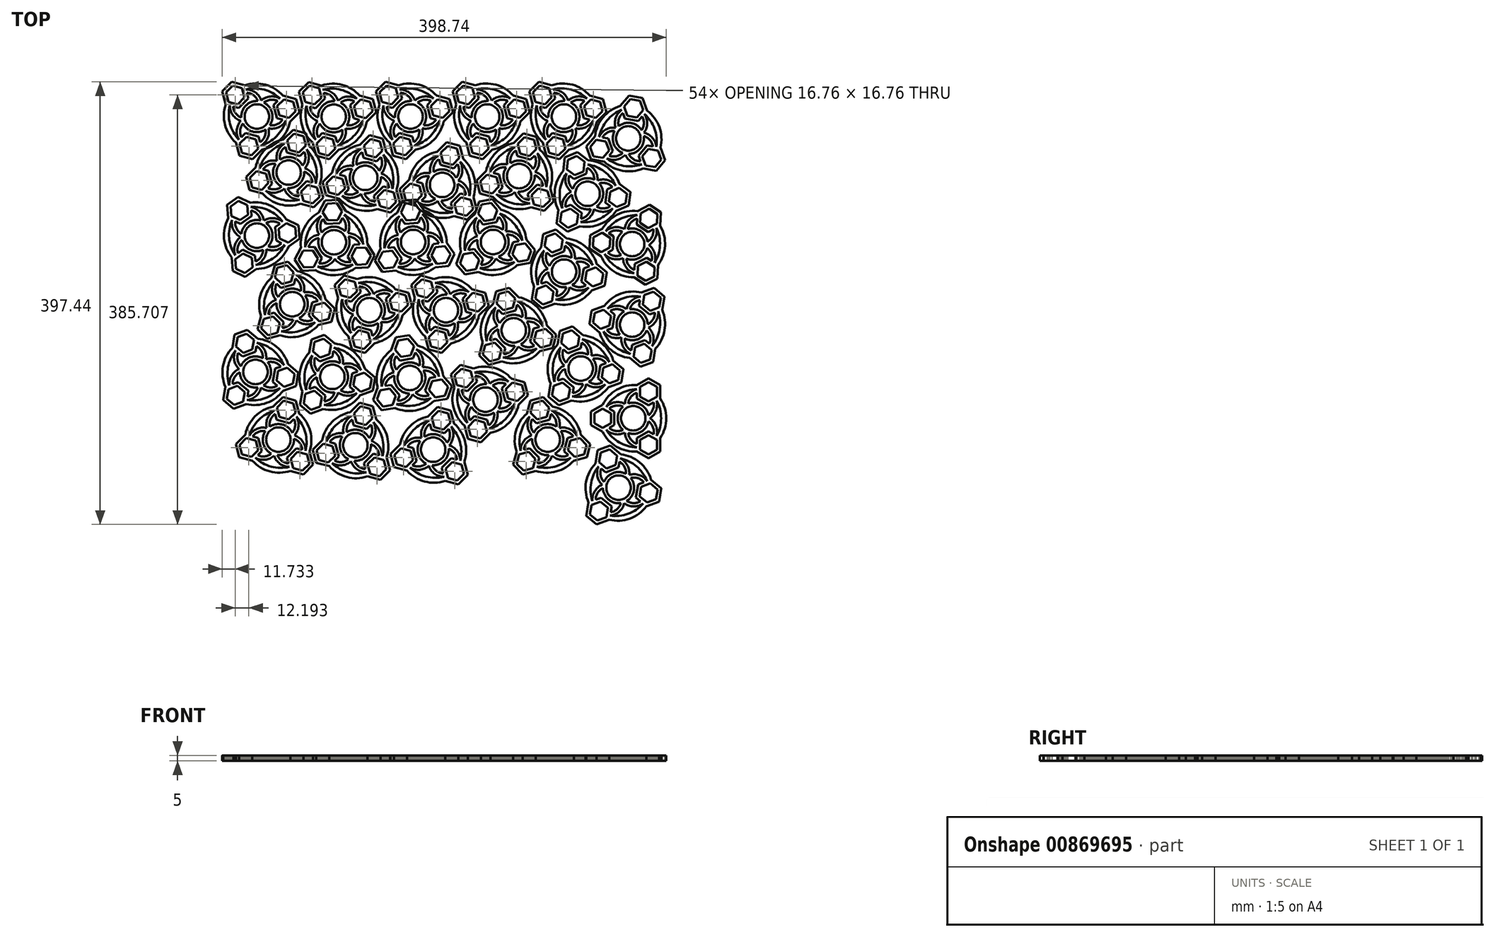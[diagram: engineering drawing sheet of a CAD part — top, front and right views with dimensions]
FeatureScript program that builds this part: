
annotation { "Feature Type Name" : "Feature", "Feature Type Description" : "" }
export const myFeature = defineFeature(function(context is Context, id is Id, definition is map)
    precondition{}
    {
        {
            var Q0;
            Q0=qCreatedBy(makeId("Top.planeOp"),FACE);
            var sketch = newSketch(context, id + "F0", { "sketchPlane" : qUnion([Q0])});
            skArc(sketch, "E0", {"start": v(-13.28, 4.44) * mm, "mid": v(-12.12, -7) * mm, "end": v(-2.8, -13.72) * mm});
            skCircle(sketch, "E1", {"center": v(0, 0) * mm, "radius": 11 * mm});
            skLineSegment(sketch, "E2.0", {"start": v(-4.34, 34.98) * mm, "end": v(4.34, 34.98) * mm});
            skLineSegment(sketch, "E2.1", {"start": v(4.34, 34.98) * mm, "end": v(8.68, 27.46) * mm});
            skLineSegment(sketch, "E2.2", {"start": v(8.68, 27.46) * mm, "end": v(4.34, 19.95) * mm});
            skLineSegment(sketch, "E2.3", {"start": v(4.34, 19.95) * mm, "end": v(-4.34, 19.95) * mm});
            skLineSegment(sketch, "E2.4", {"start": v(-4.34, 19.95) * mm, "end": v(-8.68, 27.46) * mm});
            skLineSegment(sketch, "E2.5", {"start": v(-8.68, 27.46) * mm, "end": v(-4.34, 34.98) * mm});
            skPoint(sketch, "E2.0.midPoint", {"position": v(0, 34.98) * mm});
            skArc(sketch, "E3", {"start": v(-10.28, 24.23) * mm, "mid": v(-14.32, 16.28) * mm, "end": v(-12.95, 7.48) * mm});
            skArc(sketch, "E4", {"start": v(-8.7, 21.51) * mm, "mid": v(-11.38, 15.65) * mm, "end": v(-10.49, 9.28) * mm});
            skLineSegment(sketch, "E5.0", {"start": v(-6.07, 37.98) * mm, "end": v(6.07, 37.98) * mm});
            skLineSegment(sketch, "E5.1", {"start": v(6.07, 37.98) * mm, "end": v(12.14, 27.46) * mm});
            skLineSegment(sketch, "E5.3", {"start": v(6.07, 16.95) * mm, "end": v(-6.07, 16.95) * mm});
            skLineSegment(sketch, "E5.4", {"start": v(-6.07, 16.95) * mm, "end": v(-8.7, 21.51) * mm});
            skLineSegment(sketch, "E5.5", {"start": v(-12.14, 27.46) * mm, "end": v(-6.07, 37.98) * mm});
            skPoint(sketch, "E5.0.midPoint", {"position": v(0, 37.98) * mm});
            skLineSegment(sketch, "E6.trimOffspring", {"start": v(8.7, 21.51) * mm, "end": v(6.07, 16.95) * mm});
            skArc(sketch, "E7.trimOffspring", {"start": v(10.49, 9.28) * mm, "mid": v(11.38, 15.65) * mm, "end": v(8.7, 21.51) * mm});
            skArc(sketch, "E8.trimOffspring", {"start": v(10.49, 9.28) * mm, "mid": v(0, 14) * mm, "end": v(-10.49, 9.28) * mm});
            skArc(sketch, "E9.trimOffspring", {"start": v(12.95, 7.48) * mm, "mid": v(14.32, 16.28) * mm, "end": v(10.28, 24.23) * mm});
            skLineSegment(sketch, "E10.1.0", {"start": v(-32.46, -13.73) * mm, "end": v(-28.12, -6.22) * mm});
            skLineSegment(sketch, "E10.1.1", {"start": v(-17.71, -3.22) * mm, "end": v(-11.64, -13.73) * mm});
            skLineSegment(sketch, "E10.1.2", {"start": v(-22.98, -3.22) * mm, "end": v(-17.71, -3.22) * mm});
            skArc(sketch, "E10.1.3", {"start": v(-12.95, 7.48) * mm, "mid": v(-21.26, 4.26) * mm, "end": v(-26.12, -3.22) * mm});
            skLineSegment(sketch, "E10.1.5", {"start": v(-29.85, -24.25) * mm, "end": v(-35.92, -13.73) * mm});
            skArc(sketch, "E10.1.6", {"start": v(2.8, -13.72) * mm, "mid": v(12.12, -7) * mm, "end": v(13.28, 4.44) * mm});
            skArc(sketch, "E10.1.7", {"start": v(-13.28, 4.44) * mm, "mid": v(-19.25, 2.03) * mm, "end": v(-22.98, -3.22) * mm});
            skLineSegment(sketch, "E10.1.8", {"start": v(-15.1, -13.73) * mm, "end": v(-19.44, -21.25) * mm});
            skLineSegment(sketch, "E10.1.9", {"start": v(-28.12, -6.22) * mm, "end": v(-19.44, -6.22) * mm});
            skLineSegment(sketch, "E10.1.10", {"start": v(-19.44, -6.22) * mm, "end": v(-15.1, -13.73) * mm});
            skLineSegment(sketch, "E10.1.11", {"start": v(-11.64, -13.73) * mm, "end": v(-14.28, -18.3) * mm});
            skArc(sketch, "E10.1.12", {"start": v(-14.28, -18.3) * mm, "mid": v(-7.87, -17.68) * mm, "end": v(-2.8, -13.72) * mm});
            skArc(sketch, "E10.1.14", {"start": v(-15.85, -21.01) * mm, "mid": v(-6.94, -20.54) * mm, "end": v(0, -14.95) * mm});
            skLineSegment(sketch, "E10.1.15", {"start": v(-17.71, -24.25) * mm, "end": v(-29.85, -24.25) * mm});
            skLineSegment(sketch, "E10.1.16", {"start": v(-19.44, -21.25) * mm, "end": v(-28.12, -21.25) * mm});
            skPoint(sketch, "E10.1.17", {"position": v(-30.29, -17.49) * mm});
            skLineSegment(sketch, "E10.1.18", {"start": v(-35.92, -13.73) * mm, "end": v(-29.85, -3.22) * mm});
            skPoint(sketch, "E10.1.19", {"position": v(-32.89, -18.99) * mm});
            skLineSegment(sketch, "E10.1.20", {"start": v(-28.12, -21.25) * mm, "end": v(-32.46, -13.73) * mm});
            skLineSegment(sketch, "E10.2.0", {"start": v(28.12, -21.25) * mm, "end": v(19.44, -21.25) * mm});
            skLineSegment(sketch, "E10.2.1", {"start": v(11.64, -13.73) * mm, "end": v(17.71, -3.22) * mm});
            skLineSegment(sketch, "E10.2.2", {"start": v(14.28, -18.3) * mm, "end": v(11.64, -13.73) * mm});
            skArc(sketch, "E10.2.3", {"start": v(0, -14.95) * mm, "mid": v(6.94, -20.54) * mm, "end": v(15.85, -21.01) * mm});
            skArc(sketch, "E10.2.4", {"start": v(2.8, -13.72) * mm, "mid": v(12.12, -7) * mm, "end": v(13.28, 4.44) * mm});
            skLineSegment(sketch, "E10.2.5", {"start": v(35.92, -13.73) * mm, "end": v(29.85, -24.25) * mm});
            skArc(sketch, "E10.2.7", {"start": v(2.8, -13.72) * mm, "mid": v(7.87, -17.68) * mm, "end": v(14.28, -18.3) * mm});
            skLineSegment(sketch, "E10.2.8", {"start": v(19.44, -6.22) * mm, "end": v(28.12, -6.22) * mm});
            skLineSegment(sketch, "E10.2.9", {"start": v(19.44, -21.25) * mm, "end": v(15.1, -13.73) * mm});
            skLineSegment(sketch, "E10.2.10", {"start": v(15.1, -13.73) * mm, "end": v(19.44, -6.22) * mm});
            skLineSegment(sketch, "E10.2.11", {"start": v(17.71, -3.22) * mm, "end": v(22.98, -3.22) * mm});
            skArc(sketch, "E10.2.12", {"start": v(22.98, -3.22) * mm, "mid": v(19.25, 2.03) * mm, "end": v(13.28, 4.44) * mm});
            skArc(sketch, "E10.2.14", {"start": v(26.12, -3.22) * mm, "mid": v(21.26, 4.26) * mm, "end": v(12.95, 7.48) * mm});
            skLineSegment(sketch, "E10.2.15", {"start": v(29.85, -3.22) * mm, "end": v(35.92, -13.73) * mm});
            skLineSegment(sketch, "E10.2.16", {"start": v(28.12, -6.22) * mm, "end": v(32.46, -13.73) * mm});
            skPoint(sketch, "E10.2.17", {"position": v(30.29, -17.49) * mm});
            skLineSegment(sketch, "E10.2.18", {"start": v(29.85, -24.25) * mm, "end": v(17.71, -24.25) * mm});
            skPoint(sketch, "E10.2.19", {"position": v(32.89, -18.99) * mm});
            skLineSegment(sketch, "E10.2.20", {"start": v(32.46, -13.73) * mm, "end": v(28.12, -21.25) * mm});
            skArc(sketch, "E11", {"start": v(-10.28, 24.23) * mm, "mid": v(-21.68, 12.52) * mm, "end": v(-26.12, -3.22) * mm});
            skArc(sketch, "E12", {"start": v(-12.14, 27.46) * mm, "mid": v(-25.63, 14.8) * mm, "end": v(-29.85, -3.22) * mm});
            skArc(sketch, "E13.1.0", {"start": v(-15.85, -21.01) * mm, "mid": v(0, -25.04) * mm, "end": v(15.85, -21.01) * mm});
            skArc(sketch, "E13.1.1", {"start": v(-17.71, -24.25) * mm, "mid": v(0, -29.6) * mm, "end": v(17.71, -24.25) * mm});
            skArc(sketch, "E13.2.0", {"start": v(26.12, -3.22) * mm, "mid": v(21.68, 12.52) * mm, "end": v(10.28, 24.23) * mm});
            skArc(sketch, "E13.2.1", {"start": v(29.85, -3.22) * mm, "mid": v(25.63, 14.8) * mm, "end": v(12.14, 27.46) * mm});
            skSolve(sketch);
        }
        {
            var Q0;
            Q0=makeQuery(id+"F0.imprint","IMPRINT",FACE,{"disambiguationData":[TD([[makeQuery(id+"F0.imprint","IMPRINT",EDGE,{"derivedFrom":sQuery(id+"F0.wireOp",EDGE,"E2.0")}),1.0]])]});
            extrude(context, id + "F1", {"entities" : qUnion([Q0]), "depth" : 5 * mm, "offsetDistance" : 25 * mm});
        }
        {
            var Q0;
            Q0=makeQuery(id+"F1.opExtrude","SWEPT_BODY",BODY,{"disambiguationData":[OSD([sQuery(id+"F0.wireOp",EDGE,"E2.0"),sQuery(id+"F0.wireOp",EDGE,"E2.1"),sQuery(id+"F0.wireOp",EDGE,"E2.2"),sQuery(id+"F0.wireOp",EDGE,"E2.3"),sQuery(id+"F0.wireOp",EDGE,"E2.4"),sQuery(id+"F0.wireOp",EDGE,"E2.5"),sQuery(id+"F0.wireOp",EDGE,"E3"),sQuery(id+"F0.wireOp",EDGE,"E4"),sQuery(id+"F0.wireOp",EDGE,"E5.0"),sQuery(id+"F0.wireOp",EDGE,"E5.1"),sQuery(id+"F0.wireOp",EDGE,"E5.3"),sQuery(id+"F0.wireOp",EDGE,"E5.4"),sQuery(id+"F0.wireOp",EDGE,"E5.5"),sQuery(id+"F0.wireOp",EDGE,"E6.trimOffspring"),sQuery(id+"F0.wireOp",EDGE,"E7.trimOffspring"),sQuery(id+"F0.wireOp",EDGE,"E9.trimOffspring"),sQuery(id+"F0.wireOp",EDGE,"E10.1.0"),sQuery(id+"F0.wireOp",EDGE,"E10.1.1"),sQuery(id+"F0.wireOp",EDGE,"E10.1.2"),sQuery(id+"F0.wireOp",EDGE,"E10.1.3"),sQuery(id+"F0.wireOp",EDGE,"E10.1.5"),sQuery(id+"F0.wireOp",EDGE,"E10.1.7"),sQuery(id+"F0.wireOp",EDGE,"E10.1.8"),sQuery(id+"F0.wireOp",EDGE,"E10.1.9"),sQuery(id+"F0.wireOp",EDGE,"E10.1.10"),sQuery(id+"F0.wireOp",EDGE,"E10.1.11"),sQuery(id+"F0.wireOp",EDGE,"E10.1.12"),sQuery(id+"F0.wireOp",EDGE,"E10.1.14"),sQuery(id+"F0.wireOp",EDGE,"E10.1.15"),sQuery(id+"F0.wireOp",EDGE,"E10.1.16"),sQuery(id+"F0.wireOp",EDGE,"E10.1.18"),sQuery(id+"F0.wireOp",EDGE,"E10.1.20"),sQuery(id+"F0.wireOp",EDGE,"E10.2.0"),sQuery(id+"F0.wireOp",EDGE,"E10.2.1"),sQuery(id+"F0.wireOp",EDGE,"E10.2.2"),sQuery(id+"F0.wireOp",EDGE,"E10.2.3"),sQuery(id+"F0.wireOp",EDGE,"E10.2.5"),sQuery(id+"F0.wireOp",EDGE,"E10.2.7"),sQuery(id+"F0.wireOp",EDGE,"E10.2.8"),sQuery(id+"F0.wireOp",EDGE,"E10.2.9"),sQuery(id+"F0.wireOp",EDGE,"E10.2.10"),sQuery(id+"F0.wireOp",EDGE,"E10.2.11"),sQuery(id+"F0.wireOp",EDGE,"E10.2.12"),sQuery(id+"F0.wireOp",EDGE,"E1"),sQuery(id+"F0.wireOp",EDGE,"E10.2.14"),sQuery(id+"F0.wireOp",EDGE,"E10.2.15"),sQuery(id+"F0.wireOp",EDGE,"E10.2.16"),sQuery(id+"F0.wireOp",EDGE,"E10.2.18"),sQuery(id+"F0.wireOp",EDGE,"E10.2.20"),sQuery(id+"F0.wireOp",EDGE,"E8.trimOffspring"),sQuery(id+"F0.wireOp",EDGE,"E0"),sQuery(id+"F0.wireOp",EDGE,"E10.1.6"),sQuery(id+"F0.wireOp",EDGE,"E11"),sQuery(id+"F0.wireOp",EDGE,"E12"),sQuery(id+"F0.wireOp",EDGE,"E13.1.0"),sQuery(id+"F0.wireOp",EDGE,"E13.1.1"),sQuery(id+"F0.wireOp",EDGE,"E13.2.0"),sQuery(id+"F0.wireOp",EDGE,"E13.2.1")])]});
            transform(context, id + "F2", {"entities" : qUnion([Q0]), "transformType" : TransformType.TRANSLATION_3D, "dx" : -159 * mm, "dy" : 162 * mm, "dz" : 0 * mm, "makeCopy" : false});
        }
        {
            var Q0;
            Q0=makeQuery(id+"F1.opExtrude","SWEPT_BODY",BODY,{"disambiguationData":[OSD([sQuery(id+"F0.wireOp",EDGE,"E2.0"),sQuery(id+"F0.wireOp",EDGE,"E2.1"),sQuery(id+"F0.wireOp",EDGE,"E2.2"),sQuery(id+"F0.wireOp",EDGE,"E2.3"),sQuery(id+"F0.wireOp",EDGE,"E2.4"),sQuery(id+"F0.wireOp",EDGE,"E2.5"),sQuery(id+"F0.wireOp",EDGE,"E3"),sQuery(id+"F0.wireOp",EDGE,"E4"),sQuery(id+"F0.wireOp",EDGE,"E5.0"),sQuery(id+"F0.wireOp",EDGE,"E5.1"),sQuery(id+"F0.wireOp",EDGE,"E5.3"),sQuery(id+"F0.wireOp",EDGE,"E5.4"),sQuery(id+"F0.wireOp",EDGE,"E5.5"),sQuery(id+"F0.wireOp",EDGE,"E6.trimOffspring"),sQuery(id+"F0.wireOp",EDGE,"E7.trimOffspring"),sQuery(id+"F0.wireOp",EDGE,"E9.trimOffspring"),sQuery(id+"F0.wireOp",EDGE,"E10.1.0"),sQuery(id+"F0.wireOp",EDGE,"E10.1.1"),sQuery(id+"F0.wireOp",EDGE,"E10.1.2"),sQuery(id+"F0.wireOp",EDGE,"E10.1.3"),sQuery(id+"F0.wireOp",EDGE,"E10.1.5"),sQuery(id+"F0.wireOp",EDGE,"E10.1.7"),sQuery(id+"F0.wireOp",EDGE,"E10.1.8"),sQuery(id+"F0.wireOp",EDGE,"E10.1.9"),sQuery(id+"F0.wireOp",EDGE,"E10.1.10"),sQuery(id+"F0.wireOp",EDGE,"E10.1.11"),sQuery(id+"F0.wireOp",EDGE,"E10.1.12"),sQuery(id+"F0.wireOp",EDGE,"E10.1.14"),sQuery(id+"F0.wireOp",EDGE,"E10.1.15"),sQuery(id+"F0.wireOp",EDGE,"E10.1.16"),sQuery(id+"F0.wireOp",EDGE,"E10.1.18"),sQuery(id+"F0.wireOp",EDGE,"E10.1.20"),sQuery(id+"F0.wireOp",EDGE,"E10.2.0"),sQuery(id+"F0.wireOp",EDGE,"E10.2.1"),sQuery(id+"F0.wireOp",EDGE,"E10.2.2"),sQuery(id+"F0.wireOp",EDGE,"E10.2.3"),sQuery(id+"F0.wireOp",EDGE,"E10.2.5"),sQuery(id+"F0.wireOp",EDGE,"E10.2.7"),sQuery(id+"F0.wireOp",EDGE,"E10.2.8"),sQuery(id+"F0.wireOp",EDGE,"E10.2.9"),sQuery(id+"F0.wireOp",EDGE,"E10.2.10"),sQuery(id+"F0.wireOp",EDGE,"E10.2.11"),sQuery(id+"F0.wireOp",EDGE,"E10.2.12"),sQuery(id+"F0.wireOp",EDGE,"E1"),sQuery(id+"F0.wireOp",EDGE,"E10.2.14"),sQuery(id+"F0.wireOp",EDGE,"E10.2.15"),sQuery(id+"F0.wireOp",EDGE,"E10.2.16"),sQuery(id+"F0.wireOp",EDGE,"E10.2.18"),sQuery(id+"F0.wireOp",EDGE,"E10.2.20"),sQuery(id+"F0.wireOp",EDGE,"E8.trimOffspring"),sQuery(id+"F0.wireOp",EDGE,"E0"),sQuery(id+"F0.wireOp",EDGE,"E10.1.6"),sQuery(id+"F0.wireOp",EDGE,"E11"),sQuery(id+"F0.wireOp",EDGE,"E12"),sQuery(id+"F0.wireOp",EDGE,"E13.1.0"),sQuery(id+"F0.wireOp",EDGE,"E13.1.1"),sQuery(id+"F0.wireOp",EDGE,"E13.2.0"),sQuery(id+"F0.wireOp",EDGE,"E13.2.1")])]});
            var Q1;
            Q1=makeQuery(id+"F1.opExtrude","CAP_EDGE",EDGE,{"disambiguationData":[OSD([sQuery(id+"F0.wireOp",EDGE,"E1")])],"isStart":false});
            transform(context, id + "F3", {"entities" : qUnion([Q0]), "transformType" : TransformType.ROTATION, "transformAxis" : qUnion([Q1]), "angle" : 45 * degree, "makeCopy" : false});
        }
        {
            var Q0;
            Q0=makeQuery(id+"F1.opExtrude","SWEPT_BODY",BODY,{"disambiguationData":[OSD([sQuery(id+"F0.wireOp",EDGE,"E2.0"),sQuery(id+"F0.wireOp",EDGE,"E2.1"),sQuery(id+"F0.wireOp",EDGE,"E2.2"),sQuery(id+"F0.wireOp",EDGE,"E2.3"),sQuery(id+"F0.wireOp",EDGE,"E2.4"),sQuery(id+"F0.wireOp",EDGE,"E2.5"),sQuery(id+"F0.wireOp",EDGE,"E3"),sQuery(id+"F0.wireOp",EDGE,"E4"),sQuery(id+"F0.wireOp",EDGE,"E5.0"),sQuery(id+"F0.wireOp",EDGE,"E5.1"),sQuery(id+"F0.wireOp",EDGE,"E5.3"),sQuery(id+"F0.wireOp",EDGE,"E5.4"),sQuery(id+"F0.wireOp",EDGE,"E5.5"),sQuery(id+"F0.wireOp",EDGE,"E6.trimOffspring"),sQuery(id+"F0.wireOp",EDGE,"E7.trimOffspring"),sQuery(id+"F0.wireOp",EDGE,"E9.trimOffspring"),sQuery(id+"F0.wireOp",EDGE,"E10.1.0"),sQuery(id+"F0.wireOp",EDGE,"E10.1.1"),sQuery(id+"F0.wireOp",EDGE,"E10.1.2"),sQuery(id+"F0.wireOp",EDGE,"E10.1.3"),sQuery(id+"F0.wireOp",EDGE,"E10.1.5"),sQuery(id+"F0.wireOp",EDGE,"E10.1.7"),sQuery(id+"F0.wireOp",EDGE,"E10.1.8"),sQuery(id+"F0.wireOp",EDGE,"E10.1.9"),sQuery(id+"F0.wireOp",EDGE,"E10.1.10"),sQuery(id+"F0.wireOp",EDGE,"E10.1.11"),sQuery(id+"F0.wireOp",EDGE,"E10.1.12"),sQuery(id+"F0.wireOp",EDGE,"E10.1.14"),sQuery(id+"F0.wireOp",EDGE,"E10.1.15"),sQuery(id+"F0.wireOp",EDGE,"E10.1.16"),sQuery(id+"F0.wireOp",EDGE,"E10.1.18"),sQuery(id+"F0.wireOp",EDGE,"E10.1.20"),sQuery(id+"F0.wireOp",EDGE,"E10.2.0"),sQuery(id+"F0.wireOp",EDGE,"E10.2.1"),sQuery(id+"F0.wireOp",EDGE,"E10.2.2"),sQuery(id+"F0.wireOp",EDGE,"E10.2.3"),sQuery(id+"F0.wireOp",EDGE,"E10.2.5"),sQuery(id+"F0.wireOp",EDGE,"E10.2.7"),sQuery(id+"F0.wireOp",EDGE,"E10.2.8"),sQuery(id+"F0.wireOp",EDGE,"E10.2.9"),sQuery(id+"F0.wireOp",EDGE,"E10.2.10"),sQuery(id+"F0.wireOp",EDGE,"E10.2.11"),sQuery(id+"F0.wireOp",EDGE,"E10.2.12"),sQuery(id+"F0.wireOp",EDGE,"E1"),sQuery(id+"F0.wireOp",EDGE,"E10.2.14"),sQuery(id+"F0.wireOp",EDGE,"E10.2.15"),sQuery(id+"F0.wireOp",EDGE,"E10.2.16"),sQuery(id+"F0.wireOp",EDGE,"E10.2.18"),sQuery(id+"F0.wireOp",EDGE,"E10.2.20"),sQuery(id+"F0.wireOp",EDGE,"E8.trimOffspring"),sQuery(id+"F0.wireOp",EDGE,"E0"),sQuery(id+"F0.wireOp",EDGE,"E10.1.6"),sQuery(id+"F0.wireOp",EDGE,"E11"),sQuery(id+"F0.wireOp",EDGE,"E12"),sQuery(id+"F0.wireOp",EDGE,"E13.1.0"),sQuery(id+"F0.wireOp",EDGE,"E13.1.1"),sQuery(id+"F0.wireOp",EDGE,"E13.2.0"),sQuery(id+"F0.wireOp",EDGE,"E13.2.1")])]});
            transform(context, id + "F4", {"entities" : qUnion([Q0]), "transformType" : TransformType.TRANSLATION_3D, "dx" : -4.9 * mm, "dy" : 7.3 * mm, "dz" : 0 * mm, "makeCopy" : false});
        }
        {
            var Q0;
            Q0=makeQuery(id+"F1.opExtrude","SWEPT_BODY",BODY,{"disambiguationData":[OSD([sQuery(id+"F0.wireOp",EDGE,"E2.0"),sQuery(id+"F0.wireOp",EDGE,"E2.1"),sQuery(id+"F0.wireOp",EDGE,"E2.2"),sQuery(id+"F0.wireOp",EDGE,"E2.3"),sQuery(id+"F0.wireOp",EDGE,"E2.4"),sQuery(id+"F0.wireOp",EDGE,"E2.5"),sQuery(id+"F0.wireOp",EDGE,"E3"),sQuery(id+"F0.wireOp",EDGE,"E4"),sQuery(id+"F0.wireOp",EDGE,"E5.0"),sQuery(id+"F0.wireOp",EDGE,"E5.1"),sQuery(id+"F0.wireOp",EDGE,"E5.3"),sQuery(id+"F0.wireOp",EDGE,"E5.4"),sQuery(id+"F0.wireOp",EDGE,"E5.5"),sQuery(id+"F0.wireOp",EDGE,"E6.trimOffspring"),sQuery(id+"F0.wireOp",EDGE,"E7.trimOffspring"),sQuery(id+"F0.wireOp",EDGE,"E9.trimOffspring"),sQuery(id+"F0.wireOp",EDGE,"E10.1.0"),sQuery(id+"F0.wireOp",EDGE,"E10.1.1"),sQuery(id+"F0.wireOp",EDGE,"E10.1.2"),sQuery(id+"F0.wireOp",EDGE,"E10.1.3"),sQuery(id+"F0.wireOp",EDGE,"E10.1.5"),sQuery(id+"F0.wireOp",EDGE,"E10.1.7"),sQuery(id+"F0.wireOp",EDGE,"E10.1.8"),sQuery(id+"F0.wireOp",EDGE,"E10.1.9"),sQuery(id+"F0.wireOp",EDGE,"E10.1.10"),sQuery(id+"F0.wireOp",EDGE,"E10.1.11"),sQuery(id+"F0.wireOp",EDGE,"E10.1.12"),sQuery(id+"F0.wireOp",EDGE,"E10.1.14"),sQuery(id+"F0.wireOp",EDGE,"E10.1.15"),sQuery(id+"F0.wireOp",EDGE,"E10.1.16"),sQuery(id+"F0.wireOp",EDGE,"E10.1.18"),sQuery(id+"F0.wireOp",EDGE,"E10.1.20"),sQuery(id+"F0.wireOp",EDGE,"E10.2.0"),sQuery(id+"F0.wireOp",EDGE,"E10.2.1"),sQuery(id+"F0.wireOp",EDGE,"E10.2.2"),sQuery(id+"F0.wireOp",EDGE,"E10.2.3"),sQuery(id+"F0.wireOp",EDGE,"E10.2.5"),sQuery(id+"F0.wireOp",EDGE,"E10.2.7"),sQuery(id+"F0.wireOp",EDGE,"E10.2.8"),sQuery(id+"F0.wireOp",EDGE,"E10.2.9"),sQuery(id+"F0.wireOp",EDGE,"E10.2.10"),sQuery(id+"F0.wireOp",EDGE,"E10.2.11"),sQuery(id+"F0.wireOp",EDGE,"E10.2.12"),sQuery(id+"F0.wireOp",EDGE,"E1"),sQuery(id+"F0.wireOp",EDGE,"E10.2.14"),sQuery(id+"F0.wireOp",EDGE,"E10.2.15"),sQuery(id+"F0.wireOp",EDGE,"E10.2.16"),sQuery(id+"F0.wireOp",EDGE,"E10.2.18"),sQuery(id+"F0.wireOp",EDGE,"E10.2.20"),sQuery(id+"F0.wireOp",EDGE,"E8.trimOffspring"),sQuery(id+"F0.wireOp",EDGE,"E0"),sQuery(id+"F0.wireOp",EDGE,"E10.1.6"),sQuery(id+"F0.wireOp",EDGE,"E11"),sQuery(id+"F0.wireOp",EDGE,"E12"),sQuery(id+"F0.wireOp",EDGE,"E13.1.0"),sQuery(id+"F0.wireOp",EDGE,"E13.1.1"),sQuery(id+"F0.wireOp",EDGE,"E13.2.0"),sQuery(id+"F0.wireOp",EDGE,"E13.2.1")])]});
            transform(context, id + "F5", {"entities" : qUnion([Q0]), "transformType" : TransformType.TRANSLATION_3D, "dx" : 69 * mm, "dy" : -0.1 * mm, "dz" : 0 * mm, "makeCopy" : true});
        }
        {
            var Q0;
            Q0=makeQuery(id+"F5.opPattern","COPY",BODY,{"derivedFrom":makeQuery(id+"F1.opExtrude","SWEPT_BODY",BODY,{"disambiguationData":[OSD([sQuery(id+"F0.wireOp",EDGE,"E2.0"),sQuery(id+"F0.wireOp",EDGE,"E2.1"),sQuery(id+"F0.wireOp",EDGE,"E2.2"),sQuery(id+"F0.wireOp",EDGE,"E2.3"),sQuery(id+"F0.wireOp",EDGE,"E2.4"),sQuery(id+"F0.wireOp",EDGE,"E2.5"),sQuery(id+"F0.wireOp",EDGE,"E3"),sQuery(id+"F0.wireOp",EDGE,"E4"),sQuery(id+"F0.wireOp",EDGE,"E5.0"),sQuery(id+"F0.wireOp",EDGE,"E5.1"),sQuery(id+"F0.wireOp",EDGE,"E5.3"),sQuery(id+"F0.wireOp",EDGE,"E5.4"),sQuery(id+"F0.wireOp",EDGE,"E5.5"),sQuery(id+"F0.wireOp",EDGE,"E6.trimOffspring"),sQuery(id+"F0.wireOp",EDGE,"E7.trimOffspring"),sQuery(id+"F0.wireOp",EDGE,"E9.trimOffspring"),sQuery(id+"F0.wireOp",EDGE,"E10.1.0"),sQuery(id+"F0.wireOp",EDGE,"E10.1.1"),sQuery(id+"F0.wireOp",EDGE,"E10.1.2"),sQuery(id+"F0.wireOp",EDGE,"E10.1.3"),sQuery(id+"F0.wireOp",EDGE,"E10.1.5"),sQuery(id+"F0.wireOp",EDGE,"E10.1.7"),sQuery(id+"F0.wireOp",EDGE,"E10.1.8"),sQuery(id+"F0.wireOp",EDGE,"E10.1.9"),sQuery(id+"F0.wireOp",EDGE,"E10.1.10"),sQuery(id+"F0.wireOp",EDGE,"E10.1.11"),sQuery(id+"F0.wireOp",EDGE,"E10.1.12"),sQuery(id+"F0.wireOp",EDGE,"E10.1.14"),sQuery(id+"F0.wireOp",EDGE,"E10.1.15"),sQuery(id+"F0.wireOp",EDGE,"E10.1.16"),sQuery(id+"F0.wireOp",EDGE,"E10.1.18"),sQuery(id+"F0.wireOp",EDGE,"E10.1.20"),sQuery(id+"F0.wireOp",EDGE,"E10.2.0"),sQuery(id+"F0.wireOp",EDGE,"E10.2.1"),sQuery(id+"F0.wireOp",EDGE,"E10.2.2"),sQuery(id+"F0.wireOp",EDGE,"E10.2.3"),sQuery(id+"F0.wireOp",EDGE,"E10.2.5"),sQuery(id+"F0.wireOp",EDGE,"E10.2.7"),sQuery(id+"F0.wireOp",EDGE,"E10.2.8"),sQuery(id+"F0.wireOp",EDGE,"E10.2.9"),sQuery(id+"F0.wireOp",EDGE,"E10.2.10"),sQuery(id+"F0.wireOp",EDGE,"E10.2.11"),sQuery(id+"F0.wireOp",EDGE,"E10.2.12"),sQuery(id+"F0.wireOp",EDGE,"E1"),sQuery(id+"F0.wireOp",EDGE,"E10.2.14"),sQuery(id+"F0.wireOp",EDGE,"E10.2.15"),sQuery(id+"F0.wireOp",EDGE,"E10.2.16"),sQuery(id+"F0.wireOp",EDGE,"E10.2.18"),sQuery(id+"F0.wireOp",EDGE,"E10.2.20"),sQuery(id+"F0.wireOp",EDGE,"E8.trimOffspring"),sQuery(id+"F0.wireOp",EDGE,"E0"),sQuery(id+"F0.wireOp",EDGE,"E10.1.6"),sQuery(id+"F0.wireOp",EDGE,"E11"),sQuery(id+"F0.wireOp",EDGE,"E12"),sQuery(id+"F0.wireOp",EDGE,"E13.1.0"),sQuery(id+"F0.wireOp",EDGE,"E13.1.1"),sQuery(id+"F0.wireOp",EDGE,"E13.2.0"),sQuery(id+"F0.wireOp",EDGE,"E13.2.1")])]}),"instanceName":"1"});
            var Q1;
            Q1=makeQuery(id+"F5.opPattern","COPY",EDGE,{"derivedFrom":makeQuery(id+"F1.opExtrude","CAP_EDGE",EDGE,{"disambiguationData":[OSD([sQuery(id+"F0.wireOp",EDGE,"E1")])],"isStart":false}),"instanceName":"1"});
            transform(context, id + "F6", {"entities" : qUnion([Q0]), "transformType" : TransformType.ROTATION, "transformAxis" : qUnion([Q1]), "angle" : 120 * degree, "makeCopy" : false});
        }
        {
            var Q0;
            Q0=makeQuery(id+"F1.opExtrude","SWEPT_BODY",BODY,{"disambiguationData":[OSD([sQuery(id+"F0.wireOp",EDGE,"E2.0"),sQuery(id+"F0.wireOp",EDGE,"E2.1"),sQuery(id+"F0.wireOp",EDGE,"E2.2"),sQuery(id+"F0.wireOp",EDGE,"E2.3"),sQuery(id+"F0.wireOp",EDGE,"E2.4"),sQuery(id+"F0.wireOp",EDGE,"E2.5"),sQuery(id+"F0.wireOp",EDGE,"E3"),sQuery(id+"F0.wireOp",EDGE,"E4"),sQuery(id+"F0.wireOp",EDGE,"E5.0"),sQuery(id+"F0.wireOp",EDGE,"E5.1"),sQuery(id+"F0.wireOp",EDGE,"E5.3"),sQuery(id+"F0.wireOp",EDGE,"E5.4"),sQuery(id+"F0.wireOp",EDGE,"E5.5"),sQuery(id+"F0.wireOp",EDGE,"E6.trimOffspring"),sQuery(id+"F0.wireOp",EDGE,"E7.trimOffspring"),sQuery(id+"F0.wireOp",EDGE,"E9.trimOffspring"),sQuery(id+"F0.wireOp",EDGE,"E10.1.0"),sQuery(id+"F0.wireOp",EDGE,"E10.1.1"),sQuery(id+"F0.wireOp",EDGE,"E10.1.2"),sQuery(id+"F0.wireOp",EDGE,"E10.1.3"),sQuery(id+"F0.wireOp",EDGE,"E10.1.5"),sQuery(id+"F0.wireOp",EDGE,"E10.1.7"),sQuery(id+"F0.wireOp",EDGE,"E10.1.8"),sQuery(id+"F0.wireOp",EDGE,"E10.1.9"),sQuery(id+"F0.wireOp",EDGE,"E10.1.10"),sQuery(id+"F0.wireOp",EDGE,"E10.1.11"),sQuery(id+"F0.wireOp",EDGE,"E10.1.12"),sQuery(id+"F0.wireOp",EDGE,"E10.1.14"),sQuery(id+"F0.wireOp",EDGE,"E10.1.15"),sQuery(id+"F0.wireOp",EDGE,"E10.1.16"),sQuery(id+"F0.wireOp",EDGE,"E10.1.18"),sQuery(id+"F0.wireOp",EDGE,"E10.1.20"),sQuery(id+"F0.wireOp",EDGE,"E10.2.0"),sQuery(id+"F0.wireOp",EDGE,"E10.2.1"),sQuery(id+"F0.wireOp",EDGE,"E10.2.2"),sQuery(id+"F0.wireOp",EDGE,"E10.2.3"),sQuery(id+"F0.wireOp",EDGE,"E10.2.5"),sQuery(id+"F0.wireOp",EDGE,"E10.2.7"),sQuery(id+"F0.wireOp",EDGE,"E10.2.8"),sQuery(id+"F0.wireOp",EDGE,"E10.2.9"),sQuery(id+"F0.wireOp",EDGE,"E10.2.10"),sQuery(id+"F0.wireOp",EDGE,"E10.2.11"),sQuery(id+"F0.wireOp",EDGE,"E10.2.12"),sQuery(id+"F0.wireOp",EDGE,"E1"),sQuery(id+"F0.wireOp",EDGE,"E10.2.14"),sQuery(id+"F0.wireOp",EDGE,"E10.2.15"),sQuery(id+"F0.wireOp",EDGE,"E10.2.16"),sQuery(id+"F0.wireOp",EDGE,"E10.2.18"),sQuery(id+"F0.wireOp",EDGE,"E10.2.20"),sQuery(id+"F0.wireOp",EDGE,"E8.trimOffspring"),sQuery(id+"F0.wireOp",EDGE,"E0"),sQuery(id+"F0.wireOp",EDGE,"E10.1.6"),sQuery(id+"F0.wireOp",EDGE,"E11"),sQuery(id+"F0.wireOp",EDGE,"E12"),sQuery(id+"F0.wireOp",EDGE,"E13.1.0"),sQuery(id+"F0.wireOp",EDGE,"E13.1.1"),sQuery(id+"F0.wireOp",EDGE,"E13.2.0"),sQuery(id+"F0.wireOp",EDGE,"E13.2.1")])]});
            transform(context, id + "F7", {"entities" : qUnion([Q0]), "transformType" : TransformType.TRANSLATION_3D, "dx" : 138 * mm, "dy" : 0 * mm, "dz" : 0 * mm, "makeCopy" : true});
        }
        {
            var Q0;
            Q0=makeQuery(id+"F7.opPattern","COPY",BODY,{"derivedFrom":makeQuery(id+"F1.opExtrude","SWEPT_BODY",BODY,{"disambiguationData":[OSD([sQuery(id+"F0.wireOp",EDGE,"E2.0"),sQuery(id+"F0.wireOp",EDGE,"E2.1"),sQuery(id+"F0.wireOp",EDGE,"E2.2"),sQuery(id+"F0.wireOp",EDGE,"E2.3"),sQuery(id+"F0.wireOp",EDGE,"E2.4"),sQuery(id+"F0.wireOp",EDGE,"E2.5"),sQuery(id+"F0.wireOp",EDGE,"E3"),sQuery(id+"F0.wireOp",EDGE,"E4"),sQuery(id+"F0.wireOp",EDGE,"E5.0"),sQuery(id+"F0.wireOp",EDGE,"E5.1"),sQuery(id+"F0.wireOp",EDGE,"E5.3"),sQuery(id+"F0.wireOp",EDGE,"E5.4"),sQuery(id+"F0.wireOp",EDGE,"E5.5"),sQuery(id+"F0.wireOp",EDGE,"E6.trimOffspring"),sQuery(id+"F0.wireOp",EDGE,"E7.trimOffspring"),sQuery(id+"F0.wireOp",EDGE,"E9.trimOffspring"),sQuery(id+"F0.wireOp",EDGE,"E10.1.0"),sQuery(id+"F0.wireOp",EDGE,"E10.1.1"),sQuery(id+"F0.wireOp",EDGE,"E10.1.2"),sQuery(id+"F0.wireOp",EDGE,"E10.1.3"),sQuery(id+"F0.wireOp",EDGE,"E10.1.5"),sQuery(id+"F0.wireOp",EDGE,"E10.1.7"),sQuery(id+"F0.wireOp",EDGE,"E10.1.8"),sQuery(id+"F0.wireOp",EDGE,"E10.1.9"),sQuery(id+"F0.wireOp",EDGE,"E10.1.10"),sQuery(id+"F0.wireOp",EDGE,"E10.1.11"),sQuery(id+"F0.wireOp",EDGE,"E10.1.12"),sQuery(id+"F0.wireOp",EDGE,"E10.1.14"),sQuery(id+"F0.wireOp",EDGE,"E10.1.15"),sQuery(id+"F0.wireOp",EDGE,"E10.1.16"),sQuery(id+"F0.wireOp",EDGE,"E10.1.18"),sQuery(id+"F0.wireOp",EDGE,"E10.1.20"),sQuery(id+"F0.wireOp",EDGE,"E10.2.0"),sQuery(id+"F0.wireOp",EDGE,"E10.2.1"),sQuery(id+"F0.wireOp",EDGE,"E10.2.2"),sQuery(id+"F0.wireOp",EDGE,"E10.2.3"),sQuery(id+"F0.wireOp",EDGE,"E10.2.5"),sQuery(id+"F0.wireOp",EDGE,"E10.2.7"),sQuery(id+"F0.wireOp",EDGE,"E10.2.8"),sQuery(id+"F0.wireOp",EDGE,"E10.2.9"),sQuery(id+"F0.wireOp",EDGE,"E10.2.10"),sQuery(id+"F0.wireOp",EDGE,"E10.2.11"),sQuery(id+"F0.wireOp",EDGE,"E10.2.12"),sQuery(id+"F0.wireOp",EDGE,"E1"),sQuery(id+"F0.wireOp",EDGE,"E10.2.14"),sQuery(id+"F0.wireOp",EDGE,"E10.2.15"),sQuery(id+"F0.wireOp",EDGE,"E10.2.16"),sQuery(id+"F0.wireOp",EDGE,"E10.2.18"),sQuery(id+"F0.wireOp",EDGE,"E10.2.20"),sQuery(id+"F0.wireOp",EDGE,"E8.trimOffspring"),sQuery(id+"F0.wireOp",EDGE,"E0"),sQuery(id+"F0.wireOp",EDGE,"E10.1.6"),sQuery(id+"F0.wireOp",EDGE,"E11"),sQuery(id+"F0.wireOp",EDGE,"E12"),sQuery(id+"F0.wireOp",EDGE,"E13.1.0"),sQuery(id+"F0.wireOp",EDGE,"E13.1.1"),sQuery(id+"F0.wireOp",EDGE,"E13.2.0"),sQuery(id+"F0.wireOp",EDGE,"E13.2.1")])]}),"instanceName":"1"});
            transform(context, id + "F8", {"entities" : qUnion([Q0]), "transformType" : TransformType.TRANSLATION_3D, "dx" : 68.9 * mm, "dy" : 0 * mm, "dz" : 0 * mm, "makeCopy" : true});
        }
        {
            var Q0;
            Q0=makeQuery(id+"F8.opPattern","COPY",BODY,{"derivedFrom":makeQuery(id+"F7.opPattern","COPY",BODY,{"derivedFrom":makeQuery(id+"F1.opExtrude","SWEPT_BODY",BODY,{"disambiguationData":[OSD([sQuery(id+"F0.wireOp",EDGE,"E2.0"),sQuery(id+"F0.wireOp",EDGE,"E2.1"),sQuery(id+"F0.wireOp",EDGE,"E2.2"),sQuery(id+"F0.wireOp",EDGE,"E2.3"),sQuery(id+"F0.wireOp",EDGE,"E2.4"),sQuery(id+"F0.wireOp",EDGE,"E2.5"),sQuery(id+"F0.wireOp",EDGE,"E3"),sQuery(id+"F0.wireOp",EDGE,"E4"),sQuery(id+"F0.wireOp",EDGE,"E5.0"),sQuery(id+"F0.wireOp",EDGE,"E5.1"),sQuery(id+"F0.wireOp",EDGE,"E5.3"),sQuery(id+"F0.wireOp",EDGE,"E5.4"),sQuery(id+"F0.wireOp",EDGE,"E5.5"),sQuery(id+"F0.wireOp",EDGE,"E6.trimOffspring"),sQuery(id+"F0.wireOp",EDGE,"E7.trimOffspring"),sQuery(id+"F0.wireOp",EDGE,"E9.trimOffspring"),sQuery(id+"F0.wireOp",EDGE,"E10.1.0"),sQuery(id+"F0.wireOp",EDGE,"E10.1.1"),sQuery(id+"F0.wireOp",EDGE,"E10.1.2"),sQuery(id+"F0.wireOp",EDGE,"E10.1.3"),sQuery(id+"F0.wireOp",EDGE,"E10.1.5"),sQuery(id+"F0.wireOp",EDGE,"E10.1.7"),sQuery(id+"F0.wireOp",EDGE,"E10.1.8"),sQuery(id+"F0.wireOp",EDGE,"E10.1.9"),sQuery(id+"F0.wireOp",EDGE,"E10.1.10"),sQuery(id+"F0.wireOp",EDGE,"E10.1.11"),sQuery(id+"F0.wireOp",EDGE,"E10.1.12"),sQuery(id+"F0.wireOp",EDGE,"E10.1.14"),sQuery(id+"F0.wireOp",EDGE,"E10.1.15"),sQuery(id+"F0.wireOp",EDGE,"E10.1.16"),sQuery(id+"F0.wireOp",EDGE,"E10.1.18"),sQuery(id+"F0.wireOp",EDGE,"E10.1.20"),sQuery(id+"F0.wireOp",EDGE,"E10.2.0"),sQuery(id+"F0.wireOp",EDGE,"E10.2.1"),sQuery(id+"F0.wireOp",EDGE,"E10.2.2"),sQuery(id+"F0.wireOp",EDGE,"E10.2.3"),sQuery(id+"F0.wireOp",EDGE,"E10.2.5"),sQuery(id+"F0.wireOp",EDGE,"E10.2.7"),sQuery(id+"F0.wireOp",EDGE,"E10.2.8"),sQuery(id+"F0.wireOp",EDGE,"E10.2.9"),sQuery(id+"F0.wireOp",EDGE,"E10.2.10"),sQuery(id+"F0.wireOp",EDGE,"E10.2.11"),sQuery(id+"F0.wireOp",EDGE,"E10.2.12"),sQuery(id+"F0.wireOp",EDGE,"E1"),sQuery(id+"F0.wireOp",EDGE,"E10.2.14"),sQuery(id+"F0.wireOp",EDGE,"E10.2.15"),sQuery(id+"F0.wireOp",EDGE,"E10.2.16"),sQuery(id+"F0.wireOp",EDGE,"E10.2.18"),sQuery(id+"F0.wireOp",EDGE,"E10.2.20"),sQuery(id+"F0.wireOp",EDGE,"E8.trimOffspring"),sQuery(id+"F0.wireOp",EDGE,"E0"),sQuery(id+"F0.wireOp",EDGE,"E10.1.6"),sQuery(id+"F0.wireOp",EDGE,"E11"),sQuery(id+"F0.wireOp",EDGE,"E12"),sQuery(id+"F0.wireOp",EDGE,"E13.1.0"),sQuery(id+"F0.wireOp",EDGE,"E13.1.1"),sQuery(id+"F0.wireOp",EDGE,"E13.2.0"),sQuery(id+"F0.wireOp",EDGE,"E13.2.1")])]}),"instanceName":"1"}),"instanceName":"1"});
            transform(context, id + "F9", {"entities" : qUnion([Q0]), "transformType" : TransformType.TRANSLATION_3D, "dx" : 68.8 * mm, "dy" : 0 * mm, "dz" : 0 * mm, "makeCopy" : true});
        }
        {
            var Q0;
            Q0=makeQuery(id+"F9.opPattern","COPY",BODY,{"derivedFrom":makeQuery(id+"F8.opPattern","COPY",BODY,{"derivedFrom":makeQuery(id+"F7.opPattern","COPY",BODY,{"derivedFrom":makeQuery(id+"F1.opExtrude","SWEPT_BODY",BODY,{"disambiguationData":[OSD([sQuery(id+"F0.wireOp",EDGE,"E2.0"),sQuery(id+"F0.wireOp",EDGE,"E2.1"),sQuery(id+"F0.wireOp",EDGE,"E2.2"),sQuery(id+"F0.wireOp",EDGE,"E2.3"),sQuery(id+"F0.wireOp",EDGE,"E2.4"),sQuery(id+"F0.wireOp",EDGE,"E2.5"),sQuery(id+"F0.wireOp",EDGE,"E3"),sQuery(id+"F0.wireOp",EDGE,"E4"),sQuery(id+"F0.wireOp",EDGE,"E5.0"),sQuery(id+"F0.wireOp",EDGE,"E5.1"),sQuery(id+"F0.wireOp",EDGE,"E5.3"),sQuery(id+"F0.wireOp",EDGE,"E5.4"),sQuery(id+"F0.wireOp",EDGE,"E5.5"),sQuery(id+"F0.wireOp",EDGE,"E6.trimOffspring"),sQuery(id+"F0.wireOp",EDGE,"E7.trimOffspring"),sQuery(id+"F0.wireOp",EDGE,"E9.trimOffspring"),sQuery(id+"F0.wireOp",EDGE,"E10.1.0"),sQuery(id+"F0.wireOp",EDGE,"E10.1.1"),sQuery(id+"F0.wireOp",EDGE,"E10.1.2"),sQuery(id+"F0.wireOp",EDGE,"E10.1.3"),sQuery(id+"F0.wireOp",EDGE,"E10.1.5"),sQuery(id+"F0.wireOp",EDGE,"E10.1.7"),sQuery(id+"F0.wireOp",EDGE,"E10.1.8"),sQuery(id+"F0.wireOp",EDGE,"E10.1.9"),sQuery(id+"F0.wireOp",EDGE,"E10.1.10"),sQuery(id+"F0.wireOp",EDGE,"E10.1.11"),sQuery(id+"F0.wireOp",EDGE,"E10.1.12"),sQuery(id+"F0.wireOp",EDGE,"E10.1.14"),sQuery(id+"F0.wireOp",EDGE,"E10.1.15"),sQuery(id+"F0.wireOp",EDGE,"E10.1.16"),sQuery(id+"F0.wireOp",EDGE,"E10.1.18"),sQuery(id+"F0.wireOp",EDGE,"E10.1.20"),sQuery(id+"F0.wireOp",EDGE,"E10.2.0"),sQuery(id+"F0.wireOp",EDGE,"E10.2.1"),sQuery(id+"F0.wireOp",EDGE,"E10.2.2"),sQuery(id+"F0.wireOp",EDGE,"E10.2.3"),sQuery(id+"F0.wireOp",EDGE,"E10.2.5"),sQuery(id+"F0.wireOp",EDGE,"E10.2.7"),sQuery(id+"F0.wireOp",EDGE,"E10.2.8"),sQuery(id+"F0.wireOp",EDGE,"E10.2.9"),sQuery(id+"F0.wireOp",EDGE,"E10.2.10"),sQuery(id+"F0.wireOp",EDGE,"E10.2.11"),sQuery(id+"F0.wireOp",EDGE,"E10.2.12"),sQuery(id+"F0.wireOp",EDGE,"E1"),sQuery(id+"F0.wireOp",EDGE,"E10.2.14"),sQuery(id+"F0.wireOp",EDGE,"E10.2.15"),sQuery(id+"F0.wireOp",EDGE,"E10.2.16"),sQuery(id+"F0.wireOp",EDGE,"E10.2.18"),sQuery(id+"F0.wireOp",EDGE,"E10.2.20"),sQuery(id+"F0.wireOp",EDGE,"E8.trimOffspring"),sQuery(id+"F0.wireOp",EDGE,"E0"),sQuery(id+"F0.wireOp",EDGE,"E10.1.6"),sQuery(id+"F0.wireOp",EDGE,"E11"),sQuery(id+"F0.wireOp",EDGE,"E12"),sQuery(id+"F0.wireOp",EDGE,"E13.1.0"),sQuery(id+"F0.wireOp",EDGE,"E13.1.1"),sQuery(id+"F0.wireOp",EDGE,"E13.2.0"),sQuery(id+"F0.wireOp",EDGE,"E13.2.1")])]}),"instanceName":"1"}),"instanceName":"1"}),"instanceName":"1"});
            transform(context, id + "F10", {"entities" : qUnion([Q0]), "transformType" : TransformType.TRANSLATION_3D, "dx" : 53.1 * mm, "dy" : -25.6 * mm, "dz" : 0 * mm, "makeCopy" : true});
        }
        {
            var Q0;
            Q0=makeQuery(id+"F10.opPattern","COPY",BODY,{"derivedFrom":makeQuery(id+"F9.opPattern","COPY",BODY,{"derivedFrom":makeQuery(id+"F8.opPattern","COPY",BODY,{"derivedFrom":makeQuery(id+"F7.opPattern","COPY",BODY,{"derivedFrom":makeQuery(id+"F1.opExtrude","SWEPT_BODY",BODY,{"disambiguationData":[OSD([sQuery(id+"F0.wireOp",EDGE,"E2.0"),sQuery(id+"F0.wireOp",EDGE,"E2.1"),sQuery(id+"F0.wireOp",EDGE,"E2.2"),sQuery(id+"F0.wireOp",EDGE,"E2.3"),sQuery(id+"F0.wireOp",EDGE,"E2.4"),sQuery(id+"F0.wireOp",EDGE,"E2.5"),sQuery(id+"F0.wireOp",EDGE,"E3"),sQuery(id+"F0.wireOp",EDGE,"E4"),sQuery(id+"F0.wireOp",EDGE,"E5.0"),sQuery(id+"F0.wireOp",EDGE,"E5.1"),sQuery(id+"F0.wireOp",EDGE,"E5.3"),sQuery(id+"F0.wireOp",EDGE,"E5.4"),sQuery(id+"F0.wireOp",EDGE,"E5.5"),sQuery(id+"F0.wireOp",EDGE,"E6.trimOffspring"),sQuery(id+"F0.wireOp",EDGE,"E7.trimOffspring"),sQuery(id+"F0.wireOp",EDGE,"E9.trimOffspring"),sQuery(id+"F0.wireOp",EDGE,"E10.1.0"),sQuery(id+"F0.wireOp",EDGE,"E10.1.1"),sQuery(id+"F0.wireOp",EDGE,"E10.1.2"),sQuery(id+"F0.wireOp",EDGE,"E10.1.3"),sQuery(id+"F0.wireOp",EDGE,"E10.1.5"),sQuery(id+"F0.wireOp",EDGE,"E10.1.7"),sQuery(id+"F0.wireOp",EDGE,"E10.1.8"),sQuery(id+"F0.wireOp",EDGE,"E10.1.9"),sQuery(id+"F0.wireOp",EDGE,"E10.1.10"),sQuery(id+"F0.wireOp",EDGE,"E10.1.11"),sQuery(id+"F0.wireOp",EDGE,"E10.1.12"),sQuery(id+"F0.wireOp",EDGE,"E10.1.14"),sQuery(id+"F0.wireOp",EDGE,"E10.1.15"),sQuery(id+"F0.wireOp",EDGE,"E10.1.16"),sQuery(id+"F0.wireOp",EDGE,"E10.1.18"),sQuery(id+"F0.wireOp",EDGE,"E10.1.20"),sQuery(id+"F0.wireOp",EDGE,"E10.2.0"),sQuery(id+"F0.wireOp",EDGE,"E10.2.1"),sQuery(id+"F0.wireOp",EDGE,"E10.2.2"),sQuery(id+"F0.wireOp",EDGE,"E10.2.3"),sQuery(id+"F0.wireOp",EDGE,"E10.2.5"),sQuery(id+"F0.wireOp",EDGE,"E10.2.7"),sQuery(id+"F0.wireOp",EDGE,"E10.2.8"),sQuery(id+"F0.wireOp",EDGE,"E10.2.9"),sQuery(id+"F0.wireOp",EDGE,"E10.2.10"),sQuery(id+"F0.wireOp",EDGE,"E10.2.11"),sQuery(id+"F0.wireOp",EDGE,"E10.2.12"),sQuery(id+"F0.wireOp",EDGE,"E1"),sQuery(id+"F0.wireOp",EDGE,"E10.2.14"),sQuery(id+"F0.wireOp",EDGE,"E10.2.15"),sQuery(id+"F0.wireOp",EDGE,"E10.2.16"),sQuery(id+"F0.wireOp",EDGE,"E10.2.18"),sQuery(id+"F0.wireOp",EDGE,"E10.2.20"),sQuery(id+"F0.wireOp",EDGE,"E8.trimOffspring"),sQuery(id+"F0.wireOp",EDGE,"E0"),sQuery(id+"F0.wireOp",EDGE,"E10.1.6"),sQuery(id+"F0.wireOp",EDGE,"E11"),sQuery(id+"F0.wireOp",EDGE,"E12"),sQuery(id+"F0.wireOp",EDGE,"E13.1.0"),sQuery(id+"F0.wireOp",EDGE,"E13.1.1"),sQuery(id+"F0.wireOp",EDGE,"E13.2.0"),sQuery(id+"F0.wireOp",EDGE,"E13.2.1")])]}),"instanceName":"1"}),"instanceName":"1"}),"instanceName":"1"}),"instanceName":"1"});
            var Q1;
            Q1=makeQuery(id+"F10.opPattern","COPY",EDGE,{"derivedFrom":makeQuery(id+"F9.opPattern","COPY",EDGE,{"derivedFrom":makeQuery(id+"F8.opPattern","COPY",EDGE,{"derivedFrom":makeQuery(id+"F7.opPattern","COPY",EDGE,{"derivedFrom":makeQuery(id+"F1.opExtrude","CAP_EDGE",EDGE,{"disambiguationData":[OSD([sQuery(id+"F0.wireOp",EDGE,"E1")])],"isStart":false}),"instanceName":"1"}),"instanceName":"1"}),"instanceName":"1"}),"instanceName":"1"});
            transform(context, id + "F11", {"entities" : qUnion([Q0]), "transformType" : TransformType.ROTATION, "transformAxis" : qUnion([Q1]), "angle" : 55 * degree, "oppositeDirection" : true, "makeCopy" : false});
        }
        {
            var Q0;
            Q0=makeQuery(id+"F10.opPattern","COPY",BODY,{"derivedFrom":makeQuery(id+"F9.opPattern","COPY",BODY,{"derivedFrom":makeQuery(id+"F8.opPattern","COPY",BODY,{"derivedFrom":makeQuery(id+"F7.opPattern","COPY",BODY,{"derivedFrom":makeQuery(id+"F1.opExtrude","SWEPT_BODY",BODY,{"disambiguationData":[OSD([sQuery(id+"F0.wireOp",EDGE,"E2.0"),sQuery(id+"F0.wireOp",EDGE,"E2.1"),sQuery(id+"F0.wireOp",EDGE,"E2.2"),sQuery(id+"F0.wireOp",EDGE,"E2.3"),sQuery(id+"F0.wireOp",EDGE,"E2.4"),sQuery(id+"F0.wireOp",EDGE,"E2.5"),sQuery(id+"F0.wireOp",EDGE,"E3"),sQuery(id+"F0.wireOp",EDGE,"E4"),sQuery(id+"F0.wireOp",EDGE,"E5.0"),sQuery(id+"F0.wireOp",EDGE,"E5.1"),sQuery(id+"F0.wireOp",EDGE,"E5.3"),sQuery(id+"F0.wireOp",EDGE,"E5.4"),sQuery(id+"F0.wireOp",EDGE,"E5.5"),sQuery(id+"F0.wireOp",EDGE,"E6.trimOffspring"),sQuery(id+"F0.wireOp",EDGE,"E7.trimOffspring"),sQuery(id+"F0.wireOp",EDGE,"E9.trimOffspring"),sQuery(id+"F0.wireOp",EDGE,"E10.1.0"),sQuery(id+"F0.wireOp",EDGE,"E10.1.1"),sQuery(id+"F0.wireOp",EDGE,"E10.1.2"),sQuery(id+"F0.wireOp",EDGE,"E10.1.3"),sQuery(id+"F0.wireOp",EDGE,"E10.1.5"),sQuery(id+"F0.wireOp",EDGE,"E10.1.7"),sQuery(id+"F0.wireOp",EDGE,"E10.1.8"),sQuery(id+"F0.wireOp",EDGE,"E10.1.9"),sQuery(id+"F0.wireOp",EDGE,"E10.1.10"),sQuery(id+"F0.wireOp",EDGE,"E10.1.11"),sQuery(id+"F0.wireOp",EDGE,"E10.1.12"),sQuery(id+"F0.wireOp",EDGE,"E10.1.14"),sQuery(id+"F0.wireOp",EDGE,"E10.1.15"),sQuery(id+"F0.wireOp",EDGE,"E10.1.16"),sQuery(id+"F0.wireOp",EDGE,"E10.1.18"),sQuery(id+"F0.wireOp",EDGE,"E10.1.20"),sQuery(id+"F0.wireOp",EDGE,"E10.2.0"),sQuery(id+"F0.wireOp",EDGE,"E10.2.1"),sQuery(id+"F0.wireOp",EDGE,"E10.2.2"),sQuery(id+"F0.wireOp",EDGE,"E10.2.3"),sQuery(id+"F0.wireOp",EDGE,"E10.2.5"),sQuery(id+"F0.wireOp",EDGE,"E10.2.7"),sQuery(id+"F0.wireOp",EDGE,"E10.2.8"),sQuery(id+"F0.wireOp",EDGE,"E10.2.9"),sQuery(id+"F0.wireOp",EDGE,"E10.2.10"),sQuery(id+"F0.wireOp",EDGE,"E10.2.11"),sQuery(id+"F0.wireOp",EDGE,"E10.2.12"),sQuery(id+"F0.wireOp",EDGE,"E1"),sQuery(id+"F0.wireOp",EDGE,"E10.2.14"),sQuery(id+"F0.wireOp",EDGE,"E10.2.15"),sQuery(id+"F0.wireOp",EDGE,"E10.2.16"),sQuery(id+"F0.wireOp",EDGE,"E10.2.18"),sQuery(id+"F0.wireOp",EDGE,"E10.2.20"),sQuery(id+"F0.wireOp",EDGE,"E8.trimOffspring"),sQuery(id+"F0.wireOp",EDGE,"E0"),sQuery(id+"F0.wireOp",EDGE,"E10.1.6"),sQuery(id+"F0.wireOp",EDGE,"E11"),sQuery(id+"F0.wireOp",EDGE,"E12"),sQuery(id+"F0.wireOp",EDGE,"E13.1.0"),sQuery(id+"F0.wireOp",EDGE,"E13.1.1"),sQuery(id+"F0.wireOp",EDGE,"E13.2.0"),sQuery(id+"F0.wireOp",EDGE,"E13.2.1")])]}),"instanceName":"1"}),"instanceName":"1"}),"instanceName":"1"}),"instanceName":"1"});
            transform(context, id + "F12", {"entities" : qUnion([Q0]), "transformType" : TransformType.TRANSLATION_3D, "dx" : 4.8 * mm, "dy" : 6 * mm, "dz" : 0 * mm, "makeCopy" : false});
        }
        {
            var Q0;
            Q0=makeQuery(id+"F1.opExtrude","SWEPT_BODY",BODY,{"disambiguationData":[OSD([sQuery(id+"F0.wireOp",EDGE,"E2.0"),sQuery(id+"F0.wireOp",EDGE,"E2.1"),sQuery(id+"F0.wireOp",EDGE,"E2.2"),sQuery(id+"F0.wireOp",EDGE,"E2.3"),sQuery(id+"F0.wireOp",EDGE,"E2.4"),sQuery(id+"F0.wireOp",EDGE,"E2.5"),sQuery(id+"F0.wireOp",EDGE,"E3"),sQuery(id+"F0.wireOp",EDGE,"E4"),sQuery(id+"F0.wireOp",EDGE,"E5.0"),sQuery(id+"F0.wireOp",EDGE,"E5.1"),sQuery(id+"F0.wireOp",EDGE,"E5.3"),sQuery(id+"F0.wireOp",EDGE,"E5.4"),sQuery(id+"F0.wireOp",EDGE,"E5.5"),sQuery(id+"F0.wireOp",EDGE,"E6.trimOffspring"),sQuery(id+"F0.wireOp",EDGE,"E7.trimOffspring"),sQuery(id+"F0.wireOp",EDGE,"E9.trimOffspring"),sQuery(id+"F0.wireOp",EDGE,"E10.1.0"),sQuery(id+"F0.wireOp",EDGE,"E10.1.1"),sQuery(id+"F0.wireOp",EDGE,"E10.1.2"),sQuery(id+"F0.wireOp",EDGE,"E10.1.3"),sQuery(id+"F0.wireOp",EDGE,"E10.1.5"),sQuery(id+"F0.wireOp",EDGE,"E10.1.7"),sQuery(id+"F0.wireOp",EDGE,"E10.1.8"),sQuery(id+"F0.wireOp",EDGE,"E10.1.9"),sQuery(id+"F0.wireOp",EDGE,"E10.1.10"),sQuery(id+"F0.wireOp",EDGE,"E10.1.11"),sQuery(id+"F0.wireOp",EDGE,"E10.1.12"),sQuery(id+"F0.wireOp",EDGE,"E10.1.14"),sQuery(id+"F0.wireOp",EDGE,"E10.1.15"),sQuery(id+"F0.wireOp",EDGE,"E10.1.16"),sQuery(id+"F0.wireOp",EDGE,"E10.1.18"),sQuery(id+"F0.wireOp",EDGE,"E10.1.20"),sQuery(id+"F0.wireOp",EDGE,"E10.2.0"),sQuery(id+"F0.wireOp",EDGE,"E10.2.1"),sQuery(id+"F0.wireOp",EDGE,"E10.2.2"),sQuery(id+"F0.wireOp",EDGE,"E10.2.3"),sQuery(id+"F0.wireOp",EDGE,"E10.2.5"),sQuery(id+"F0.wireOp",EDGE,"E10.2.7"),sQuery(id+"F0.wireOp",EDGE,"E10.2.8"),sQuery(id+"F0.wireOp",EDGE,"E10.2.9"),sQuery(id+"F0.wireOp",EDGE,"E10.2.10"),sQuery(id+"F0.wireOp",EDGE,"E10.2.11"),sQuery(id+"F0.wireOp",EDGE,"E10.2.12"),sQuery(id+"F0.wireOp",EDGE,"E1"),sQuery(id+"F0.wireOp",EDGE,"E10.2.14"),sQuery(id+"F0.wireOp",EDGE,"E10.2.15"),sQuery(id+"F0.wireOp",EDGE,"E10.2.16"),sQuery(id+"F0.wireOp",EDGE,"E10.2.18"),sQuery(id+"F0.wireOp",EDGE,"E10.2.20"),sQuery(id+"F0.wireOp",EDGE,"E8.trimOffspring"),sQuery(id+"F0.wireOp",EDGE,"E0"),sQuery(id+"F0.wireOp",EDGE,"E10.1.6"),sQuery(id+"F0.wireOp",EDGE,"E11"),sQuery(id+"F0.wireOp",EDGE,"E12"),sQuery(id+"F0.wireOp",EDGE,"E13.1.0"),sQuery(id+"F0.wireOp",EDGE,"E13.1.1"),sQuery(id+"F0.wireOp",EDGE,"E13.2.0"),sQuery(id+"F0.wireOp",EDGE,"E13.2.1")])]});
            transform(context, id + "F13", {"entities" : qUnion([Q0]), "transformType" : TransformType.TRANSLATION_3D, "dx" : 36.7 * mm, "dy" : -60.6 * mm, "dz" : 0 * mm, "makeCopy" : true});
        }
        {
            var Q0;
            Q0=makeQuery(id+"F13.opPattern","COPY",BODY,{"derivedFrom":makeQuery(id+"F1.opExtrude","SWEPT_BODY",BODY,{"disambiguationData":[OSD([sQuery(id+"F0.wireOp",EDGE,"E2.0"),sQuery(id+"F0.wireOp",EDGE,"E2.1"),sQuery(id+"F0.wireOp",EDGE,"E2.2"),sQuery(id+"F0.wireOp",EDGE,"E2.3"),sQuery(id+"F0.wireOp",EDGE,"E2.4"),sQuery(id+"F0.wireOp",EDGE,"E2.5"),sQuery(id+"F0.wireOp",EDGE,"E3"),sQuery(id+"F0.wireOp",EDGE,"E4"),sQuery(id+"F0.wireOp",EDGE,"E5.0"),sQuery(id+"F0.wireOp",EDGE,"E5.1"),sQuery(id+"F0.wireOp",EDGE,"E5.3"),sQuery(id+"F0.wireOp",EDGE,"E5.4"),sQuery(id+"F0.wireOp",EDGE,"E5.5"),sQuery(id+"F0.wireOp",EDGE,"E6.trimOffspring"),sQuery(id+"F0.wireOp",EDGE,"E7.trimOffspring"),sQuery(id+"F0.wireOp",EDGE,"E9.trimOffspring"),sQuery(id+"F0.wireOp",EDGE,"E10.1.0"),sQuery(id+"F0.wireOp",EDGE,"E10.1.1"),sQuery(id+"F0.wireOp",EDGE,"E10.1.2"),sQuery(id+"F0.wireOp",EDGE,"E10.1.3"),sQuery(id+"F0.wireOp",EDGE,"E10.1.5"),sQuery(id+"F0.wireOp",EDGE,"E10.1.7"),sQuery(id+"F0.wireOp",EDGE,"E10.1.8"),sQuery(id+"F0.wireOp",EDGE,"E10.1.9"),sQuery(id+"F0.wireOp",EDGE,"E10.1.10"),sQuery(id+"F0.wireOp",EDGE,"E10.1.11"),sQuery(id+"F0.wireOp",EDGE,"E10.1.12"),sQuery(id+"F0.wireOp",EDGE,"E10.1.14"),sQuery(id+"F0.wireOp",EDGE,"E10.1.15"),sQuery(id+"F0.wireOp",EDGE,"E10.1.16"),sQuery(id+"F0.wireOp",EDGE,"E10.1.18"),sQuery(id+"F0.wireOp",EDGE,"E10.1.20"),sQuery(id+"F0.wireOp",EDGE,"E10.2.0"),sQuery(id+"F0.wireOp",EDGE,"E10.2.1"),sQuery(id+"F0.wireOp",EDGE,"E10.2.2"),sQuery(id+"F0.wireOp",EDGE,"E10.2.3"),sQuery(id+"F0.wireOp",EDGE,"E10.2.5"),sQuery(id+"F0.wireOp",EDGE,"E10.2.7"),sQuery(id+"F0.wireOp",EDGE,"E10.2.8"),sQuery(id+"F0.wireOp",EDGE,"E10.2.9"),sQuery(id+"F0.wireOp",EDGE,"E10.2.10"),sQuery(id+"F0.wireOp",EDGE,"E10.2.11"),sQuery(id+"F0.wireOp",EDGE,"E10.2.12"),sQuery(id+"F0.wireOp",EDGE,"E1"),sQuery(id+"F0.wireOp",EDGE,"E10.2.14"),sQuery(id+"F0.wireOp",EDGE,"E10.2.15"),sQuery(id+"F0.wireOp",EDGE,"E10.2.16"),sQuery(id+"F0.wireOp",EDGE,"E10.2.18"),sQuery(id+"F0.wireOp",EDGE,"E10.2.20"),sQuery(id+"F0.wireOp",EDGE,"E8.trimOffspring"),sQuery(id+"F0.wireOp",EDGE,"E0"),sQuery(id+"F0.wireOp",EDGE,"E10.1.6"),sQuery(id+"F0.wireOp",EDGE,"E11"),sQuery(id+"F0.wireOp",EDGE,"E12"),sQuery(id+"F0.wireOp",EDGE,"E13.1.0"),sQuery(id+"F0.wireOp",EDGE,"E13.1.1"),sQuery(id+"F0.wireOp",EDGE,"E13.2.0"),sQuery(id+"F0.wireOp",EDGE,"E13.2.1")])]}),"instanceName":"1"});
            var Q1;
            Q1=makeQuery(id+"F13.opPattern","COPY",EDGE,{"derivedFrom":makeQuery(id+"F1.opExtrude","CAP_EDGE",EDGE,{"disambiguationData":[OSD([sQuery(id+"F0.wireOp",EDGE,"E1")])],"isStart":false}),"instanceName":"1"});
            transform(context, id + "F14", {"entities" : qUnion([Q0]), "transformType" : TransformType.ROTATION, "transformAxis" : qUnion([Q1]), "angle" : 45 * degree, "oppositeDirection" : true, "makeCopy" : false});
        }
        {
            var Q0;
            Q0=makeQuery(id+"F13.opPattern","COPY",BODY,{"derivedFrom":makeQuery(id+"F1.opExtrude","SWEPT_BODY",BODY,{"disambiguationData":[OSD([sQuery(id+"F0.wireOp",EDGE,"E2.0"),sQuery(id+"F0.wireOp",EDGE,"E2.1"),sQuery(id+"F0.wireOp",EDGE,"E2.2"),sQuery(id+"F0.wireOp",EDGE,"E2.3"),sQuery(id+"F0.wireOp",EDGE,"E2.4"),sQuery(id+"F0.wireOp",EDGE,"E2.5"),sQuery(id+"F0.wireOp",EDGE,"E3"),sQuery(id+"F0.wireOp",EDGE,"E4"),sQuery(id+"F0.wireOp",EDGE,"E5.0"),sQuery(id+"F0.wireOp",EDGE,"E5.1"),sQuery(id+"F0.wireOp",EDGE,"E5.3"),sQuery(id+"F0.wireOp",EDGE,"E5.4"),sQuery(id+"F0.wireOp",EDGE,"E5.5"),sQuery(id+"F0.wireOp",EDGE,"E6.trimOffspring"),sQuery(id+"F0.wireOp",EDGE,"E7.trimOffspring"),sQuery(id+"F0.wireOp",EDGE,"E9.trimOffspring"),sQuery(id+"F0.wireOp",EDGE,"E10.1.0"),sQuery(id+"F0.wireOp",EDGE,"E10.1.1"),sQuery(id+"F0.wireOp",EDGE,"E10.1.2"),sQuery(id+"F0.wireOp",EDGE,"E10.1.3"),sQuery(id+"F0.wireOp",EDGE,"E10.1.5"),sQuery(id+"F0.wireOp",EDGE,"E10.1.7"),sQuery(id+"F0.wireOp",EDGE,"E10.1.8"),sQuery(id+"F0.wireOp",EDGE,"E10.1.9"),sQuery(id+"F0.wireOp",EDGE,"E10.1.10"),sQuery(id+"F0.wireOp",EDGE,"E10.1.11"),sQuery(id+"F0.wireOp",EDGE,"E10.1.12"),sQuery(id+"F0.wireOp",EDGE,"E10.1.14"),sQuery(id+"F0.wireOp",EDGE,"E10.1.15"),sQuery(id+"F0.wireOp",EDGE,"E10.1.16"),sQuery(id+"F0.wireOp",EDGE,"E10.1.18"),sQuery(id+"F0.wireOp",EDGE,"E10.1.20"),sQuery(id+"F0.wireOp",EDGE,"E10.2.0"),sQuery(id+"F0.wireOp",EDGE,"E10.2.1"),sQuery(id+"F0.wireOp",EDGE,"E10.2.2"),sQuery(id+"F0.wireOp",EDGE,"E10.2.3"),sQuery(id+"F0.wireOp",EDGE,"E10.2.5"),sQuery(id+"F0.wireOp",EDGE,"E10.2.7"),sQuery(id+"F0.wireOp",EDGE,"E10.2.8"),sQuery(id+"F0.wireOp",EDGE,"E10.2.9"),sQuery(id+"F0.wireOp",EDGE,"E10.2.10"),sQuery(id+"F0.wireOp",EDGE,"E10.2.11"),sQuery(id+"F0.wireOp",EDGE,"E10.2.12"),sQuery(id+"F0.wireOp",EDGE,"E1"),sQuery(id+"F0.wireOp",EDGE,"E10.2.14"),sQuery(id+"F0.wireOp",EDGE,"E10.2.15"),sQuery(id+"F0.wireOp",EDGE,"E10.2.16"),sQuery(id+"F0.wireOp",EDGE,"E10.2.18"),sQuery(id+"F0.wireOp",EDGE,"E10.2.20"),sQuery(id+"F0.wireOp",EDGE,"E8.trimOffspring"),sQuery(id+"F0.wireOp",EDGE,"E0"),sQuery(id+"F0.wireOp",EDGE,"E10.1.6"),sQuery(id+"F0.wireOp",EDGE,"E11"),sQuery(id+"F0.wireOp",EDGE,"E12"),sQuery(id+"F0.wireOp",EDGE,"E13.1.0"),sQuery(id+"F0.wireOp",EDGE,"E13.1.1"),sQuery(id+"F0.wireOp",EDGE,"E13.2.0"),sQuery(id+"F0.wireOp",EDGE,"E13.2.1")])]}),"instanceName":"1"});
            transform(context, id + "F15", {"entities" : qUnion([Q0]), "transformType" : TransformType.TRANSLATION_3D, "dx" : -10.1 * mm, "dy" : 10.3 * mm, "dz" : 0 * mm, "makeCopy" : false});
        }
        {
            var Q0;
            Q0=makeQuery(id+"F13.opPattern","COPY",BODY,{"derivedFrom":makeQuery(id+"F1.opExtrude","SWEPT_BODY",BODY,{"disambiguationData":[OSD([sQuery(id+"F0.wireOp",EDGE,"E2.0"),sQuery(id+"F0.wireOp",EDGE,"E2.1"),sQuery(id+"F0.wireOp",EDGE,"E2.2"),sQuery(id+"F0.wireOp",EDGE,"E2.3"),sQuery(id+"F0.wireOp",EDGE,"E2.4"),sQuery(id+"F0.wireOp",EDGE,"E2.5"),sQuery(id+"F0.wireOp",EDGE,"E3"),sQuery(id+"F0.wireOp",EDGE,"E4"),sQuery(id+"F0.wireOp",EDGE,"E5.0"),sQuery(id+"F0.wireOp",EDGE,"E5.1"),sQuery(id+"F0.wireOp",EDGE,"E5.3"),sQuery(id+"F0.wireOp",EDGE,"E5.4"),sQuery(id+"F0.wireOp",EDGE,"E5.5"),sQuery(id+"F0.wireOp",EDGE,"E6.trimOffspring"),sQuery(id+"F0.wireOp",EDGE,"E7.trimOffspring"),sQuery(id+"F0.wireOp",EDGE,"E9.trimOffspring"),sQuery(id+"F0.wireOp",EDGE,"E10.1.0"),sQuery(id+"F0.wireOp",EDGE,"E10.1.1"),sQuery(id+"F0.wireOp",EDGE,"E10.1.2"),sQuery(id+"F0.wireOp",EDGE,"E10.1.3"),sQuery(id+"F0.wireOp",EDGE,"E10.1.5"),sQuery(id+"F0.wireOp",EDGE,"E10.1.7"),sQuery(id+"F0.wireOp",EDGE,"E10.1.8"),sQuery(id+"F0.wireOp",EDGE,"E10.1.9"),sQuery(id+"F0.wireOp",EDGE,"E10.1.10"),sQuery(id+"F0.wireOp",EDGE,"E10.1.11"),sQuery(id+"F0.wireOp",EDGE,"E10.1.12"),sQuery(id+"F0.wireOp",EDGE,"E10.1.14"),sQuery(id+"F0.wireOp",EDGE,"E10.1.15"),sQuery(id+"F0.wireOp",EDGE,"E10.1.16"),sQuery(id+"F0.wireOp",EDGE,"E10.1.18"),sQuery(id+"F0.wireOp",EDGE,"E10.1.20"),sQuery(id+"F0.wireOp",EDGE,"E10.2.0"),sQuery(id+"F0.wireOp",EDGE,"E10.2.1"),sQuery(id+"F0.wireOp",EDGE,"E10.2.2"),sQuery(id+"F0.wireOp",EDGE,"E10.2.3"),sQuery(id+"F0.wireOp",EDGE,"E10.2.5"),sQuery(id+"F0.wireOp",EDGE,"E10.2.7"),sQuery(id+"F0.wireOp",EDGE,"E10.2.8"),sQuery(id+"F0.wireOp",EDGE,"E10.2.9"),sQuery(id+"F0.wireOp",EDGE,"E10.2.10"),sQuery(id+"F0.wireOp",EDGE,"E10.2.11"),sQuery(id+"F0.wireOp",EDGE,"E10.2.12"),sQuery(id+"F0.wireOp",EDGE,"E1"),sQuery(id+"F0.wireOp",EDGE,"E10.2.14"),sQuery(id+"F0.wireOp",EDGE,"E10.2.15"),sQuery(id+"F0.wireOp",EDGE,"E10.2.16"),sQuery(id+"F0.wireOp",EDGE,"E10.2.18"),sQuery(id+"F0.wireOp",EDGE,"E10.2.20"),sQuery(id+"F0.wireOp",EDGE,"E8.trimOffspring"),sQuery(id+"F0.wireOp",EDGE,"E0"),sQuery(id+"F0.wireOp",EDGE,"E10.1.6"),sQuery(id+"F0.wireOp",EDGE,"E11"),sQuery(id+"F0.wireOp",EDGE,"E12"),sQuery(id+"F0.wireOp",EDGE,"E13.1.0"),sQuery(id+"F0.wireOp",EDGE,"E13.1.1"),sQuery(id+"F0.wireOp",EDGE,"E13.2.0"),sQuery(id+"F0.wireOp",EDGE,"E13.2.1")])]}),"instanceName":"1"});
            var Q1;
            Q1=makeQuery(id+"F13.opPattern","COPY",EDGE,{"derivedFrom":makeQuery(id+"F1.opExtrude","CAP_EDGE",EDGE,{"disambiguationData":[OSD([sQuery(id+"F0.wireOp",EDGE,"E1")])],"isStart":false}),"instanceName":"1"});
            transform(context, id + "F16", {"entities" : qUnion([Q0]), "transformType" : TransformType.ROTATION, "transformAxis" : qUnion([Q1]), "angle" : 15 * degree, "oppositeDirection" : true, "makeCopy" : false});
        }
        {
            var Q0;
            Q0=makeQuery(id+"F13.opPattern","COPY",BODY,{"derivedFrom":makeQuery(id+"F1.opExtrude","SWEPT_BODY",BODY,{"disambiguationData":[OSD([sQuery(id+"F0.wireOp",EDGE,"E2.0"),sQuery(id+"F0.wireOp",EDGE,"E2.1"),sQuery(id+"F0.wireOp",EDGE,"E2.2"),sQuery(id+"F0.wireOp",EDGE,"E2.3"),sQuery(id+"F0.wireOp",EDGE,"E2.4"),sQuery(id+"F0.wireOp",EDGE,"E2.5"),sQuery(id+"F0.wireOp",EDGE,"E3"),sQuery(id+"F0.wireOp",EDGE,"E4"),sQuery(id+"F0.wireOp",EDGE,"E5.0"),sQuery(id+"F0.wireOp",EDGE,"E5.1"),sQuery(id+"F0.wireOp",EDGE,"E5.3"),sQuery(id+"F0.wireOp",EDGE,"E5.4"),sQuery(id+"F0.wireOp",EDGE,"E5.5"),sQuery(id+"F0.wireOp",EDGE,"E6.trimOffspring"),sQuery(id+"F0.wireOp",EDGE,"E7.trimOffspring"),sQuery(id+"F0.wireOp",EDGE,"E9.trimOffspring"),sQuery(id+"F0.wireOp",EDGE,"E10.1.0"),sQuery(id+"F0.wireOp",EDGE,"E10.1.1"),sQuery(id+"F0.wireOp",EDGE,"E10.1.2"),sQuery(id+"F0.wireOp",EDGE,"E10.1.3"),sQuery(id+"F0.wireOp",EDGE,"E10.1.5"),sQuery(id+"F0.wireOp",EDGE,"E10.1.7"),sQuery(id+"F0.wireOp",EDGE,"E10.1.8"),sQuery(id+"F0.wireOp",EDGE,"E10.1.9"),sQuery(id+"F0.wireOp",EDGE,"E10.1.10"),sQuery(id+"F0.wireOp",EDGE,"E10.1.11"),sQuery(id+"F0.wireOp",EDGE,"E10.1.12"),sQuery(id+"F0.wireOp",EDGE,"E10.1.14"),sQuery(id+"F0.wireOp",EDGE,"E10.1.15"),sQuery(id+"F0.wireOp",EDGE,"E10.1.16"),sQuery(id+"F0.wireOp",EDGE,"E10.1.18"),sQuery(id+"F0.wireOp",EDGE,"E10.1.20"),sQuery(id+"F0.wireOp",EDGE,"E10.2.0"),sQuery(id+"F0.wireOp",EDGE,"E10.2.1"),sQuery(id+"F0.wireOp",EDGE,"E10.2.2"),sQuery(id+"F0.wireOp",EDGE,"E10.2.3"),sQuery(id+"F0.wireOp",EDGE,"E10.2.5"),sQuery(id+"F0.wireOp",EDGE,"E10.2.7"),sQuery(id+"F0.wireOp",EDGE,"E10.2.8"),sQuery(id+"F0.wireOp",EDGE,"E10.2.9"),sQuery(id+"F0.wireOp",EDGE,"E10.2.10"),sQuery(id+"F0.wireOp",EDGE,"E10.2.11"),sQuery(id+"F0.wireOp",EDGE,"E10.2.12"),sQuery(id+"F0.wireOp",EDGE,"E1"),sQuery(id+"F0.wireOp",EDGE,"E10.2.14"),sQuery(id+"F0.wireOp",EDGE,"E10.2.15"),sQuery(id+"F0.wireOp",EDGE,"E10.2.16"),sQuery(id+"F0.wireOp",EDGE,"E10.2.18"),sQuery(id+"F0.wireOp",EDGE,"E10.2.20"),sQuery(id+"F0.wireOp",EDGE,"E8.trimOffspring"),sQuery(id+"F0.wireOp",EDGE,"E0"),sQuery(id+"F0.wireOp",EDGE,"E10.1.6"),sQuery(id+"F0.wireOp",EDGE,"E11"),sQuery(id+"F0.wireOp",EDGE,"E12"),sQuery(id+"F0.wireOp",EDGE,"E13.1.0"),sQuery(id+"F0.wireOp",EDGE,"E13.1.1"),sQuery(id+"F0.wireOp",EDGE,"E13.2.0"),sQuery(id+"F0.wireOp",EDGE,"E13.2.1")])]}),"instanceName":"1"});
            transform(context, id + "F17", {"entities" : qUnion([Q0]), "transformType" : TransformType.TRANSLATION_3D, "dx" : 1.6 * mm, "dy" : -3.2 * mm, "dz" : 0 * mm, "makeCopy" : false});
        }
        {
            var Q0;
            Q0=makeQuery(id+"F13.opPattern","COPY",BODY,{"derivedFrom":makeQuery(id+"F1.opExtrude","SWEPT_BODY",BODY,{"disambiguationData":[OSD([sQuery(id+"F0.wireOp",EDGE,"E2.0"),sQuery(id+"F0.wireOp",EDGE,"E2.1"),sQuery(id+"F0.wireOp",EDGE,"E2.2"),sQuery(id+"F0.wireOp",EDGE,"E2.3"),sQuery(id+"F0.wireOp",EDGE,"E2.4"),sQuery(id+"F0.wireOp",EDGE,"E2.5"),sQuery(id+"F0.wireOp",EDGE,"E3"),sQuery(id+"F0.wireOp",EDGE,"E4"),sQuery(id+"F0.wireOp",EDGE,"E5.0"),sQuery(id+"F0.wireOp",EDGE,"E5.1"),sQuery(id+"F0.wireOp",EDGE,"E5.3"),sQuery(id+"F0.wireOp",EDGE,"E5.4"),sQuery(id+"F0.wireOp",EDGE,"E5.5"),sQuery(id+"F0.wireOp",EDGE,"E6.trimOffspring"),sQuery(id+"F0.wireOp",EDGE,"E7.trimOffspring"),sQuery(id+"F0.wireOp",EDGE,"E9.trimOffspring"),sQuery(id+"F0.wireOp",EDGE,"E10.1.0"),sQuery(id+"F0.wireOp",EDGE,"E10.1.1"),sQuery(id+"F0.wireOp",EDGE,"E10.1.2"),sQuery(id+"F0.wireOp",EDGE,"E10.1.3"),sQuery(id+"F0.wireOp",EDGE,"E10.1.5"),sQuery(id+"F0.wireOp",EDGE,"E10.1.7"),sQuery(id+"F0.wireOp",EDGE,"E10.1.8"),sQuery(id+"F0.wireOp",EDGE,"E10.1.9"),sQuery(id+"F0.wireOp",EDGE,"E10.1.10"),sQuery(id+"F0.wireOp",EDGE,"E10.1.11"),sQuery(id+"F0.wireOp",EDGE,"E10.1.12"),sQuery(id+"F0.wireOp",EDGE,"E10.1.14"),sQuery(id+"F0.wireOp",EDGE,"E10.1.15"),sQuery(id+"F0.wireOp",EDGE,"E10.1.16"),sQuery(id+"F0.wireOp",EDGE,"E10.1.18"),sQuery(id+"F0.wireOp",EDGE,"E10.1.20"),sQuery(id+"F0.wireOp",EDGE,"E10.2.0"),sQuery(id+"F0.wireOp",EDGE,"E10.2.1"),sQuery(id+"F0.wireOp",EDGE,"E10.2.2"),sQuery(id+"F0.wireOp",EDGE,"E10.2.3"),sQuery(id+"F0.wireOp",EDGE,"E10.2.5"),sQuery(id+"F0.wireOp",EDGE,"E10.2.7"),sQuery(id+"F0.wireOp",EDGE,"E10.2.8"),sQuery(id+"F0.wireOp",EDGE,"E10.2.9"),sQuery(id+"F0.wireOp",EDGE,"E10.2.10"),sQuery(id+"F0.wireOp",EDGE,"E10.2.11"),sQuery(id+"F0.wireOp",EDGE,"E10.2.12"),sQuery(id+"F0.wireOp",EDGE,"E1"),sQuery(id+"F0.wireOp",EDGE,"E10.2.14"),sQuery(id+"F0.wireOp",EDGE,"E10.2.15"),sQuery(id+"F0.wireOp",EDGE,"E10.2.16"),sQuery(id+"F0.wireOp",EDGE,"E10.2.18"),sQuery(id+"F0.wireOp",EDGE,"E10.2.20"),sQuery(id+"F0.wireOp",EDGE,"E8.trimOffspring"),sQuery(id+"F0.wireOp",EDGE,"E0"),sQuery(id+"F0.wireOp",EDGE,"E10.1.6"),sQuery(id+"F0.wireOp",EDGE,"E11"),sQuery(id+"F0.wireOp",EDGE,"E12"),sQuery(id+"F0.wireOp",EDGE,"E13.1.0"),sQuery(id+"F0.wireOp",EDGE,"E13.1.1"),sQuery(id+"F0.wireOp",EDGE,"E13.2.0"),sQuery(id+"F0.wireOp",EDGE,"E13.2.1")])]}),"instanceName":"1"});
            transform(context, id + "F18", {"entities" : qUnion([Q0]), "transformType" : TransformType.TRANSLATION_3D, "dx" : 69.1 * mm, "dy" : 0 * mm, "dz" : 0 * mm, "makeCopy" : true});
        }
        {
            var Q0;
            Q0=makeQuery(id+"F18.opPattern","COPY",BODY,{"derivedFrom":makeQuery(id+"F13.opPattern","COPY",BODY,{"derivedFrom":makeQuery(id+"F1.opExtrude","SWEPT_BODY",BODY,{"disambiguationData":[OSD([sQuery(id+"F0.wireOp",EDGE,"E2.0"),sQuery(id+"F0.wireOp",EDGE,"E2.1"),sQuery(id+"F0.wireOp",EDGE,"E2.2"),sQuery(id+"F0.wireOp",EDGE,"E2.3"),sQuery(id+"F0.wireOp",EDGE,"E2.4"),sQuery(id+"F0.wireOp",EDGE,"E2.5"),sQuery(id+"F0.wireOp",EDGE,"E3"),sQuery(id+"F0.wireOp",EDGE,"E4"),sQuery(id+"F0.wireOp",EDGE,"E5.0"),sQuery(id+"F0.wireOp",EDGE,"E5.1"),sQuery(id+"F0.wireOp",EDGE,"E5.3"),sQuery(id+"F0.wireOp",EDGE,"E5.4"),sQuery(id+"F0.wireOp",EDGE,"E5.5"),sQuery(id+"F0.wireOp",EDGE,"E6.trimOffspring"),sQuery(id+"F0.wireOp",EDGE,"E7.trimOffspring"),sQuery(id+"F0.wireOp",EDGE,"E9.trimOffspring"),sQuery(id+"F0.wireOp",EDGE,"E10.1.0"),sQuery(id+"F0.wireOp",EDGE,"E10.1.1"),sQuery(id+"F0.wireOp",EDGE,"E10.1.2"),sQuery(id+"F0.wireOp",EDGE,"E10.1.3"),sQuery(id+"F0.wireOp",EDGE,"E10.1.5"),sQuery(id+"F0.wireOp",EDGE,"E10.1.7"),sQuery(id+"F0.wireOp",EDGE,"E10.1.8"),sQuery(id+"F0.wireOp",EDGE,"E10.1.9"),sQuery(id+"F0.wireOp",EDGE,"E10.1.10"),sQuery(id+"F0.wireOp",EDGE,"E10.1.11"),sQuery(id+"F0.wireOp",EDGE,"E10.1.12"),sQuery(id+"F0.wireOp",EDGE,"E10.1.14"),sQuery(id+"F0.wireOp",EDGE,"E10.1.15"),sQuery(id+"F0.wireOp",EDGE,"E10.1.16"),sQuery(id+"F0.wireOp",EDGE,"E10.1.18"),sQuery(id+"F0.wireOp",EDGE,"E10.1.20"),sQuery(id+"F0.wireOp",EDGE,"E10.2.0"),sQuery(id+"F0.wireOp",EDGE,"E10.2.1"),sQuery(id+"F0.wireOp",EDGE,"E10.2.2"),sQuery(id+"F0.wireOp",EDGE,"E10.2.3"),sQuery(id+"F0.wireOp",EDGE,"E10.2.5"),sQuery(id+"F0.wireOp",EDGE,"E10.2.7"),sQuery(id+"F0.wireOp",EDGE,"E10.2.8"),sQuery(id+"F0.wireOp",EDGE,"E10.2.9"),sQuery(id+"F0.wireOp",EDGE,"E10.2.10"),sQuery(id+"F0.wireOp",EDGE,"E10.2.11"),sQuery(id+"F0.wireOp",EDGE,"E10.2.12"),sQuery(id+"F0.wireOp",EDGE,"E1"),sQuery(id+"F0.wireOp",EDGE,"E10.2.14"),sQuery(id+"F0.wireOp",EDGE,"E10.2.15"),sQuery(id+"F0.wireOp",EDGE,"E10.2.16"),sQuery(id+"F0.wireOp",EDGE,"E10.2.18"),sQuery(id+"F0.wireOp",EDGE,"E10.2.20"),sQuery(id+"F0.wireOp",EDGE,"E8.trimOffspring"),sQuery(id+"F0.wireOp",EDGE,"E0"),sQuery(id+"F0.wireOp",EDGE,"E10.1.6"),sQuery(id+"F0.wireOp",EDGE,"E11"),sQuery(id+"F0.wireOp",EDGE,"E12"),sQuery(id+"F0.wireOp",EDGE,"E13.1.0"),sQuery(id+"F0.wireOp",EDGE,"E13.1.1"),sQuery(id+"F0.wireOp",EDGE,"E13.2.0"),sQuery(id+"F0.wireOp",EDGE,"E13.2.1")])]}),"instanceName":"1"}),"instanceName":"1"});
            transform(context, id + "F19", {"entities" : qUnion([Q0]), "transformType" : TransformType.TRANSLATION_3D, "dx" : 69.1 * mm, "dy" : 0 * mm, "dz" : 0 * mm, "makeCopy" : true});
        }
        {
            var Q0;
            Q0=makeQuery(id+"F19.opPattern","COPY",BODY,{"derivedFrom":makeQuery(id+"F18.opPattern","COPY",BODY,{"derivedFrom":makeQuery(id+"F13.opPattern","COPY",BODY,{"derivedFrom":makeQuery(id+"F1.opExtrude","SWEPT_BODY",BODY,{"disambiguationData":[OSD([sQuery(id+"F0.wireOp",EDGE,"E2.0"),sQuery(id+"F0.wireOp",EDGE,"E2.1"),sQuery(id+"F0.wireOp",EDGE,"E2.2"),sQuery(id+"F0.wireOp",EDGE,"E2.3"),sQuery(id+"F0.wireOp",EDGE,"E2.4"),sQuery(id+"F0.wireOp",EDGE,"E2.5"),sQuery(id+"F0.wireOp",EDGE,"E3"),sQuery(id+"F0.wireOp",EDGE,"E4"),sQuery(id+"F0.wireOp",EDGE,"E5.0"),sQuery(id+"F0.wireOp",EDGE,"E5.1"),sQuery(id+"F0.wireOp",EDGE,"E5.3"),sQuery(id+"F0.wireOp",EDGE,"E5.4"),sQuery(id+"F0.wireOp",EDGE,"E5.5"),sQuery(id+"F0.wireOp",EDGE,"E6.trimOffspring"),sQuery(id+"F0.wireOp",EDGE,"E7.trimOffspring"),sQuery(id+"F0.wireOp",EDGE,"E9.trimOffspring"),sQuery(id+"F0.wireOp",EDGE,"E10.1.0"),sQuery(id+"F0.wireOp",EDGE,"E10.1.1"),sQuery(id+"F0.wireOp",EDGE,"E10.1.2"),sQuery(id+"F0.wireOp",EDGE,"E10.1.3"),sQuery(id+"F0.wireOp",EDGE,"E10.1.5"),sQuery(id+"F0.wireOp",EDGE,"E10.1.7"),sQuery(id+"F0.wireOp",EDGE,"E10.1.8"),sQuery(id+"F0.wireOp",EDGE,"E10.1.9"),sQuery(id+"F0.wireOp",EDGE,"E10.1.10"),sQuery(id+"F0.wireOp",EDGE,"E10.1.11"),sQuery(id+"F0.wireOp",EDGE,"E10.1.12"),sQuery(id+"F0.wireOp",EDGE,"E10.1.14"),sQuery(id+"F0.wireOp",EDGE,"E10.1.15"),sQuery(id+"F0.wireOp",EDGE,"E10.1.16"),sQuery(id+"F0.wireOp",EDGE,"E10.1.18"),sQuery(id+"F0.wireOp",EDGE,"E10.1.20"),sQuery(id+"F0.wireOp",EDGE,"E10.2.0"),sQuery(id+"F0.wireOp",EDGE,"E10.2.1"),sQuery(id+"F0.wireOp",EDGE,"E10.2.2"),sQuery(id+"F0.wireOp",EDGE,"E10.2.3"),sQuery(id+"F0.wireOp",EDGE,"E10.2.5"),sQuery(id+"F0.wireOp",EDGE,"E10.2.7"),sQuery(id+"F0.wireOp",EDGE,"E10.2.8"),sQuery(id+"F0.wireOp",EDGE,"E10.2.9"),sQuery(id+"F0.wireOp",EDGE,"E10.2.10"),sQuery(id+"F0.wireOp",EDGE,"E10.2.11"),sQuery(id+"F0.wireOp",EDGE,"E10.2.12"),sQuery(id+"F0.wireOp",EDGE,"E1"),sQuery(id+"F0.wireOp",EDGE,"E10.2.14"),sQuery(id+"F0.wireOp",EDGE,"E10.2.15"),sQuery(id+"F0.wireOp",EDGE,"E10.2.16"),sQuery(id+"F0.wireOp",EDGE,"E10.2.18"),sQuery(id+"F0.wireOp",EDGE,"E10.2.20"),sQuery(id+"F0.wireOp",EDGE,"E8.trimOffspring"),sQuery(id+"F0.wireOp",EDGE,"E0"),sQuery(id+"F0.wireOp",EDGE,"E10.1.6"),sQuery(id+"F0.wireOp",EDGE,"E11"),sQuery(id+"F0.wireOp",EDGE,"E12"),sQuery(id+"F0.wireOp",EDGE,"E13.1.0"),sQuery(id+"F0.wireOp",EDGE,"E13.1.1"),sQuery(id+"F0.wireOp",EDGE,"E13.2.0"),sQuery(id+"F0.wireOp",EDGE,"E13.2.1")])]}),"instanceName":"1"}),"instanceName":"1"}),"instanceName":"1"});
            transform(context, id + "F20", {"entities" : qUnion([Q0]), "transformType" : TransformType.TRANSLATION_3D, "dx" : 69.1 * mm, "dy" : 0 * mm, "dz" : 0 * mm, "makeCopy" : true});
        }
        {
            var Q0;
            Q0=makeQuery(id+"F20.opPattern","COPY",BODY,{"derivedFrom":makeQuery(id+"F19.opPattern","COPY",BODY,{"derivedFrom":makeQuery(id+"F18.opPattern","COPY",BODY,{"derivedFrom":makeQuery(id+"F13.opPattern","COPY",BODY,{"derivedFrom":makeQuery(id+"F1.opExtrude","SWEPT_BODY",BODY,{"disambiguationData":[OSD([sQuery(id+"F0.wireOp",EDGE,"E2.0"),sQuery(id+"F0.wireOp",EDGE,"E2.1"),sQuery(id+"F0.wireOp",EDGE,"E2.2"),sQuery(id+"F0.wireOp",EDGE,"E2.3"),sQuery(id+"F0.wireOp",EDGE,"E2.4"),sQuery(id+"F0.wireOp",EDGE,"E2.5"),sQuery(id+"F0.wireOp",EDGE,"E3"),sQuery(id+"F0.wireOp",EDGE,"E4"),sQuery(id+"F0.wireOp",EDGE,"E5.0"),sQuery(id+"F0.wireOp",EDGE,"E5.1"),sQuery(id+"F0.wireOp",EDGE,"E5.3"),sQuery(id+"F0.wireOp",EDGE,"E5.4"),sQuery(id+"F0.wireOp",EDGE,"E5.5"),sQuery(id+"F0.wireOp",EDGE,"E6.trimOffspring"),sQuery(id+"F0.wireOp",EDGE,"E7.trimOffspring"),sQuery(id+"F0.wireOp",EDGE,"E9.trimOffspring"),sQuery(id+"F0.wireOp",EDGE,"E10.1.0"),sQuery(id+"F0.wireOp",EDGE,"E10.1.1"),sQuery(id+"F0.wireOp",EDGE,"E10.1.2"),sQuery(id+"F0.wireOp",EDGE,"E10.1.3"),sQuery(id+"F0.wireOp",EDGE,"E10.1.5"),sQuery(id+"F0.wireOp",EDGE,"E10.1.7"),sQuery(id+"F0.wireOp",EDGE,"E10.1.8"),sQuery(id+"F0.wireOp",EDGE,"E10.1.9"),sQuery(id+"F0.wireOp",EDGE,"E10.1.10"),sQuery(id+"F0.wireOp",EDGE,"E10.1.11"),sQuery(id+"F0.wireOp",EDGE,"E10.1.12"),sQuery(id+"F0.wireOp",EDGE,"E10.1.14"),sQuery(id+"F0.wireOp",EDGE,"E10.1.15"),sQuery(id+"F0.wireOp",EDGE,"E10.1.16"),sQuery(id+"F0.wireOp",EDGE,"E10.1.18"),sQuery(id+"F0.wireOp",EDGE,"E10.1.20"),sQuery(id+"F0.wireOp",EDGE,"E10.2.0"),sQuery(id+"F0.wireOp",EDGE,"E10.2.1"),sQuery(id+"F0.wireOp",EDGE,"E10.2.2"),sQuery(id+"F0.wireOp",EDGE,"E10.2.3"),sQuery(id+"F0.wireOp",EDGE,"E10.2.5"),sQuery(id+"F0.wireOp",EDGE,"E10.2.7"),sQuery(id+"F0.wireOp",EDGE,"E10.2.8"),sQuery(id+"F0.wireOp",EDGE,"E10.2.9"),sQuery(id+"F0.wireOp",EDGE,"E10.2.10"),sQuery(id+"F0.wireOp",EDGE,"E10.2.11"),sQuery(id+"F0.wireOp",EDGE,"E10.2.12"),sQuery(id+"F0.wireOp",EDGE,"E1"),sQuery(id+"F0.wireOp",EDGE,"E10.2.14"),sQuery(id+"F0.wireOp",EDGE,"E10.2.15"),sQuery(id+"F0.wireOp",EDGE,"E10.2.16"),sQuery(id+"F0.wireOp",EDGE,"E10.2.18"),sQuery(id+"F0.wireOp",EDGE,"E10.2.20"),sQuery(id+"F0.wireOp",EDGE,"E8.trimOffspring"),sQuery(id+"F0.wireOp",EDGE,"E0"),sQuery(id+"F0.wireOp",EDGE,"E10.1.6"),sQuery(id+"F0.wireOp",EDGE,"E11"),sQuery(id+"F0.wireOp",EDGE,"E12"),sQuery(id+"F0.wireOp",EDGE,"E13.1.0"),sQuery(id+"F0.wireOp",EDGE,"E13.1.1"),sQuery(id+"F0.wireOp",EDGE,"E13.2.0"),sQuery(id+"F0.wireOp",EDGE,"E13.2.1")])]}),"instanceName":"1"}),"instanceName":"1"}),"instanceName":"1"}),"instanceName":"1"});
            var Q1;
            Q1=makeQuery(id+"F20.opPattern","COPY",EDGE,{"derivedFrom":makeQuery(id+"F19.opPattern","COPY",EDGE,{"derivedFrom":makeQuery(id+"F18.opPattern","COPY",EDGE,{"derivedFrom":makeQuery(id+"F13.opPattern","COPY",EDGE,{"derivedFrom":makeQuery(id+"F1.opExtrude","CAP_EDGE",EDGE,{"disambiguationData":[OSD([sQuery(id+"F0.wireOp",EDGE,"E1")])],"isStart":false}),"instanceName":"1"}),"instanceName":"1"}),"instanceName":"1"}),"instanceName":"1"});
            transform(context, id + "F21", {"entities" : qUnion([Q0]), "transformType" : TransformType.ROTATION, "transformAxis" : qUnion([Q1]), "angle" : 38 * degree, "makeCopy" : true});
        }
        {
            var Q0;
            Q0=makeQuery(id+"F21.opPattern","COPY",BODY,{"derivedFrom":makeQuery(id+"F20.opPattern","COPY",BODY,{"derivedFrom":makeQuery(id+"F19.opPattern","COPY",BODY,{"derivedFrom":makeQuery(id+"F18.opPattern","COPY",BODY,{"derivedFrom":makeQuery(id+"F13.opPattern","COPY",BODY,{"derivedFrom":makeQuery(id+"F1.opExtrude","SWEPT_BODY",BODY,{"disambiguationData":[OSD([sQuery(id+"F0.wireOp",EDGE,"E2.0"),sQuery(id+"F0.wireOp",EDGE,"E2.1"),sQuery(id+"F0.wireOp",EDGE,"E2.2"),sQuery(id+"F0.wireOp",EDGE,"E2.3"),sQuery(id+"F0.wireOp",EDGE,"E2.4"),sQuery(id+"F0.wireOp",EDGE,"E2.5"),sQuery(id+"F0.wireOp",EDGE,"E3"),sQuery(id+"F0.wireOp",EDGE,"E4"),sQuery(id+"F0.wireOp",EDGE,"E5.0"),sQuery(id+"F0.wireOp",EDGE,"E5.1"),sQuery(id+"F0.wireOp",EDGE,"E5.3"),sQuery(id+"F0.wireOp",EDGE,"E5.4"),sQuery(id+"F0.wireOp",EDGE,"E5.5"),sQuery(id+"F0.wireOp",EDGE,"E6.trimOffspring"),sQuery(id+"F0.wireOp",EDGE,"E7.trimOffspring"),sQuery(id+"F0.wireOp",EDGE,"E9.trimOffspring"),sQuery(id+"F0.wireOp",EDGE,"E10.1.0"),sQuery(id+"F0.wireOp",EDGE,"E10.1.1"),sQuery(id+"F0.wireOp",EDGE,"E10.1.2"),sQuery(id+"F0.wireOp",EDGE,"E10.1.3"),sQuery(id+"F0.wireOp",EDGE,"E10.1.5"),sQuery(id+"F0.wireOp",EDGE,"E10.1.7"),sQuery(id+"F0.wireOp",EDGE,"E10.1.8"),sQuery(id+"F0.wireOp",EDGE,"E10.1.9"),sQuery(id+"F0.wireOp",EDGE,"E10.1.10"),sQuery(id+"F0.wireOp",EDGE,"E10.1.11"),sQuery(id+"F0.wireOp",EDGE,"E10.1.12"),sQuery(id+"F0.wireOp",EDGE,"E10.1.14"),sQuery(id+"F0.wireOp",EDGE,"E10.1.15"),sQuery(id+"F0.wireOp",EDGE,"E10.1.16"),sQuery(id+"F0.wireOp",EDGE,"E10.1.18"),sQuery(id+"F0.wireOp",EDGE,"E10.1.20"),sQuery(id+"F0.wireOp",EDGE,"E10.2.0"),sQuery(id+"F0.wireOp",EDGE,"E10.2.1"),sQuery(id+"F0.wireOp",EDGE,"E10.2.2"),sQuery(id+"F0.wireOp",EDGE,"E10.2.3"),sQuery(id+"F0.wireOp",EDGE,"E10.2.5"),sQuery(id+"F0.wireOp",EDGE,"E10.2.7"),sQuery(id+"F0.wireOp",EDGE,"E10.2.8"),sQuery(id+"F0.wireOp",EDGE,"E10.2.9"),sQuery(id+"F0.wireOp",EDGE,"E10.2.10"),sQuery(id+"F0.wireOp",EDGE,"E10.2.11"),sQuery(id+"F0.wireOp",EDGE,"E10.2.12"),sQuery(id+"F0.wireOp",EDGE,"E1"),sQuery(id+"F0.wireOp",EDGE,"E10.2.14"),sQuery(id+"F0.wireOp",EDGE,"E10.2.15"),sQuery(id+"F0.wireOp",EDGE,"E10.2.16"),sQuery(id+"F0.wireOp",EDGE,"E10.2.18"),sQuery(id+"F0.wireOp",EDGE,"E10.2.20"),sQuery(id+"F0.wireOp",EDGE,"E8.trimOffspring"),sQuery(id+"F0.wireOp",EDGE,"E0"),sQuery(id+"F0.wireOp",EDGE,"E10.1.6"),sQuery(id+"F0.wireOp",EDGE,"E11"),sQuery(id+"F0.wireOp",EDGE,"E12"),sQuery(id+"F0.wireOp",EDGE,"E13.1.0"),sQuery(id+"F0.wireOp",EDGE,"E13.1.1"),sQuery(id+"F0.wireOp",EDGE,"E13.2.0"),sQuery(id+"F0.wireOp",EDGE,"E13.2.1")])]}),"instanceName":"1"}),"instanceName":"1"}),"instanceName":"1"}),"instanceName":"1"}),"instanceName":"1"});
            transform(context, id + "F22", {"entities" : qUnion([Q0]), "transformType" : TransformType.TRANSLATION_3D, "dx" : 61.5 * mm, "dy" : -15.8 * mm, "dz" : 0 * mm, "makeCopy" : false});
        }
        {
            var Q0;
            Q0=makeQuery(id+"F5.opPattern","COPY",BODY,{"derivedFrom":makeQuery(id+"F1.opExtrude","SWEPT_BODY",BODY,{"disambiguationData":[OSD([sQuery(id+"F0.wireOp",EDGE,"E2.0"),sQuery(id+"F0.wireOp",EDGE,"E2.1"),sQuery(id+"F0.wireOp",EDGE,"E2.2"),sQuery(id+"F0.wireOp",EDGE,"E2.3"),sQuery(id+"F0.wireOp",EDGE,"E2.4"),sQuery(id+"F0.wireOp",EDGE,"E2.5"),sQuery(id+"F0.wireOp",EDGE,"E3"),sQuery(id+"F0.wireOp",EDGE,"E4"),sQuery(id+"F0.wireOp",EDGE,"E5.0"),sQuery(id+"F0.wireOp",EDGE,"E5.1"),sQuery(id+"F0.wireOp",EDGE,"E5.3"),sQuery(id+"F0.wireOp",EDGE,"E5.4"),sQuery(id+"F0.wireOp",EDGE,"E5.5"),sQuery(id+"F0.wireOp",EDGE,"E6.trimOffspring"),sQuery(id+"F0.wireOp",EDGE,"E7.trimOffspring"),sQuery(id+"F0.wireOp",EDGE,"E9.trimOffspring"),sQuery(id+"F0.wireOp",EDGE,"E10.1.0"),sQuery(id+"F0.wireOp",EDGE,"E10.1.1"),sQuery(id+"F0.wireOp",EDGE,"E10.1.2"),sQuery(id+"F0.wireOp",EDGE,"E10.1.3"),sQuery(id+"F0.wireOp",EDGE,"E10.1.5"),sQuery(id+"F0.wireOp",EDGE,"E10.1.7"),sQuery(id+"F0.wireOp",EDGE,"E10.1.8"),sQuery(id+"F0.wireOp",EDGE,"E10.1.9"),sQuery(id+"F0.wireOp",EDGE,"E10.1.10"),sQuery(id+"F0.wireOp",EDGE,"E10.1.11"),sQuery(id+"F0.wireOp",EDGE,"E10.1.12"),sQuery(id+"F0.wireOp",EDGE,"E10.1.14"),sQuery(id+"F0.wireOp",EDGE,"E10.1.15"),sQuery(id+"F0.wireOp",EDGE,"E10.1.16"),sQuery(id+"F0.wireOp",EDGE,"E10.1.18"),sQuery(id+"F0.wireOp",EDGE,"E10.1.20"),sQuery(id+"F0.wireOp",EDGE,"E10.2.0"),sQuery(id+"F0.wireOp",EDGE,"E10.2.1"),sQuery(id+"F0.wireOp",EDGE,"E10.2.2"),sQuery(id+"F0.wireOp",EDGE,"E10.2.3"),sQuery(id+"F0.wireOp",EDGE,"E10.2.5"),sQuery(id+"F0.wireOp",EDGE,"E10.2.7"),sQuery(id+"F0.wireOp",EDGE,"E10.2.8"),sQuery(id+"F0.wireOp",EDGE,"E10.2.9"),sQuery(id+"F0.wireOp",EDGE,"E10.2.10"),sQuery(id+"F0.wireOp",EDGE,"E10.2.11"),sQuery(id+"F0.wireOp",EDGE,"E10.2.12"),sQuery(id+"F0.wireOp",EDGE,"E1"),sQuery(id+"F0.wireOp",EDGE,"E10.2.14"),sQuery(id+"F0.wireOp",EDGE,"E10.2.15"),sQuery(id+"F0.wireOp",EDGE,"E10.2.16"),sQuery(id+"F0.wireOp",EDGE,"E10.2.18"),sQuery(id+"F0.wireOp",EDGE,"E10.2.20"),sQuery(id+"F0.wireOp",EDGE,"E8.trimOffspring"),sQuery(id+"F0.wireOp",EDGE,"E0"),sQuery(id+"F0.wireOp",EDGE,"E10.1.6"),sQuery(id+"F0.wireOp",EDGE,"E11"),sQuery(id+"F0.wireOp",EDGE,"E12"),sQuery(id+"F0.wireOp",EDGE,"E13.1.0"),sQuery(id+"F0.wireOp",EDGE,"E13.1.1"),sQuery(id+"F0.wireOp",EDGE,"E13.2.0"),sQuery(id+"F0.wireOp",EDGE,"E13.2.1")])]}),"instanceName":"1"});
            var Q1;
            Q1=makeQuery(id+"F1.opExtrude","SWEPT_BODY",BODY,{"disambiguationData":[OSD([sQuery(id+"F0.wireOp",EDGE,"E2.0"),sQuery(id+"F0.wireOp",EDGE,"E2.1"),sQuery(id+"F0.wireOp",EDGE,"E2.2"),sQuery(id+"F0.wireOp",EDGE,"E2.3"),sQuery(id+"F0.wireOp",EDGE,"E2.4"),sQuery(id+"F0.wireOp",EDGE,"E2.5"),sQuery(id+"F0.wireOp",EDGE,"E3"),sQuery(id+"F0.wireOp",EDGE,"E4"),sQuery(id+"F0.wireOp",EDGE,"E5.0"),sQuery(id+"F0.wireOp",EDGE,"E5.1"),sQuery(id+"F0.wireOp",EDGE,"E5.3"),sQuery(id+"F0.wireOp",EDGE,"E5.4"),sQuery(id+"F0.wireOp",EDGE,"E5.5"),sQuery(id+"F0.wireOp",EDGE,"E6.trimOffspring"),sQuery(id+"F0.wireOp",EDGE,"E7.trimOffspring"),sQuery(id+"F0.wireOp",EDGE,"E9.trimOffspring"),sQuery(id+"F0.wireOp",EDGE,"E10.1.0"),sQuery(id+"F0.wireOp",EDGE,"E10.1.1"),sQuery(id+"F0.wireOp",EDGE,"E10.1.2"),sQuery(id+"F0.wireOp",EDGE,"E10.1.3"),sQuery(id+"F0.wireOp",EDGE,"E10.1.5"),sQuery(id+"F0.wireOp",EDGE,"E10.1.7"),sQuery(id+"F0.wireOp",EDGE,"E10.1.8"),sQuery(id+"F0.wireOp",EDGE,"E10.1.9"),sQuery(id+"F0.wireOp",EDGE,"E10.1.10"),sQuery(id+"F0.wireOp",EDGE,"E10.1.11"),sQuery(id+"F0.wireOp",EDGE,"E10.1.12"),sQuery(id+"F0.wireOp",EDGE,"E10.1.14"),sQuery(id+"F0.wireOp",EDGE,"E10.1.15"),sQuery(id+"F0.wireOp",EDGE,"E10.1.16"),sQuery(id+"F0.wireOp",EDGE,"E10.1.18"),sQuery(id+"F0.wireOp",EDGE,"E10.1.20"),sQuery(id+"F0.wireOp",EDGE,"E10.2.0"),sQuery(id+"F0.wireOp",EDGE,"E10.2.1"),sQuery(id+"F0.wireOp",EDGE,"E10.2.2"),sQuery(id+"F0.wireOp",EDGE,"E10.2.3"),sQuery(id+"F0.wireOp",EDGE,"E10.2.5"),sQuery(id+"F0.wireOp",EDGE,"E10.2.7"),sQuery(id+"F0.wireOp",EDGE,"E10.2.8"),sQuery(id+"F0.wireOp",EDGE,"E10.2.9"),sQuery(id+"F0.wireOp",EDGE,"E10.2.10"),sQuery(id+"F0.wireOp",EDGE,"E10.2.11"),sQuery(id+"F0.wireOp",EDGE,"E10.2.12"),sQuery(id+"F0.wireOp",EDGE,"E1"),sQuery(id+"F0.wireOp",EDGE,"E10.2.14"),sQuery(id+"F0.wireOp",EDGE,"E10.2.15"),sQuery(id+"F0.wireOp",EDGE,"E10.2.16"),sQuery(id+"F0.wireOp",EDGE,"E10.2.18"),sQuery(id+"F0.wireOp",EDGE,"E10.2.20"),sQuery(id+"F0.wireOp",EDGE,"E8.trimOffspring"),sQuery(id+"F0.wireOp",EDGE,"E0"),sQuery(id+"F0.wireOp",EDGE,"E10.1.6"),sQuery(id+"F0.wireOp",EDGE,"E11"),sQuery(id+"F0.wireOp",EDGE,"E12"),sQuery(id+"F0.wireOp",EDGE,"E13.1.0"),sQuery(id+"F0.wireOp",EDGE,"E13.1.1"),sQuery(id+"F0.wireOp",EDGE,"E13.2.0"),sQuery(id+"F0.wireOp",EDGE,"E13.2.1")])]});
            var Q2;
            Q2=makeQuery(id+"F7.opPattern","COPY",BODY,{"derivedFrom":makeQuery(id+"F1.opExtrude","SWEPT_BODY",BODY,{"disambiguationData":[OSD([sQuery(id+"F0.wireOp",EDGE,"E2.0"),sQuery(id+"F0.wireOp",EDGE,"E2.1"),sQuery(id+"F0.wireOp",EDGE,"E2.2"),sQuery(id+"F0.wireOp",EDGE,"E2.3"),sQuery(id+"F0.wireOp",EDGE,"E2.4"),sQuery(id+"F0.wireOp",EDGE,"E2.5"),sQuery(id+"F0.wireOp",EDGE,"E3"),sQuery(id+"F0.wireOp",EDGE,"E4"),sQuery(id+"F0.wireOp",EDGE,"E5.0"),sQuery(id+"F0.wireOp",EDGE,"E5.1"),sQuery(id+"F0.wireOp",EDGE,"E5.3"),sQuery(id+"F0.wireOp",EDGE,"E5.4"),sQuery(id+"F0.wireOp",EDGE,"E5.5"),sQuery(id+"F0.wireOp",EDGE,"E6.trimOffspring"),sQuery(id+"F0.wireOp",EDGE,"E7.trimOffspring"),sQuery(id+"F0.wireOp",EDGE,"E9.trimOffspring"),sQuery(id+"F0.wireOp",EDGE,"E10.1.0"),sQuery(id+"F0.wireOp",EDGE,"E10.1.1"),sQuery(id+"F0.wireOp",EDGE,"E10.1.2"),sQuery(id+"F0.wireOp",EDGE,"E10.1.3"),sQuery(id+"F0.wireOp",EDGE,"E10.1.5"),sQuery(id+"F0.wireOp",EDGE,"E10.1.7"),sQuery(id+"F0.wireOp",EDGE,"E10.1.8"),sQuery(id+"F0.wireOp",EDGE,"E10.1.9"),sQuery(id+"F0.wireOp",EDGE,"E10.1.10"),sQuery(id+"F0.wireOp",EDGE,"E10.1.11"),sQuery(id+"F0.wireOp",EDGE,"E10.1.12"),sQuery(id+"F0.wireOp",EDGE,"E10.1.14"),sQuery(id+"F0.wireOp",EDGE,"E10.1.15"),sQuery(id+"F0.wireOp",EDGE,"E10.1.16"),sQuery(id+"F0.wireOp",EDGE,"E10.1.18"),sQuery(id+"F0.wireOp",EDGE,"E10.1.20"),sQuery(id+"F0.wireOp",EDGE,"E10.2.0"),sQuery(id+"F0.wireOp",EDGE,"E10.2.1"),sQuery(id+"F0.wireOp",EDGE,"E10.2.2"),sQuery(id+"F0.wireOp",EDGE,"E10.2.3"),sQuery(id+"F0.wireOp",EDGE,"E10.2.5"),sQuery(id+"F0.wireOp",EDGE,"E10.2.7"),sQuery(id+"F0.wireOp",EDGE,"E10.2.8"),sQuery(id+"F0.wireOp",EDGE,"E10.2.9"),sQuery(id+"F0.wireOp",EDGE,"E10.2.10"),sQuery(id+"F0.wireOp",EDGE,"E10.2.11"),sQuery(id+"F0.wireOp",EDGE,"E10.2.12"),sQuery(id+"F0.wireOp",EDGE,"E1"),sQuery(id+"F0.wireOp",EDGE,"E10.2.14"),sQuery(id+"F0.wireOp",EDGE,"E10.2.15"),sQuery(id+"F0.wireOp",EDGE,"E10.2.16"),sQuery(id+"F0.wireOp",EDGE,"E10.2.18"),sQuery(id+"F0.wireOp",EDGE,"E10.2.20"),sQuery(id+"F0.wireOp",EDGE,"E8.trimOffspring"),sQuery(id+"F0.wireOp",EDGE,"E0"),sQuery(id+"F0.wireOp",EDGE,"E10.1.6"),sQuery(id+"F0.wireOp",EDGE,"E11"),sQuery(id+"F0.wireOp",EDGE,"E12"),sQuery(id+"F0.wireOp",EDGE,"E13.1.0"),sQuery(id+"F0.wireOp",EDGE,"E13.1.1"),sQuery(id+"F0.wireOp",EDGE,"E13.2.0"),sQuery(id+"F0.wireOp",EDGE,"E13.2.1")])]}),"instanceName":"1"});
            var Q3;
            Q3=makeQuery(id+"F8.opPattern","COPY",BODY,{"derivedFrom":makeQuery(id+"F7.opPattern","COPY",BODY,{"derivedFrom":makeQuery(id+"F1.opExtrude","SWEPT_BODY",BODY,{"disambiguationData":[OSD([sQuery(id+"F0.wireOp",EDGE,"E2.0"),sQuery(id+"F0.wireOp",EDGE,"E2.1"),sQuery(id+"F0.wireOp",EDGE,"E2.2"),sQuery(id+"F0.wireOp",EDGE,"E2.3"),sQuery(id+"F0.wireOp",EDGE,"E2.4"),sQuery(id+"F0.wireOp",EDGE,"E2.5"),sQuery(id+"F0.wireOp",EDGE,"E3"),sQuery(id+"F0.wireOp",EDGE,"E4"),sQuery(id+"F0.wireOp",EDGE,"E5.0"),sQuery(id+"F0.wireOp",EDGE,"E5.1"),sQuery(id+"F0.wireOp",EDGE,"E5.3"),sQuery(id+"F0.wireOp",EDGE,"E5.4"),sQuery(id+"F0.wireOp",EDGE,"E5.5"),sQuery(id+"F0.wireOp",EDGE,"E6.trimOffspring"),sQuery(id+"F0.wireOp",EDGE,"E7.trimOffspring"),sQuery(id+"F0.wireOp",EDGE,"E9.trimOffspring"),sQuery(id+"F0.wireOp",EDGE,"E10.1.0"),sQuery(id+"F0.wireOp",EDGE,"E10.1.1"),sQuery(id+"F0.wireOp",EDGE,"E10.1.2"),sQuery(id+"F0.wireOp",EDGE,"E10.1.3"),sQuery(id+"F0.wireOp",EDGE,"E10.1.5"),sQuery(id+"F0.wireOp",EDGE,"E10.1.7"),sQuery(id+"F0.wireOp",EDGE,"E10.1.8"),sQuery(id+"F0.wireOp",EDGE,"E10.1.9"),sQuery(id+"F0.wireOp",EDGE,"E10.1.10"),sQuery(id+"F0.wireOp",EDGE,"E10.1.11"),sQuery(id+"F0.wireOp",EDGE,"E10.1.12"),sQuery(id+"F0.wireOp",EDGE,"E10.1.14"),sQuery(id+"F0.wireOp",EDGE,"E10.1.15"),sQuery(id+"F0.wireOp",EDGE,"E10.1.16"),sQuery(id+"F0.wireOp",EDGE,"E10.1.18"),sQuery(id+"F0.wireOp",EDGE,"E10.1.20"),sQuery(id+"F0.wireOp",EDGE,"E10.2.0"),sQuery(id+"F0.wireOp",EDGE,"E10.2.1"),sQuery(id+"F0.wireOp",EDGE,"E10.2.2"),sQuery(id+"F0.wireOp",EDGE,"E10.2.3"),sQuery(id+"F0.wireOp",EDGE,"E10.2.5"),sQuery(id+"F0.wireOp",EDGE,"E10.2.7"),sQuery(id+"F0.wireOp",EDGE,"E10.2.8"),sQuery(id+"F0.wireOp",EDGE,"E10.2.9"),sQuery(id+"F0.wireOp",EDGE,"E10.2.10"),sQuery(id+"F0.wireOp",EDGE,"E10.2.11"),sQuery(id+"F0.wireOp",EDGE,"E10.2.12"),sQuery(id+"F0.wireOp",EDGE,"E1"),sQuery(id+"F0.wireOp",EDGE,"E10.2.14"),sQuery(id+"F0.wireOp",EDGE,"E10.2.15"),sQuery(id+"F0.wireOp",EDGE,"E10.2.16"),sQuery(id+"F0.wireOp",EDGE,"E10.2.18"),sQuery(id+"F0.wireOp",EDGE,"E10.2.20"),sQuery(id+"F0.wireOp",EDGE,"E8.trimOffspring"),sQuery(id+"F0.wireOp",EDGE,"E0"),sQuery(id+"F0.wireOp",EDGE,"E10.1.6"),sQuery(id+"F0.wireOp",EDGE,"E11"),sQuery(id+"F0.wireOp",EDGE,"E12"),sQuery(id+"F0.wireOp",EDGE,"E13.1.0"),sQuery(id+"F0.wireOp",EDGE,"E13.1.1"),sQuery(id+"F0.wireOp",EDGE,"E13.2.0"),sQuery(id+"F0.wireOp",EDGE,"E13.2.1")])]}),"instanceName":"1"}),"instanceName":"1"});
            transform(context, id + "F23", {"entities" : qUnion([Q0, Q1, Q2, Q3]), "transformType" : TransformType.TRANSLATION_3D, "dx" : 0 * mm, "dy" : -108 * mm, "dz" : 0 * mm, "makeCopy" : true});
        }
        {
            var Q0;
            Q0=makeQuery(id+"F23.opPattern","COPY",BODY,{"derivedFrom":makeQuery(id+"F5.opPattern","COPY",BODY,{"derivedFrom":makeQuery(id+"F1.opExtrude","SWEPT_BODY",BODY,{"disambiguationData":[OSD([sQuery(id+"F0.wireOp",EDGE,"E2.0"),sQuery(id+"F0.wireOp",EDGE,"E2.1"),sQuery(id+"F0.wireOp",EDGE,"E2.2"),sQuery(id+"F0.wireOp",EDGE,"E2.3"),sQuery(id+"F0.wireOp",EDGE,"E2.4"),sQuery(id+"F0.wireOp",EDGE,"E2.5"),sQuery(id+"F0.wireOp",EDGE,"E3"),sQuery(id+"F0.wireOp",EDGE,"E4"),sQuery(id+"F0.wireOp",EDGE,"E5.0"),sQuery(id+"F0.wireOp",EDGE,"E5.1"),sQuery(id+"F0.wireOp",EDGE,"E5.3"),sQuery(id+"F0.wireOp",EDGE,"E5.4"),sQuery(id+"F0.wireOp",EDGE,"E5.5"),sQuery(id+"F0.wireOp",EDGE,"E6.trimOffspring"),sQuery(id+"F0.wireOp",EDGE,"E7.trimOffspring"),sQuery(id+"F0.wireOp",EDGE,"E9.trimOffspring"),sQuery(id+"F0.wireOp",EDGE,"E10.1.0"),sQuery(id+"F0.wireOp",EDGE,"E10.1.1"),sQuery(id+"F0.wireOp",EDGE,"E10.1.2"),sQuery(id+"F0.wireOp",EDGE,"E10.1.3"),sQuery(id+"F0.wireOp",EDGE,"E10.1.5"),sQuery(id+"F0.wireOp",EDGE,"E10.1.7"),sQuery(id+"F0.wireOp",EDGE,"E10.1.8"),sQuery(id+"F0.wireOp",EDGE,"E10.1.9"),sQuery(id+"F0.wireOp",EDGE,"E10.1.10"),sQuery(id+"F0.wireOp",EDGE,"E10.1.11"),sQuery(id+"F0.wireOp",EDGE,"E10.1.12"),sQuery(id+"F0.wireOp",EDGE,"E10.1.14"),sQuery(id+"F0.wireOp",EDGE,"E10.1.15"),sQuery(id+"F0.wireOp",EDGE,"E10.1.16"),sQuery(id+"F0.wireOp",EDGE,"E10.1.18"),sQuery(id+"F0.wireOp",EDGE,"E10.1.20"),sQuery(id+"F0.wireOp",EDGE,"E10.2.0"),sQuery(id+"F0.wireOp",EDGE,"E10.2.1"),sQuery(id+"F0.wireOp",EDGE,"E10.2.2"),sQuery(id+"F0.wireOp",EDGE,"E10.2.3"),sQuery(id+"F0.wireOp",EDGE,"E10.2.5"),sQuery(id+"F0.wireOp",EDGE,"E10.2.7"),sQuery(id+"F0.wireOp",EDGE,"E10.2.8"),sQuery(id+"F0.wireOp",EDGE,"E10.2.9"),sQuery(id+"F0.wireOp",EDGE,"E10.2.10"),sQuery(id+"F0.wireOp",EDGE,"E10.2.11"),sQuery(id+"F0.wireOp",EDGE,"E10.2.12"),sQuery(id+"F0.wireOp",EDGE,"E1"),sQuery(id+"F0.wireOp",EDGE,"E10.2.14"),sQuery(id+"F0.wireOp",EDGE,"E10.2.15"),sQuery(id+"F0.wireOp",EDGE,"E10.2.16"),sQuery(id+"F0.wireOp",EDGE,"E10.2.18"),sQuery(id+"F0.wireOp",EDGE,"E10.2.20"),sQuery(id+"F0.wireOp",EDGE,"E8.trimOffspring"),sQuery(id+"F0.wireOp",EDGE,"E0"),sQuery(id+"F0.wireOp",EDGE,"E10.1.6"),sQuery(id+"F0.wireOp",EDGE,"E11"),sQuery(id+"F0.wireOp",EDGE,"E12"),sQuery(id+"F0.wireOp",EDGE,"E13.1.0"),sQuery(id+"F0.wireOp",EDGE,"E13.1.1"),sQuery(id+"F0.wireOp",EDGE,"E13.2.0"),sQuery(id+"F0.wireOp",EDGE,"E13.2.1")])]}),"instanceName":"1"}),"instanceName":"1"});
            var Q1;
            Q1=makeQuery(id+"F23.opPattern","COPY",EDGE,{"derivedFrom":makeQuery(id+"F5.opPattern","COPY",EDGE,{"derivedFrom":makeQuery(id+"F1.opExtrude","CAP_EDGE",EDGE,{"disambiguationData":[OSD([sQuery(id+"F0.wireOp",EDGE,"E1")])],"isStart":false}),"instanceName":"1"}),"instanceName":"1"});
            transform(context, id + "F24", {"entities" : qUnion([Q0]), "transformType" : TransformType.ROTATION, "transformAxis" : qUnion([Q1]), "angle" : 42 * degree, "oppositeDirection" : true, "makeCopy" : false});
        }
        {
            var Q0;
            Q0=makeQuery(id+"F23.opPattern","COPY",BODY,{"derivedFrom":makeQuery(id+"F1.opExtrude","SWEPT_BODY",BODY,{"disambiguationData":[OSD([sQuery(id+"F0.wireOp",EDGE,"E2.0"),sQuery(id+"F0.wireOp",EDGE,"E2.1"),sQuery(id+"F0.wireOp",EDGE,"E2.2"),sQuery(id+"F0.wireOp",EDGE,"E2.3"),sQuery(id+"F0.wireOp",EDGE,"E2.4"),sQuery(id+"F0.wireOp",EDGE,"E2.5"),sQuery(id+"F0.wireOp",EDGE,"E3"),sQuery(id+"F0.wireOp",EDGE,"E4"),sQuery(id+"F0.wireOp",EDGE,"E5.0"),sQuery(id+"F0.wireOp",EDGE,"E5.1"),sQuery(id+"F0.wireOp",EDGE,"E5.3"),sQuery(id+"F0.wireOp",EDGE,"E5.4"),sQuery(id+"F0.wireOp",EDGE,"E5.5"),sQuery(id+"F0.wireOp",EDGE,"E6.trimOffspring"),sQuery(id+"F0.wireOp",EDGE,"E7.trimOffspring"),sQuery(id+"F0.wireOp",EDGE,"E9.trimOffspring"),sQuery(id+"F0.wireOp",EDGE,"E10.1.0"),sQuery(id+"F0.wireOp",EDGE,"E10.1.1"),sQuery(id+"F0.wireOp",EDGE,"E10.1.2"),sQuery(id+"F0.wireOp",EDGE,"E10.1.3"),sQuery(id+"F0.wireOp",EDGE,"E10.1.5"),sQuery(id+"F0.wireOp",EDGE,"E10.1.7"),sQuery(id+"F0.wireOp",EDGE,"E10.1.8"),sQuery(id+"F0.wireOp",EDGE,"E10.1.9"),sQuery(id+"F0.wireOp",EDGE,"E10.1.10"),sQuery(id+"F0.wireOp",EDGE,"E10.1.11"),sQuery(id+"F0.wireOp",EDGE,"E10.1.12"),sQuery(id+"F0.wireOp",EDGE,"E10.1.14"),sQuery(id+"F0.wireOp",EDGE,"E10.1.15"),sQuery(id+"F0.wireOp",EDGE,"E10.1.16"),sQuery(id+"F0.wireOp",EDGE,"E10.1.18"),sQuery(id+"F0.wireOp",EDGE,"E10.1.20"),sQuery(id+"F0.wireOp",EDGE,"E10.2.0"),sQuery(id+"F0.wireOp",EDGE,"E10.2.1"),sQuery(id+"F0.wireOp",EDGE,"E10.2.2"),sQuery(id+"F0.wireOp",EDGE,"E10.2.3"),sQuery(id+"F0.wireOp",EDGE,"E10.2.5"),sQuery(id+"F0.wireOp",EDGE,"E10.2.7"),sQuery(id+"F0.wireOp",EDGE,"E10.2.8"),sQuery(id+"F0.wireOp",EDGE,"E10.2.9"),sQuery(id+"F0.wireOp",EDGE,"E10.2.10"),sQuery(id+"F0.wireOp",EDGE,"E10.2.11"),sQuery(id+"F0.wireOp",EDGE,"E10.2.12"),sQuery(id+"F0.wireOp",EDGE,"E1"),sQuery(id+"F0.wireOp",EDGE,"E10.2.14"),sQuery(id+"F0.wireOp",EDGE,"E10.2.15"),sQuery(id+"F0.wireOp",EDGE,"E10.2.16"),sQuery(id+"F0.wireOp",EDGE,"E10.2.18"),sQuery(id+"F0.wireOp",EDGE,"E10.2.20"),sQuery(id+"F0.wireOp",EDGE,"E8.trimOffspring"),sQuery(id+"F0.wireOp",EDGE,"E0"),sQuery(id+"F0.wireOp",EDGE,"E10.1.6"),sQuery(id+"F0.wireOp",EDGE,"E11"),sQuery(id+"F0.wireOp",EDGE,"E12"),sQuery(id+"F0.wireOp",EDGE,"E13.1.0"),sQuery(id+"F0.wireOp",EDGE,"E13.1.1"),sQuery(id+"F0.wireOp",EDGE,"E13.2.0"),sQuery(id+"F0.wireOp",EDGE,"E13.2.1")])]}),"instanceName":"1"});
            var Q1;
            Q1=makeQuery(id+"F23.opPattern","COPY",EDGE,{"derivedFrom":makeQuery(id+"F1.opExtrude","CAP_EDGE",EDGE,{"disambiguationData":[OSD([sQuery(id+"F0.wireOp",EDGE,"E1")])],"isStart":false}),"instanceName":"1"});
            transform(context, id + "F25", {"entities" : qUnion([Q0]), "transformType" : TransformType.ROTATION, "transformAxis" : qUnion([Q1]), "angle" : 10 * degree, "oppositeDirection" : true, "makeCopy" : false});
        }
        {
            var Q0;
            Q0=makeQuery(id+"F23.opPattern","COPY",BODY,{"derivedFrom":makeQuery(id+"F1.opExtrude","SWEPT_BODY",BODY,{"disambiguationData":[OSD([sQuery(id+"F0.wireOp",EDGE,"E2.0"),sQuery(id+"F0.wireOp",EDGE,"E2.1"),sQuery(id+"F0.wireOp",EDGE,"E2.2"),sQuery(id+"F0.wireOp",EDGE,"E2.3"),sQuery(id+"F0.wireOp",EDGE,"E2.4"),sQuery(id+"F0.wireOp",EDGE,"E2.5"),sQuery(id+"F0.wireOp",EDGE,"E3"),sQuery(id+"F0.wireOp",EDGE,"E4"),sQuery(id+"F0.wireOp",EDGE,"E5.0"),sQuery(id+"F0.wireOp",EDGE,"E5.1"),sQuery(id+"F0.wireOp",EDGE,"E5.3"),sQuery(id+"F0.wireOp",EDGE,"E5.4"),sQuery(id+"F0.wireOp",EDGE,"E5.5"),sQuery(id+"F0.wireOp",EDGE,"E6.trimOffspring"),sQuery(id+"F0.wireOp",EDGE,"E7.trimOffspring"),sQuery(id+"F0.wireOp",EDGE,"E9.trimOffspring"),sQuery(id+"F0.wireOp",EDGE,"E10.1.0"),sQuery(id+"F0.wireOp",EDGE,"E10.1.1"),sQuery(id+"F0.wireOp",EDGE,"E10.1.2"),sQuery(id+"F0.wireOp",EDGE,"E10.1.3"),sQuery(id+"F0.wireOp",EDGE,"E10.1.5"),sQuery(id+"F0.wireOp",EDGE,"E10.1.7"),sQuery(id+"F0.wireOp",EDGE,"E10.1.8"),sQuery(id+"F0.wireOp",EDGE,"E10.1.9"),sQuery(id+"F0.wireOp",EDGE,"E10.1.10"),sQuery(id+"F0.wireOp",EDGE,"E10.1.11"),sQuery(id+"F0.wireOp",EDGE,"E10.1.12"),sQuery(id+"F0.wireOp",EDGE,"E10.1.14"),sQuery(id+"F0.wireOp",EDGE,"E10.1.15"),sQuery(id+"F0.wireOp",EDGE,"E10.1.16"),sQuery(id+"F0.wireOp",EDGE,"E10.1.18"),sQuery(id+"F0.wireOp",EDGE,"E10.1.20"),sQuery(id+"F0.wireOp",EDGE,"E10.2.0"),sQuery(id+"F0.wireOp",EDGE,"E10.2.1"),sQuery(id+"F0.wireOp",EDGE,"E10.2.2"),sQuery(id+"F0.wireOp",EDGE,"E10.2.3"),sQuery(id+"F0.wireOp",EDGE,"E10.2.5"),sQuery(id+"F0.wireOp",EDGE,"E10.2.7"),sQuery(id+"F0.wireOp",EDGE,"E10.2.8"),sQuery(id+"F0.wireOp",EDGE,"E10.2.9"),sQuery(id+"F0.wireOp",EDGE,"E10.2.10"),sQuery(id+"F0.wireOp",EDGE,"E10.2.11"),sQuery(id+"F0.wireOp",EDGE,"E10.2.12"),sQuery(id+"F0.wireOp",EDGE,"E1"),sQuery(id+"F0.wireOp",EDGE,"E10.2.14"),sQuery(id+"F0.wireOp",EDGE,"E10.2.15"),sQuery(id+"F0.wireOp",EDGE,"E10.2.16"),sQuery(id+"F0.wireOp",EDGE,"E10.2.18"),sQuery(id+"F0.wireOp",EDGE,"E10.2.20"),sQuery(id+"F0.wireOp",EDGE,"E8.trimOffspring"),sQuery(id+"F0.wireOp",EDGE,"E0"),sQuery(id+"F0.wireOp",EDGE,"E10.1.6"),sQuery(id+"F0.wireOp",EDGE,"E11"),sQuery(id+"F0.wireOp",EDGE,"E12"),sQuery(id+"F0.wireOp",EDGE,"E13.1.0"),sQuery(id+"F0.wireOp",EDGE,"E13.1.1"),sQuery(id+"F0.wireOp",EDGE,"E13.2.0"),sQuery(id+"F0.wireOp",EDGE,"E13.2.1")])]}),"instanceName":"1"});
            transform(context, id + "F26", {"entities" : qUnion([Q0]), "transformType" : TransformType.TRANSLATION_3D, "dx" : 0 * mm, "dy" : 1.1 * mm, "dz" : 0 * mm, "makeCopy" : false});
        }
        {
            var Q0;
            Q0=makeQuery(id+"F23.opPattern","COPY",BODY,{"derivedFrom":makeQuery(id+"F5.opPattern","COPY",BODY,{"derivedFrom":makeQuery(id+"F1.opExtrude","SWEPT_BODY",BODY,{"disambiguationData":[OSD([sQuery(id+"F0.wireOp",EDGE,"E2.0"),sQuery(id+"F0.wireOp",EDGE,"E2.1"),sQuery(id+"F0.wireOp",EDGE,"E2.2"),sQuery(id+"F0.wireOp",EDGE,"E2.3"),sQuery(id+"F0.wireOp",EDGE,"E2.4"),sQuery(id+"F0.wireOp",EDGE,"E2.5"),sQuery(id+"F0.wireOp",EDGE,"E3"),sQuery(id+"F0.wireOp",EDGE,"E4"),sQuery(id+"F0.wireOp",EDGE,"E5.0"),sQuery(id+"F0.wireOp",EDGE,"E5.1"),sQuery(id+"F0.wireOp",EDGE,"E5.3"),sQuery(id+"F0.wireOp",EDGE,"E5.4"),sQuery(id+"F0.wireOp",EDGE,"E5.5"),sQuery(id+"F0.wireOp",EDGE,"E6.trimOffspring"),sQuery(id+"F0.wireOp",EDGE,"E7.trimOffspring"),sQuery(id+"F0.wireOp",EDGE,"E9.trimOffspring"),sQuery(id+"F0.wireOp",EDGE,"E10.1.0"),sQuery(id+"F0.wireOp",EDGE,"E10.1.1"),sQuery(id+"F0.wireOp",EDGE,"E10.1.2"),sQuery(id+"F0.wireOp",EDGE,"E10.1.3"),sQuery(id+"F0.wireOp",EDGE,"E10.1.5"),sQuery(id+"F0.wireOp",EDGE,"E10.1.7"),sQuery(id+"F0.wireOp",EDGE,"E10.1.8"),sQuery(id+"F0.wireOp",EDGE,"E10.1.9"),sQuery(id+"F0.wireOp",EDGE,"E10.1.10"),sQuery(id+"F0.wireOp",EDGE,"E10.1.11"),sQuery(id+"F0.wireOp",EDGE,"E10.1.12"),sQuery(id+"F0.wireOp",EDGE,"E10.1.14"),sQuery(id+"F0.wireOp",EDGE,"E10.1.15"),sQuery(id+"F0.wireOp",EDGE,"E10.1.16"),sQuery(id+"F0.wireOp",EDGE,"E10.1.18"),sQuery(id+"F0.wireOp",EDGE,"E10.1.20"),sQuery(id+"F0.wireOp",EDGE,"E10.2.0"),sQuery(id+"F0.wireOp",EDGE,"E10.2.1"),sQuery(id+"F0.wireOp",EDGE,"E10.2.2"),sQuery(id+"F0.wireOp",EDGE,"E10.2.3"),sQuery(id+"F0.wireOp",EDGE,"E10.2.5"),sQuery(id+"F0.wireOp",EDGE,"E10.2.7"),sQuery(id+"F0.wireOp",EDGE,"E10.2.8"),sQuery(id+"F0.wireOp",EDGE,"E10.2.9"),sQuery(id+"F0.wireOp",EDGE,"E10.2.10"),sQuery(id+"F0.wireOp",EDGE,"E10.2.11"),sQuery(id+"F0.wireOp",EDGE,"E10.2.12"),sQuery(id+"F0.wireOp",EDGE,"E1"),sQuery(id+"F0.wireOp",EDGE,"E10.2.14"),sQuery(id+"F0.wireOp",EDGE,"E10.2.15"),sQuery(id+"F0.wireOp",EDGE,"E10.2.16"),sQuery(id+"F0.wireOp",EDGE,"E10.2.18"),sQuery(id+"F0.wireOp",EDGE,"E10.2.20"),sQuery(id+"F0.wireOp",EDGE,"E8.trimOffspring"),sQuery(id+"F0.wireOp",EDGE,"E0"),sQuery(id+"F0.wireOp",EDGE,"E10.1.6"),sQuery(id+"F0.wireOp",EDGE,"E11"),sQuery(id+"F0.wireOp",EDGE,"E12"),sQuery(id+"F0.wireOp",EDGE,"E13.1.0"),sQuery(id+"F0.wireOp",EDGE,"E13.1.1"),sQuery(id+"F0.wireOp",EDGE,"E13.2.0"),sQuery(id+"F0.wireOp",EDGE,"E13.2.1")])]}),"instanceName":"1"}),"instanceName":"1"});
            transform(context, id + "F27", {"entities" : qUnion([Q0]), "transformType" : TransformType.TRANSLATION_3D, "dx" : 0.2 * mm, "dy" : -4.8 * mm, "dz" : 0 * mm, "makeCopy" : false});
        }
        {
            var Q0;
            Q0=makeQuery(id+"F23.opPattern","COPY",BODY,{"derivedFrom":makeQuery(id+"F7.opPattern","COPY",BODY,{"derivedFrom":makeQuery(id+"F1.opExtrude","SWEPT_BODY",BODY,{"disambiguationData":[OSD([sQuery(id+"F0.wireOp",EDGE,"E2.0"),sQuery(id+"F0.wireOp",EDGE,"E2.1"),sQuery(id+"F0.wireOp",EDGE,"E2.2"),sQuery(id+"F0.wireOp",EDGE,"E2.3"),sQuery(id+"F0.wireOp",EDGE,"E2.4"),sQuery(id+"F0.wireOp",EDGE,"E2.5"),sQuery(id+"F0.wireOp",EDGE,"E3"),sQuery(id+"F0.wireOp",EDGE,"E4"),sQuery(id+"F0.wireOp",EDGE,"E5.0"),sQuery(id+"F0.wireOp",EDGE,"E5.1"),sQuery(id+"F0.wireOp",EDGE,"E5.3"),sQuery(id+"F0.wireOp",EDGE,"E5.4"),sQuery(id+"F0.wireOp",EDGE,"E5.5"),sQuery(id+"F0.wireOp",EDGE,"E6.trimOffspring"),sQuery(id+"F0.wireOp",EDGE,"E7.trimOffspring"),sQuery(id+"F0.wireOp",EDGE,"E9.trimOffspring"),sQuery(id+"F0.wireOp",EDGE,"E10.1.0"),sQuery(id+"F0.wireOp",EDGE,"E10.1.1"),sQuery(id+"F0.wireOp",EDGE,"E10.1.2"),sQuery(id+"F0.wireOp",EDGE,"E10.1.3"),sQuery(id+"F0.wireOp",EDGE,"E10.1.5"),sQuery(id+"F0.wireOp",EDGE,"E10.1.7"),sQuery(id+"F0.wireOp",EDGE,"E10.1.8"),sQuery(id+"F0.wireOp",EDGE,"E10.1.9"),sQuery(id+"F0.wireOp",EDGE,"E10.1.10"),sQuery(id+"F0.wireOp",EDGE,"E10.1.11"),sQuery(id+"F0.wireOp",EDGE,"E10.1.12"),sQuery(id+"F0.wireOp",EDGE,"E10.1.14"),sQuery(id+"F0.wireOp",EDGE,"E10.1.15"),sQuery(id+"F0.wireOp",EDGE,"E10.1.16"),sQuery(id+"F0.wireOp",EDGE,"E10.1.18"),sQuery(id+"F0.wireOp",EDGE,"E10.1.20"),sQuery(id+"F0.wireOp",EDGE,"E10.2.0"),sQuery(id+"F0.wireOp",EDGE,"E10.2.1"),sQuery(id+"F0.wireOp",EDGE,"E10.2.2"),sQuery(id+"F0.wireOp",EDGE,"E10.2.3"),sQuery(id+"F0.wireOp",EDGE,"E10.2.5"),sQuery(id+"F0.wireOp",EDGE,"E10.2.7"),sQuery(id+"F0.wireOp",EDGE,"E10.2.8"),sQuery(id+"F0.wireOp",EDGE,"E10.2.9"),sQuery(id+"F0.wireOp",EDGE,"E10.2.10"),sQuery(id+"F0.wireOp",EDGE,"E10.2.11"),sQuery(id+"F0.wireOp",EDGE,"E10.2.12"),sQuery(id+"F0.wireOp",EDGE,"E1"),sQuery(id+"F0.wireOp",EDGE,"E10.2.14"),sQuery(id+"F0.wireOp",EDGE,"E10.2.15"),sQuery(id+"F0.wireOp",EDGE,"E10.2.16"),sQuery(id+"F0.wireOp",EDGE,"E10.2.18"),sQuery(id+"F0.wireOp",EDGE,"E10.2.20"),sQuery(id+"F0.wireOp",EDGE,"E8.trimOffspring"),sQuery(id+"F0.wireOp",EDGE,"E0"),sQuery(id+"F0.wireOp",EDGE,"E10.1.6"),sQuery(id+"F0.wireOp",EDGE,"E11"),sQuery(id+"F0.wireOp",EDGE,"E12"),sQuery(id+"F0.wireOp",EDGE,"E13.1.0"),sQuery(id+"F0.wireOp",EDGE,"E13.1.1"),sQuery(id+"F0.wireOp",EDGE,"E13.2.0"),sQuery(id+"F0.wireOp",EDGE,"E13.2.1")])]}),"instanceName":"1"}),"instanceName":"1"});
            var Q1;
            Q1=makeQuery(id+"F23.opPattern","COPY",EDGE,{"derivedFrom":makeQuery(id+"F7.opPattern","COPY",EDGE,{"derivedFrom":makeQuery(id+"F1.opExtrude","CAP_EDGE",EDGE,{"disambiguationData":[OSD([sQuery(id+"F0.wireOp",EDGE,"E1")])],"isStart":false}),"instanceName":"1"}),"instanceName":"1"});
            transform(context, id + "F28", {"entities" : qUnion([Q0]), "transformType" : TransformType.ROTATION, "transformAxis" : qUnion([Q1]), "angle" : 42 * degree, "makeCopy" : false});
        }
        {
            var Q0;
            Q0=makeQuery(id+"F23.opPattern","COPY",BODY,{"derivedFrom":makeQuery(id+"F7.opPattern","COPY",BODY,{"derivedFrom":makeQuery(id+"F1.opExtrude","SWEPT_BODY",BODY,{"disambiguationData":[OSD([sQuery(id+"F0.wireOp",EDGE,"E2.0"),sQuery(id+"F0.wireOp",EDGE,"E2.1"),sQuery(id+"F0.wireOp",EDGE,"E2.2"),sQuery(id+"F0.wireOp",EDGE,"E2.3"),sQuery(id+"F0.wireOp",EDGE,"E2.4"),sQuery(id+"F0.wireOp",EDGE,"E2.5"),sQuery(id+"F0.wireOp",EDGE,"E3"),sQuery(id+"F0.wireOp",EDGE,"E4"),sQuery(id+"F0.wireOp",EDGE,"E5.0"),sQuery(id+"F0.wireOp",EDGE,"E5.1"),sQuery(id+"F0.wireOp",EDGE,"E5.3"),sQuery(id+"F0.wireOp",EDGE,"E5.4"),sQuery(id+"F0.wireOp",EDGE,"E5.5"),sQuery(id+"F0.wireOp",EDGE,"E6.trimOffspring"),sQuery(id+"F0.wireOp",EDGE,"E7.trimOffspring"),sQuery(id+"F0.wireOp",EDGE,"E9.trimOffspring"),sQuery(id+"F0.wireOp",EDGE,"E10.1.0"),sQuery(id+"F0.wireOp",EDGE,"E10.1.1"),sQuery(id+"F0.wireOp",EDGE,"E10.1.2"),sQuery(id+"F0.wireOp",EDGE,"E10.1.3"),sQuery(id+"F0.wireOp",EDGE,"E10.1.5"),sQuery(id+"F0.wireOp",EDGE,"E10.1.7"),sQuery(id+"F0.wireOp",EDGE,"E10.1.8"),sQuery(id+"F0.wireOp",EDGE,"E10.1.9"),sQuery(id+"F0.wireOp",EDGE,"E10.1.10"),sQuery(id+"F0.wireOp",EDGE,"E10.1.11"),sQuery(id+"F0.wireOp",EDGE,"E10.1.12"),sQuery(id+"F0.wireOp",EDGE,"E10.1.14"),sQuery(id+"F0.wireOp",EDGE,"E10.1.15"),sQuery(id+"F0.wireOp",EDGE,"E10.1.16"),sQuery(id+"F0.wireOp",EDGE,"E10.1.18"),sQuery(id+"F0.wireOp",EDGE,"E10.1.20"),sQuery(id+"F0.wireOp",EDGE,"E10.2.0"),sQuery(id+"F0.wireOp",EDGE,"E10.2.1"),sQuery(id+"F0.wireOp",EDGE,"E10.2.2"),sQuery(id+"F0.wireOp",EDGE,"E10.2.3"),sQuery(id+"F0.wireOp",EDGE,"E10.2.5"),sQuery(id+"F0.wireOp",EDGE,"E10.2.7"),sQuery(id+"F0.wireOp",EDGE,"E10.2.8"),sQuery(id+"F0.wireOp",EDGE,"E10.2.9"),sQuery(id+"F0.wireOp",EDGE,"E10.2.10"),sQuery(id+"F0.wireOp",EDGE,"E10.2.11"),sQuery(id+"F0.wireOp",EDGE,"E10.2.12"),sQuery(id+"F0.wireOp",EDGE,"E1"),sQuery(id+"F0.wireOp",EDGE,"E10.2.14"),sQuery(id+"F0.wireOp",EDGE,"E10.2.15"),sQuery(id+"F0.wireOp",EDGE,"E10.2.16"),sQuery(id+"F0.wireOp",EDGE,"E10.2.18"),sQuery(id+"F0.wireOp",EDGE,"E10.2.20"),sQuery(id+"F0.wireOp",EDGE,"E8.trimOffspring"),sQuery(id+"F0.wireOp",EDGE,"E0"),sQuery(id+"F0.wireOp",EDGE,"E10.1.6"),sQuery(id+"F0.wireOp",EDGE,"E11"),sQuery(id+"F0.wireOp",EDGE,"E12"),sQuery(id+"F0.wireOp",EDGE,"E13.1.0"),sQuery(id+"F0.wireOp",EDGE,"E13.1.1"),sQuery(id+"F0.wireOp",EDGE,"E13.2.0"),sQuery(id+"F0.wireOp",EDGE,"E13.2.1")])]}),"instanceName":"1"}),"instanceName":"1"});
            var Q1;
            Q1=makeQuery(id+"F23.opPattern","COPY",EDGE,{"derivedFrom":makeQuery(id+"F7.opPattern","COPY",EDGE,{"derivedFrom":makeQuery(id+"F1.opExtrude","CAP_EDGE",EDGE,{"disambiguationData":[OSD([sQuery(id+"F0.wireOp",EDGE,"E1")])],"isStart":false}),"instanceName":"1"}),"instanceName":"1"});
            transform(context, id + "F29", {"entities" : qUnion([Q0]), "transformType" : TransformType.ROTATION, "transformAxis" : qUnion([Q1]), "angle" : 82 * degree, "oppositeDirection" : true, "makeCopy" : false});
        }
        {
            var Q0;
            Q0=makeQuery(id+"F23.opPattern","COPY",BODY,{"derivedFrom":makeQuery(id+"F7.opPattern","COPY",BODY,{"derivedFrom":makeQuery(id+"F1.opExtrude","SWEPT_BODY",BODY,{"disambiguationData":[OSD([sQuery(id+"F0.wireOp",EDGE,"E2.0"),sQuery(id+"F0.wireOp",EDGE,"E2.1"),sQuery(id+"F0.wireOp",EDGE,"E2.2"),sQuery(id+"F0.wireOp",EDGE,"E2.3"),sQuery(id+"F0.wireOp",EDGE,"E2.4"),sQuery(id+"F0.wireOp",EDGE,"E2.5"),sQuery(id+"F0.wireOp",EDGE,"E3"),sQuery(id+"F0.wireOp",EDGE,"E4"),sQuery(id+"F0.wireOp",EDGE,"E5.0"),sQuery(id+"F0.wireOp",EDGE,"E5.1"),sQuery(id+"F0.wireOp",EDGE,"E5.3"),sQuery(id+"F0.wireOp",EDGE,"E5.4"),sQuery(id+"F0.wireOp",EDGE,"E5.5"),sQuery(id+"F0.wireOp",EDGE,"E6.trimOffspring"),sQuery(id+"F0.wireOp",EDGE,"E7.trimOffspring"),sQuery(id+"F0.wireOp",EDGE,"E9.trimOffspring"),sQuery(id+"F0.wireOp",EDGE,"E10.1.0"),sQuery(id+"F0.wireOp",EDGE,"E10.1.1"),sQuery(id+"F0.wireOp",EDGE,"E10.1.2"),sQuery(id+"F0.wireOp",EDGE,"E10.1.3"),sQuery(id+"F0.wireOp",EDGE,"E10.1.5"),sQuery(id+"F0.wireOp",EDGE,"E10.1.7"),sQuery(id+"F0.wireOp",EDGE,"E10.1.8"),sQuery(id+"F0.wireOp",EDGE,"E10.1.9"),sQuery(id+"F0.wireOp",EDGE,"E10.1.10"),sQuery(id+"F0.wireOp",EDGE,"E10.1.11"),sQuery(id+"F0.wireOp",EDGE,"E10.1.12"),sQuery(id+"F0.wireOp",EDGE,"E10.1.14"),sQuery(id+"F0.wireOp",EDGE,"E10.1.15"),sQuery(id+"F0.wireOp",EDGE,"E10.1.16"),sQuery(id+"F0.wireOp",EDGE,"E10.1.18"),sQuery(id+"F0.wireOp",EDGE,"E10.1.20"),sQuery(id+"F0.wireOp",EDGE,"E10.2.0"),sQuery(id+"F0.wireOp",EDGE,"E10.2.1"),sQuery(id+"F0.wireOp",EDGE,"E10.2.2"),sQuery(id+"F0.wireOp",EDGE,"E10.2.3"),sQuery(id+"F0.wireOp",EDGE,"E10.2.5"),sQuery(id+"F0.wireOp",EDGE,"E10.2.7"),sQuery(id+"F0.wireOp",EDGE,"E10.2.8"),sQuery(id+"F0.wireOp",EDGE,"E10.2.9"),sQuery(id+"F0.wireOp",EDGE,"E10.2.10"),sQuery(id+"F0.wireOp",EDGE,"E10.2.11"),sQuery(id+"F0.wireOp",EDGE,"E10.2.12"),sQuery(id+"F0.wireOp",EDGE,"E1"),sQuery(id+"F0.wireOp",EDGE,"E10.2.14"),sQuery(id+"F0.wireOp",EDGE,"E10.2.15"),sQuery(id+"F0.wireOp",EDGE,"E10.2.16"),sQuery(id+"F0.wireOp",EDGE,"E10.2.18"),sQuery(id+"F0.wireOp",EDGE,"E10.2.20"),sQuery(id+"F0.wireOp",EDGE,"E8.trimOffspring"),sQuery(id+"F0.wireOp",EDGE,"E0"),sQuery(id+"F0.wireOp",EDGE,"E10.1.6"),sQuery(id+"F0.wireOp",EDGE,"E11"),sQuery(id+"F0.wireOp",EDGE,"E12"),sQuery(id+"F0.wireOp",EDGE,"E13.1.0"),sQuery(id+"F0.wireOp",EDGE,"E13.1.1"),sQuery(id+"F0.wireOp",EDGE,"E13.2.0"),sQuery(id+"F0.wireOp",EDGE,"E13.2.1")])]}),"instanceName":"1"}),"instanceName":"1"});
            transform(context, id + "F30", {"entities" : qUnion([Q0]), "transformType" : TransformType.TRANSLATION_3D, "dx" : 2.4 * mm, "dy" : -4.7 * mm, "dz" : 0 * mm, "makeCopy" : false});
        }
        {
            var Q0;
            Q0=makeQuery(id+"F23.opPattern","COPY",BODY,{"derivedFrom":makeQuery(id+"F8.opPattern","COPY",BODY,{"derivedFrom":makeQuery(id+"F7.opPattern","COPY",BODY,{"derivedFrom":makeQuery(id+"F1.opExtrude","SWEPT_BODY",BODY,{"disambiguationData":[OSD([sQuery(id+"F0.wireOp",EDGE,"E2.0"),sQuery(id+"F0.wireOp",EDGE,"E2.1"),sQuery(id+"F0.wireOp",EDGE,"E2.2"),sQuery(id+"F0.wireOp",EDGE,"E2.3"),sQuery(id+"F0.wireOp",EDGE,"E2.4"),sQuery(id+"F0.wireOp",EDGE,"E2.5"),sQuery(id+"F0.wireOp",EDGE,"E3"),sQuery(id+"F0.wireOp",EDGE,"E4"),sQuery(id+"F0.wireOp",EDGE,"E5.0"),sQuery(id+"F0.wireOp",EDGE,"E5.1"),sQuery(id+"F0.wireOp",EDGE,"E5.3"),sQuery(id+"F0.wireOp",EDGE,"E5.4"),sQuery(id+"F0.wireOp",EDGE,"E5.5"),sQuery(id+"F0.wireOp",EDGE,"E6.trimOffspring"),sQuery(id+"F0.wireOp",EDGE,"E7.trimOffspring"),sQuery(id+"F0.wireOp",EDGE,"E9.trimOffspring"),sQuery(id+"F0.wireOp",EDGE,"E10.1.0"),sQuery(id+"F0.wireOp",EDGE,"E10.1.1"),sQuery(id+"F0.wireOp",EDGE,"E10.1.2"),sQuery(id+"F0.wireOp",EDGE,"E10.1.3"),sQuery(id+"F0.wireOp",EDGE,"E10.1.5"),sQuery(id+"F0.wireOp",EDGE,"E10.1.7"),sQuery(id+"F0.wireOp",EDGE,"E10.1.8"),sQuery(id+"F0.wireOp",EDGE,"E10.1.9"),sQuery(id+"F0.wireOp",EDGE,"E10.1.10"),sQuery(id+"F0.wireOp",EDGE,"E10.1.11"),sQuery(id+"F0.wireOp",EDGE,"E10.1.12"),sQuery(id+"F0.wireOp",EDGE,"E10.1.14"),sQuery(id+"F0.wireOp",EDGE,"E10.1.15"),sQuery(id+"F0.wireOp",EDGE,"E10.1.16"),sQuery(id+"F0.wireOp",EDGE,"E10.1.18"),sQuery(id+"F0.wireOp",EDGE,"E10.1.20"),sQuery(id+"F0.wireOp",EDGE,"E10.2.0"),sQuery(id+"F0.wireOp",EDGE,"E10.2.1"),sQuery(id+"F0.wireOp",EDGE,"E10.2.2"),sQuery(id+"F0.wireOp",EDGE,"E10.2.3"),sQuery(id+"F0.wireOp",EDGE,"E10.2.5"),sQuery(id+"F0.wireOp",EDGE,"E10.2.7"),sQuery(id+"F0.wireOp",EDGE,"E10.2.8"),sQuery(id+"F0.wireOp",EDGE,"E10.2.9"),sQuery(id+"F0.wireOp",EDGE,"E10.2.10"),sQuery(id+"F0.wireOp",EDGE,"E10.2.11"),sQuery(id+"F0.wireOp",EDGE,"E10.2.12"),sQuery(id+"F0.wireOp",EDGE,"E1"),sQuery(id+"F0.wireOp",EDGE,"E10.2.14"),sQuery(id+"F0.wireOp",EDGE,"E10.2.15"),sQuery(id+"F0.wireOp",EDGE,"E10.2.16"),sQuery(id+"F0.wireOp",EDGE,"E10.2.18"),sQuery(id+"F0.wireOp",EDGE,"E10.2.20"),sQuery(id+"F0.wireOp",EDGE,"E8.trimOffspring"),sQuery(id+"F0.wireOp",EDGE,"E0"),sQuery(id+"F0.wireOp",EDGE,"E10.1.6"),sQuery(id+"F0.wireOp",EDGE,"E11"),sQuery(id+"F0.wireOp",EDGE,"E12"),sQuery(id+"F0.wireOp",EDGE,"E13.1.0"),sQuery(id+"F0.wireOp",EDGE,"E13.1.1"),sQuery(id+"F0.wireOp",EDGE,"E13.2.0"),sQuery(id+"F0.wireOp",EDGE,"E13.2.1")])]}),"instanceName":"1"}),"instanceName":"1"}),"instanceName":"1"});
            var Q1;
            Q1=makeQuery(id+"F23.opPattern","COPY",EDGE,{"derivedFrom":makeQuery(id+"F8.opPattern","COPY",EDGE,{"derivedFrom":makeQuery(id+"F7.opPattern","COPY",EDGE,{"derivedFrom":makeQuery(id+"F1.opExtrude","CAP_EDGE",EDGE,{"disambiguationData":[OSD([sQuery(id+"F0.wireOp",EDGE,"E1")])],"isStart":false}),"instanceName":"1"}),"instanceName":"1"}),"instanceName":"1"});
            transform(context, id + "F31", {"entities" : qUnion([Q0]), "transformType" : TransformType.ROTATION, "transformAxis" : qUnion([Q1]), "angle" : 82 * degree, "makeCopy" : false});
        }
        {
            var Q0;
            Q0=makeQuery(id+"F23.opPattern","COPY",BODY,{"derivedFrom":makeQuery(id+"F8.opPattern","COPY",BODY,{"derivedFrom":makeQuery(id+"F7.opPattern","COPY",BODY,{"derivedFrom":makeQuery(id+"F1.opExtrude","SWEPT_BODY",BODY,{"disambiguationData":[OSD([sQuery(id+"F0.wireOp",EDGE,"E2.0"),sQuery(id+"F0.wireOp",EDGE,"E2.1"),sQuery(id+"F0.wireOp",EDGE,"E2.2"),sQuery(id+"F0.wireOp",EDGE,"E2.3"),sQuery(id+"F0.wireOp",EDGE,"E2.4"),sQuery(id+"F0.wireOp",EDGE,"E2.5"),sQuery(id+"F0.wireOp",EDGE,"E3"),sQuery(id+"F0.wireOp",EDGE,"E4"),sQuery(id+"F0.wireOp",EDGE,"E5.0"),sQuery(id+"F0.wireOp",EDGE,"E5.1"),sQuery(id+"F0.wireOp",EDGE,"E5.3"),sQuery(id+"F0.wireOp",EDGE,"E5.4"),sQuery(id+"F0.wireOp",EDGE,"E5.5"),sQuery(id+"F0.wireOp",EDGE,"E6.trimOffspring"),sQuery(id+"F0.wireOp",EDGE,"E7.trimOffspring"),sQuery(id+"F0.wireOp",EDGE,"E9.trimOffspring"),sQuery(id+"F0.wireOp",EDGE,"E10.1.0"),sQuery(id+"F0.wireOp",EDGE,"E10.1.1"),sQuery(id+"F0.wireOp",EDGE,"E10.1.2"),sQuery(id+"F0.wireOp",EDGE,"E10.1.3"),sQuery(id+"F0.wireOp",EDGE,"E10.1.5"),sQuery(id+"F0.wireOp",EDGE,"E10.1.7"),sQuery(id+"F0.wireOp",EDGE,"E10.1.8"),sQuery(id+"F0.wireOp",EDGE,"E10.1.9"),sQuery(id+"F0.wireOp",EDGE,"E10.1.10"),sQuery(id+"F0.wireOp",EDGE,"E10.1.11"),sQuery(id+"F0.wireOp",EDGE,"E10.1.12"),sQuery(id+"F0.wireOp",EDGE,"E10.1.14"),sQuery(id+"F0.wireOp",EDGE,"E10.1.15"),sQuery(id+"F0.wireOp",EDGE,"E10.1.16"),sQuery(id+"F0.wireOp",EDGE,"E10.1.18"),sQuery(id+"F0.wireOp",EDGE,"E10.1.20"),sQuery(id+"F0.wireOp",EDGE,"E10.2.0"),sQuery(id+"F0.wireOp",EDGE,"E10.2.1"),sQuery(id+"F0.wireOp",EDGE,"E10.2.2"),sQuery(id+"F0.wireOp",EDGE,"E10.2.3"),sQuery(id+"F0.wireOp",EDGE,"E10.2.5"),sQuery(id+"F0.wireOp",EDGE,"E10.2.7"),sQuery(id+"F0.wireOp",EDGE,"E10.2.8"),sQuery(id+"F0.wireOp",EDGE,"E10.2.9"),sQuery(id+"F0.wireOp",EDGE,"E10.2.10"),sQuery(id+"F0.wireOp",EDGE,"E10.2.11"),sQuery(id+"F0.wireOp",EDGE,"E10.2.12"),sQuery(id+"F0.wireOp",EDGE,"E1"),sQuery(id+"F0.wireOp",EDGE,"E10.2.14"),sQuery(id+"F0.wireOp",EDGE,"E10.2.15"),sQuery(id+"F0.wireOp",EDGE,"E10.2.16"),sQuery(id+"F0.wireOp",EDGE,"E10.2.18"),sQuery(id+"F0.wireOp",EDGE,"E10.2.20"),sQuery(id+"F0.wireOp",EDGE,"E8.trimOffspring"),sQuery(id+"F0.wireOp",EDGE,"E0"),sQuery(id+"F0.wireOp",EDGE,"E10.1.6"),sQuery(id+"F0.wireOp",EDGE,"E11"),sQuery(id+"F0.wireOp",EDGE,"E12"),sQuery(id+"F0.wireOp",EDGE,"E13.1.0"),sQuery(id+"F0.wireOp",EDGE,"E13.1.1"),sQuery(id+"F0.wireOp",EDGE,"E13.2.0"),sQuery(id+"F0.wireOp",EDGE,"E13.2.1")])]}),"instanceName":"1"}),"instanceName":"1"}),"instanceName":"1"});
            transform(context, id + "F32", {"entities" : qUnion([Q0]), "transformType" : TransformType.TRANSLATION_3D, "dx" : 3.2 * mm, "dy" : -4.7 * mm, "dz" : 0 * mm, "makeCopy" : false});
        }
        {
            var Q0;
            Q0=makeQuery(id+"F23.opPattern","COPY",BODY,{"derivedFrom":makeQuery(id+"F8.opPattern","COPY",BODY,{"derivedFrom":makeQuery(id+"F7.opPattern","COPY",BODY,{"derivedFrom":makeQuery(id+"F1.opExtrude","SWEPT_BODY",BODY,{"disambiguationData":[OSD([sQuery(id+"F0.wireOp",EDGE,"E2.0"),sQuery(id+"F0.wireOp",EDGE,"E2.1"),sQuery(id+"F0.wireOp",EDGE,"E2.2"),sQuery(id+"F0.wireOp",EDGE,"E2.3"),sQuery(id+"F0.wireOp",EDGE,"E2.4"),sQuery(id+"F0.wireOp",EDGE,"E2.5"),sQuery(id+"F0.wireOp",EDGE,"E3"),sQuery(id+"F0.wireOp",EDGE,"E4"),sQuery(id+"F0.wireOp",EDGE,"E5.0"),sQuery(id+"F0.wireOp",EDGE,"E5.1"),sQuery(id+"F0.wireOp",EDGE,"E5.3"),sQuery(id+"F0.wireOp",EDGE,"E5.4"),sQuery(id+"F0.wireOp",EDGE,"E5.5"),sQuery(id+"F0.wireOp",EDGE,"E6.trimOffspring"),sQuery(id+"F0.wireOp",EDGE,"E7.trimOffspring"),sQuery(id+"F0.wireOp",EDGE,"E9.trimOffspring"),sQuery(id+"F0.wireOp",EDGE,"E10.1.0"),sQuery(id+"F0.wireOp",EDGE,"E10.1.1"),sQuery(id+"F0.wireOp",EDGE,"E10.1.2"),sQuery(id+"F0.wireOp",EDGE,"E10.1.3"),sQuery(id+"F0.wireOp",EDGE,"E10.1.5"),sQuery(id+"F0.wireOp",EDGE,"E10.1.7"),sQuery(id+"F0.wireOp",EDGE,"E10.1.8"),sQuery(id+"F0.wireOp",EDGE,"E10.1.9"),sQuery(id+"F0.wireOp",EDGE,"E10.1.10"),sQuery(id+"F0.wireOp",EDGE,"E10.1.11"),sQuery(id+"F0.wireOp",EDGE,"E10.1.12"),sQuery(id+"F0.wireOp",EDGE,"E10.1.14"),sQuery(id+"F0.wireOp",EDGE,"E10.1.15"),sQuery(id+"F0.wireOp",EDGE,"E10.1.16"),sQuery(id+"F0.wireOp",EDGE,"E10.1.18"),sQuery(id+"F0.wireOp",EDGE,"E10.1.20"),sQuery(id+"F0.wireOp",EDGE,"E10.2.0"),sQuery(id+"F0.wireOp",EDGE,"E10.2.1"),sQuery(id+"F0.wireOp",EDGE,"E10.2.2"),sQuery(id+"F0.wireOp",EDGE,"E10.2.3"),sQuery(id+"F0.wireOp",EDGE,"E10.2.5"),sQuery(id+"F0.wireOp",EDGE,"E10.2.7"),sQuery(id+"F0.wireOp",EDGE,"E10.2.8"),sQuery(id+"F0.wireOp",EDGE,"E10.2.9"),sQuery(id+"F0.wireOp",EDGE,"E10.2.10"),sQuery(id+"F0.wireOp",EDGE,"E10.2.11"),sQuery(id+"F0.wireOp",EDGE,"E10.2.12"),sQuery(id+"F0.wireOp",EDGE,"E1"),sQuery(id+"F0.wireOp",EDGE,"E10.2.14"),sQuery(id+"F0.wireOp",EDGE,"E10.2.15"),sQuery(id+"F0.wireOp",EDGE,"E10.2.16"),sQuery(id+"F0.wireOp",EDGE,"E10.2.18"),sQuery(id+"F0.wireOp",EDGE,"E10.2.20"),sQuery(id+"F0.wireOp",EDGE,"E8.trimOffspring"),sQuery(id+"F0.wireOp",EDGE,"E0"),sQuery(id+"F0.wireOp",EDGE,"E10.1.6"),sQuery(id+"F0.wireOp",EDGE,"E11"),sQuery(id+"F0.wireOp",EDGE,"E12"),sQuery(id+"F0.wireOp",EDGE,"E13.1.0"),sQuery(id+"F0.wireOp",EDGE,"E13.1.1"),sQuery(id+"F0.wireOp",EDGE,"E13.2.0"),sQuery(id+"F0.wireOp",EDGE,"E13.2.1")])]}),"instanceName":"1"}),"instanceName":"1"}),"instanceName":"1"});
            transform(context, id + "F33", {"entities" : qUnion([Q0]), "transformType" : TransformType.TRANSLATION_3D, "dx" : 119 * mm, "dy" : -8 * mm, "dz" : 0 * mm, "makeCopy" : false});
        }
        {
            var Q0;
            Q0=makeQuery(id+"F23.opPattern","COPY",BODY,{"derivedFrom":makeQuery(id+"F8.opPattern","COPY",BODY,{"derivedFrom":makeQuery(id+"F7.opPattern","COPY",BODY,{"derivedFrom":makeQuery(id+"F1.opExtrude","SWEPT_BODY",BODY,{"disambiguationData":[OSD([sQuery(id+"F0.wireOp",EDGE,"E2.0"),sQuery(id+"F0.wireOp",EDGE,"E2.1"),sQuery(id+"F0.wireOp",EDGE,"E2.2"),sQuery(id+"F0.wireOp",EDGE,"E2.3"),sQuery(id+"F0.wireOp",EDGE,"E2.4"),sQuery(id+"F0.wireOp",EDGE,"E2.5"),sQuery(id+"F0.wireOp",EDGE,"E3"),sQuery(id+"F0.wireOp",EDGE,"E4"),sQuery(id+"F0.wireOp",EDGE,"E5.0"),sQuery(id+"F0.wireOp",EDGE,"E5.1"),sQuery(id+"F0.wireOp",EDGE,"E5.3"),sQuery(id+"F0.wireOp",EDGE,"E5.4"),sQuery(id+"F0.wireOp",EDGE,"E5.5"),sQuery(id+"F0.wireOp",EDGE,"E6.trimOffspring"),sQuery(id+"F0.wireOp",EDGE,"E7.trimOffspring"),sQuery(id+"F0.wireOp",EDGE,"E9.trimOffspring"),sQuery(id+"F0.wireOp",EDGE,"E10.1.0"),sQuery(id+"F0.wireOp",EDGE,"E10.1.1"),sQuery(id+"F0.wireOp",EDGE,"E10.1.2"),sQuery(id+"F0.wireOp",EDGE,"E10.1.3"),sQuery(id+"F0.wireOp",EDGE,"E10.1.5"),sQuery(id+"F0.wireOp",EDGE,"E10.1.7"),sQuery(id+"F0.wireOp",EDGE,"E10.1.8"),sQuery(id+"F0.wireOp",EDGE,"E10.1.9"),sQuery(id+"F0.wireOp",EDGE,"E10.1.10"),sQuery(id+"F0.wireOp",EDGE,"E10.1.11"),sQuery(id+"F0.wireOp",EDGE,"E10.1.12"),sQuery(id+"F0.wireOp",EDGE,"E10.1.14"),sQuery(id+"F0.wireOp",EDGE,"E10.1.15"),sQuery(id+"F0.wireOp",EDGE,"E10.1.16"),sQuery(id+"F0.wireOp",EDGE,"E10.1.18"),sQuery(id+"F0.wireOp",EDGE,"E10.1.20"),sQuery(id+"F0.wireOp",EDGE,"E10.2.0"),sQuery(id+"F0.wireOp",EDGE,"E10.2.1"),sQuery(id+"F0.wireOp",EDGE,"E10.2.2"),sQuery(id+"F0.wireOp",EDGE,"E10.2.3"),sQuery(id+"F0.wireOp",EDGE,"E10.2.5"),sQuery(id+"F0.wireOp",EDGE,"E10.2.7"),sQuery(id+"F0.wireOp",EDGE,"E10.2.8"),sQuery(id+"F0.wireOp",EDGE,"E10.2.9"),sQuery(id+"F0.wireOp",EDGE,"E10.2.10"),sQuery(id+"F0.wireOp",EDGE,"E10.2.11"),sQuery(id+"F0.wireOp",EDGE,"E10.2.12"),sQuery(id+"F0.wireOp",EDGE,"E1"),sQuery(id+"F0.wireOp",EDGE,"E10.2.14"),sQuery(id+"F0.wireOp",EDGE,"E10.2.15"),sQuery(id+"F0.wireOp",EDGE,"E10.2.16"),sQuery(id+"F0.wireOp",EDGE,"E10.2.18"),sQuery(id+"F0.wireOp",EDGE,"E10.2.20"),sQuery(id+"F0.wireOp",EDGE,"E8.trimOffspring"),sQuery(id+"F0.wireOp",EDGE,"E0"),sQuery(id+"F0.wireOp",EDGE,"E10.1.6"),sQuery(id+"F0.wireOp",EDGE,"E11"),sQuery(id+"F0.wireOp",EDGE,"E12"),sQuery(id+"F0.wireOp",EDGE,"E13.1.0"),sQuery(id+"F0.wireOp",EDGE,"E13.1.1"),sQuery(id+"F0.wireOp",EDGE,"E13.2.0"),sQuery(id+"F0.wireOp",EDGE,"E13.2.1")])]}),"instanceName":"1"}),"instanceName":"1"}),"instanceName":"1"});
            var Q1;
            Q1=makeQuery(id+"F23.opPattern","COPY",EDGE,{"derivedFrom":makeQuery(id+"F8.opPattern","COPY",EDGE,{"derivedFrom":makeQuery(id+"F7.opPattern","COPY",EDGE,{"derivedFrom":makeQuery(id+"F1.opExtrude","CAP_EDGE",EDGE,{"disambiguationData":[OSD([sQuery(id+"F0.wireOp",EDGE,"E1")])],"isStart":false}),"instanceName":"1"}),"instanceName":"1"}),"instanceName":"1"});
            transform(context, id + "F34", {"entities" : qUnion([Q0]), "transformType" : TransformType.ROTATION, "transformAxis" : qUnion([Q1]), "angle" : 40 * degree, "oppositeDirection" : true, "makeCopy" : false});
        }
        {
            var Q0;
            Q0=makeQuery(id+"F23.opPattern","COPY",BODY,{"derivedFrom":makeQuery(id+"F8.opPattern","COPY",BODY,{"derivedFrom":makeQuery(id+"F7.opPattern","COPY",BODY,{"derivedFrom":makeQuery(id+"F1.opExtrude","SWEPT_BODY",BODY,{"disambiguationData":[OSD([sQuery(id+"F0.wireOp",EDGE,"E2.0"),sQuery(id+"F0.wireOp",EDGE,"E2.1"),sQuery(id+"F0.wireOp",EDGE,"E2.2"),sQuery(id+"F0.wireOp",EDGE,"E2.3"),sQuery(id+"F0.wireOp",EDGE,"E2.4"),sQuery(id+"F0.wireOp",EDGE,"E2.5"),sQuery(id+"F0.wireOp",EDGE,"E3"),sQuery(id+"F0.wireOp",EDGE,"E4"),sQuery(id+"F0.wireOp",EDGE,"E5.0"),sQuery(id+"F0.wireOp",EDGE,"E5.1"),sQuery(id+"F0.wireOp",EDGE,"E5.3"),sQuery(id+"F0.wireOp",EDGE,"E5.4"),sQuery(id+"F0.wireOp",EDGE,"E5.5"),sQuery(id+"F0.wireOp",EDGE,"E6.trimOffspring"),sQuery(id+"F0.wireOp",EDGE,"E7.trimOffspring"),sQuery(id+"F0.wireOp",EDGE,"E9.trimOffspring"),sQuery(id+"F0.wireOp",EDGE,"E10.1.0"),sQuery(id+"F0.wireOp",EDGE,"E10.1.1"),sQuery(id+"F0.wireOp",EDGE,"E10.1.2"),sQuery(id+"F0.wireOp",EDGE,"E10.1.3"),sQuery(id+"F0.wireOp",EDGE,"E10.1.5"),sQuery(id+"F0.wireOp",EDGE,"E10.1.7"),sQuery(id+"F0.wireOp",EDGE,"E10.1.8"),sQuery(id+"F0.wireOp",EDGE,"E10.1.9"),sQuery(id+"F0.wireOp",EDGE,"E10.1.10"),sQuery(id+"F0.wireOp",EDGE,"E10.1.11"),sQuery(id+"F0.wireOp",EDGE,"E10.1.12"),sQuery(id+"F0.wireOp",EDGE,"E10.1.14"),sQuery(id+"F0.wireOp",EDGE,"E10.1.15"),sQuery(id+"F0.wireOp",EDGE,"E10.1.16"),sQuery(id+"F0.wireOp",EDGE,"E10.1.18"),sQuery(id+"F0.wireOp",EDGE,"E10.1.20"),sQuery(id+"F0.wireOp",EDGE,"E10.2.0"),sQuery(id+"F0.wireOp",EDGE,"E10.2.1"),sQuery(id+"F0.wireOp",EDGE,"E10.2.2"),sQuery(id+"F0.wireOp",EDGE,"E10.2.3"),sQuery(id+"F0.wireOp",EDGE,"E10.2.5"),sQuery(id+"F0.wireOp",EDGE,"E10.2.7"),sQuery(id+"F0.wireOp",EDGE,"E10.2.8"),sQuery(id+"F0.wireOp",EDGE,"E10.2.9"),sQuery(id+"F0.wireOp",EDGE,"E10.2.10"),sQuery(id+"F0.wireOp",EDGE,"E10.2.11"),sQuery(id+"F0.wireOp",EDGE,"E10.2.12"),sQuery(id+"F0.wireOp",EDGE,"E1"),sQuery(id+"F0.wireOp",EDGE,"E10.2.14"),sQuery(id+"F0.wireOp",EDGE,"E10.2.15"),sQuery(id+"F0.wireOp",EDGE,"E10.2.16"),sQuery(id+"F0.wireOp",EDGE,"E10.2.18"),sQuery(id+"F0.wireOp",EDGE,"E10.2.20"),sQuery(id+"F0.wireOp",EDGE,"E8.trimOffspring"),sQuery(id+"F0.wireOp",EDGE,"E0"),sQuery(id+"F0.wireOp",EDGE,"E10.1.6"),sQuery(id+"F0.wireOp",EDGE,"E11"),sQuery(id+"F0.wireOp",EDGE,"E12"),sQuery(id+"F0.wireOp",EDGE,"E13.1.0"),sQuery(id+"F0.wireOp",EDGE,"E13.1.1"),sQuery(id+"F0.wireOp",EDGE,"E13.2.0"),sQuery(id+"F0.wireOp",EDGE,"E13.2.1")])]}),"instanceName":"1"}),"instanceName":"1"}),"instanceName":"1"});
            transform(context, id + "F35", {"entities" : qUnion([Q0]), "transformType" : TransformType.TRANSLATION_3D, "dx" : 7.9 * mm, "dy" : 6.2 * mm, "dz" : 0 * mm, "makeCopy" : false});
        }
        {
            var Q0;
            Q0=makeQuery(id+"F23.opPattern","COPY",BODY,{"derivedFrom":makeQuery(id+"F7.opPattern","COPY",BODY,{"derivedFrom":makeQuery(id+"F1.opExtrude","SWEPT_BODY",BODY,{"disambiguationData":[OSD([sQuery(id+"F0.wireOp",EDGE,"E2.0"),sQuery(id+"F0.wireOp",EDGE,"E2.1"),sQuery(id+"F0.wireOp",EDGE,"E2.2"),sQuery(id+"F0.wireOp",EDGE,"E2.3"),sQuery(id+"F0.wireOp",EDGE,"E2.4"),sQuery(id+"F0.wireOp",EDGE,"E2.5"),sQuery(id+"F0.wireOp",EDGE,"E3"),sQuery(id+"F0.wireOp",EDGE,"E4"),sQuery(id+"F0.wireOp",EDGE,"E5.0"),sQuery(id+"F0.wireOp",EDGE,"E5.1"),sQuery(id+"F0.wireOp",EDGE,"E5.3"),sQuery(id+"F0.wireOp",EDGE,"E5.4"),sQuery(id+"F0.wireOp",EDGE,"E5.5"),sQuery(id+"F0.wireOp",EDGE,"E6.trimOffspring"),sQuery(id+"F0.wireOp",EDGE,"E7.trimOffspring"),sQuery(id+"F0.wireOp",EDGE,"E9.trimOffspring"),sQuery(id+"F0.wireOp",EDGE,"E10.1.0"),sQuery(id+"F0.wireOp",EDGE,"E10.1.1"),sQuery(id+"F0.wireOp",EDGE,"E10.1.2"),sQuery(id+"F0.wireOp",EDGE,"E10.1.3"),sQuery(id+"F0.wireOp",EDGE,"E10.1.5"),sQuery(id+"F0.wireOp",EDGE,"E10.1.7"),sQuery(id+"F0.wireOp",EDGE,"E10.1.8"),sQuery(id+"F0.wireOp",EDGE,"E10.1.9"),sQuery(id+"F0.wireOp",EDGE,"E10.1.10"),sQuery(id+"F0.wireOp",EDGE,"E10.1.11"),sQuery(id+"F0.wireOp",EDGE,"E10.1.12"),sQuery(id+"F0.wireOp",EDGE,"E10.1.14"),sQuery(id+"F0.wireOp",EDGE,"E10.1.15"),sQuery(id+"F0.wireOp",EDGE,"E10.1.16"),sQuery(id+"F0.wireOp",EDGE,"E10.1.18"),sQuery(id+"F0.wireOp",EDGE,"E10.1.20"),sQuery(id+"F0.wireOp",EDGE,"E10.2.0"),sQuery(id+"F0.wireOp",EDGE,"E10.2.1"),sQuery(id+"F0.wireOp",EDGE,"E10.2.2"),sQuery(id+"F0.wireOp",EDGE,"E10.2.3"),sQuery(id+"F0.wireOp",EDGE,"E10.2.5"),sQuery(id+"F0.wireOp",EDGE,"E10.2.7"),sQuery(id+"F0.wireOp",EDGE,"E10.2.8"),sQuery(id+"F0.wireOp",EDGE,"E10.2.9"),sQuery(id+"F0.wireOp",EDGE,"E10.2.10"),sQuery(id+"F0.wireOp",EDGE,"E10.2.11"),sQuery(id+"F0.wireOp",EDGE,"E10.2.12"),sQuery(id+"F0.wireOp",EDGE,"E1"),sQuery(id+"F0.wireOp",EDGE,"E10.2.14"),sQuery(id+"F0.wireOp",EDGE,"E10.2.15"),sQuery(id+"F0.wireOp",EDGE,"E10.2.16"),sQuery(id+"F0.wireOp",EDGE,"E10.2.18"),sQuery(id+"F0.wireOp",EDGE,"E10.2.20"),sQuery(id+"F0.wireOp",EDGE,"E8.trimOffspring"),sQuery(id+"F0.wireOp",EDGE,"E0"),sQuery(id+"F0.wireOp",EDGE,"E10.1.6"),sQuery(id+"F0.wireOp",EDGE,"E11"),sQuery(id+"F0.wireOp",EDGE,"E12"),sQuery(id+"F0.wireOp",EDGE,"E13.1.0"),sQuery(id+"F0.wireOp",EDGE,"E13.1.1"),sQuery(id+"F0.wireOp",EDGE,"E13.2.0"),sQuery(id+"F0.wireOp",EDGE,"E13.2.1")])]}),"instanceName":"1"}),"instanceName":"1"});
            transform(context, id + "F36", {"entities" : qUnion([Q0]), "transformType" : TransformType.TRANSLATION_3D, "dx" : 69.7 * mm, "dy" : 0 * mm, "dz" : 0 * mm, "makeCopy" : true});
        }
        {
            var Q0;
            Q0=makeQuery(id+"F36.opPattern","COPY",BODY,{"derivedFrom":makeQuery(id+"F23.opPattern","COPY",BODY,{"derivedFrom":makeQuery(id+"F7.opPattern","COPY",BODY,{"derivedFrom":makeQuery(id+"F1.opExtrude","SWEPT_BODY",BODY,{"disambiguationData":[OSD([sQuery(id+"F0.wireOp",EDGE,"E2.0"),sQuery(id+"F0.wireOp",EDGE,"E2.1"),sQuery(id+"F0.wireOp",EDGE,"E2.2"),sQuery(id+"F0.wireOp",EDGE,"E2.3"),sQuery(id+"F0.wireOp",EDGE,"E2.4"),sQuery(id+"F0.wireOp",EDGE,"E2.5"),sQuery(id+"F0.wireOp",EDGE,"E3"),sQuery(id+"F0.wireOp",EDGE,"E4"),sQuery(id+"F0.wireOp",EDGE,"E5.0"),sQuery(id+"F0.wireOp",EDGE,"E5.1"),sQuery(id+"F0.wireOp",EDGE,"E5.3"),sQuery(id+"F0.wireOp",EDGE,"E5.4"),sQuery(id+"F0.wireOp",EDGE,"E5.5"),sQuery(id+"F0.wireOp",EDGE,"E6.trimOffspring"),sQuery(id+"F0.wireOp",EDGE,"E7.trimOffspring"),sQuery(id+"F0.wireOp",EDGE,"E9.trimOffspring"),sQuery(id+"F0.wireOp",EDGE,"E10.1.0"),sQuery(id+"F0.wireOp",EDGE,"E10.1.1"),sQuery(id+"F0.wireOp",EDGE,"E10.1.2"),sQuery(id+"F0.wireOp",EDGE,"E10.1.3"),sQuery(id+"F0.wireOp",EDGE,"E10.1.5"),sQuery(id+"F0.wireOp",EDGE,"E10.1.7"),sQuery(id+"F0.wireOp",EDGE,"E10.1.8"),sQuery(id+"F0.wireOp",EDGE,"E10.1.9"),sQuery(id+"F0.wireOp",EDGE,"E10.1.10"),sQuery(id+"F0.wireOp",EDGE,"E10.1.11"),sQuery(id+"F0.wireOp",EDGE,"E10.1.12"),sQuery(id+"F0.wireOp",EDGE,"E10.1.14"),sQuery(id+"F0.wireOp",EDGE,"E10.1.15"),sQuery(id+"F0.wireOp",EDGE,"E10.1.16"),sQuery(id+"F0.wireOp",EDGE,"E10.1.18"),sQuery(id+"F0.wireOp",EDGE,"E10.1.20"),sQuery(id+"F0.wireOp",EDGE,"E10.2.0"),sQuery(id+"F0.wireOp",EDGE,"E10.2.1"),sQuery(id+"F0.wireOp",EDGE,"E10.2.2"),sQuery(id+"F0.wireOp",EDGE,"E10.2.3"),sQuery(id+"F0.wireOp",EDGE,"E10.2.5"),sQuery(id+"F0.wireOp",EDGE,"E10.2.7"),sQuery(id+"F0.wireOp",EDGE,"E10.2.8"),sQuery(id+"F0.wireOp",EDGE,"E10.2.9"),sQuery(id+"F0.wireOp",EDGE,"E10.2.10"),sQuery(id+"F0.wireOp",EDGE,"E10.2.11"),sQuery(id+"F0.wireOp",EDGE,"E10.2.12"),sQuery(id+"F0.wireOp",EDGE,"E1"),sQuery(id+"F0.wireOp",EDGE,"E10.2.14"),sQuery(id+"F0.wireOp",EDGE,"E10.2.15"),sQuery(id+"F0.wireOp",EDGE,"E10.2.16"),sQuery(id+"F0.wireOp",EDGE,"E10.2.18"),sQuery(id+"F0.wireOp",EDGE,"E10.2.20"),sQuery(id+"F0.wireOp",EDGE,"E8.trimOffspring"),sQuery(id+"F0.wireOp",EDGE,"E0"),sQuery(id+"F0.wireOp",EDGE,"E10.1.6"),sQuery(id+"F0.wireOp",EDGE,"E11"),sQuery(id+"F0.wireOp",EDGE,"E12"),sQuery(id+"F0.wireOp",EDGE,"E13.1.0"),sQuery(id+"F0.wireOp",EDGE,"E13.1.1"),sQuery(id+"F0.wireOp",EDGE,"E13.2.0"),sQuery(id+"F0.wireOp",EDGE,"E13.2.1")])]}),"instanceName":"1"}),"instanceName":"1"}),"instanceName":"1"});
            var Q1;
            Q1=makeQuery(id+"F36.opPattern","COPY",EDGE,{"derivedFrom":makeQuery(id+"F23.opPattern","COPY",EDGE,{"derivedFrom":makeQuery(id+"F7.opPattern","COPY",EDGE,{"derivedFrom":makeQuery(id+"F1.opExtrude","CAP_EDGE",EDGE,{"disambiguationData":[OSD([sQuery(id+"F0.wireOp",EDGE,"E1")])],"isStart":false}),"instanceName":"1"}),"instanceName":"1"}),"instanceName":"1"});
            transform(context, id + "F37", {"entities" : qUnion([Q0]), "transformType" : TransformType.ROTATION, "transformAxis" : qUnion([Q1]), "angle" : 5 * degree, "makeCopy" : false});
        }
        {
            var Q0;
            Q0=makeQuery(id+"F36.opPattern","COPY",BODY,{"derivedFrom":makeQuery(id+"F23.opPattern","COPY",BODY,{"derivedFrom":makeQuery(id+"F7.opPattern","COPY",BODY,{"derivedFrom":makeQuery(id+"F1.opExtrude","SWEPT_BODY",BODY,{"disambiguationData":[OSD([sQuery(id+"F0.wireOp",EDGE,"E2.0"),sQuery(id+"F0.wireOp",EDGE,"E2.1"),sQuery(id+"F0.wireOp",EDGE,"E2.2"),sQuery(id+"F0.wireOp",EDGE,"E2.3"),sQuery(id+"F0.wireOp",EDGE,"E2.4"),sQuery(id+"F0.wireOp",EDGE,"E2.5"),sQuery(id+"F0.wireOp",EDGE,"E3"),sQuery(id+"F0.wireOp",EDGE,"E4"),sQuery(id+"F0.wireOp",EDGE,"E5.0"),sQuery(id+"F0.wireOp",EDGE,"E5.1"),sQuery(id+"F0.wireOp",EDGE,"E5.3"),sQuery(id+"F0.wireOp",EDGE,"E5.4"),sQuery(id+"F0.wireOp",EDGE,"E5.5"),sQuery(id+"F0.wireOp",EDGE,"E6.trimOffspring"),sQuery(id+"F0.wireOp",EDGE,"E7.trimOffspring"),sQuery(id+"F0.wireOp",EDGE,"E9.trimOffspring"),sQuery(id+"F0.wireOp",EDGE,"E10.1.0"),sQuery(id+"F0.wireOp",EDGE,"E10.1.1"),sQuery(id+"F0.wireOp",EDGE,"E10.1.2"),sQuery(id+"F0.wireOp",EDGE,"E10.1.3"),sQuery(id+"F0.wireOp",EDGE,"E10.1.5"),sQuery(id+"F0.wireOp",EDGE,"E10.1.7"),sQuery(id+"F0.wireOp",EDGE,"E10.1.8"),sQuery(id+"F0.wireOp",EDGE,"E10.1.9"),sQuery(id+"F0.wireOp",EDGE,"E10.1.10"),sQuery(id+"F0.wireOp",EDGE,"E10.1.11"),sQuery(id+"F0.wireOp",EDGE,"E10.1.12"),sQuery(id+"F0.wireOp",EDGE,"E10.1.14"),sQuery(id+"F0.wireOp",EDGE,"E10.1.15"),sQuery(id+"F0.wireOp",EDGE,"E10.1.16"),sQuery(id+"F0.wireOp",EDGE,"E10.1.18"),sQuery(id+"F0.wireOp",EDGE,"E10.1.20"),sQuery(id+"F0.wireOp",EDGE,"E10.2.0"),sQuery(id+"F0.wireOp",EDGE,"E10.2.1"),sQuery(id+"F0.wireOp",EDGE,"E10.2.2"),sQuery(id+"F0.wireOp",EDGE,"E10.2.3"),sQuery(id+"F0.wireOp",EDGE,"E10.2.5"),sQuery(id+"F0.wireOp",EDGE,"E10.2.7"),sQuery(id+"F0.wireOp",EDGE,"E10.2.8"),sQuery(id+"F0.wireOp",EDGE,"E10.2.9"),sQuery(id+"F0.wireOp",EDGE,"E10.2.10"),sQuery(id+"F0.wireOp",EDGE,"E10.2.11"),sQuery(id+"F0.wireOp",EDGE,"E10.2.12"),sQuery(id+"F0.wireOp",EDGE,"E1"),sQuery(id+"F0.wireOp",EDGE,"E10.2.14"),sQuery(id+"F0.wireOp",EDGE,"E10.2.15"),sQuery(id+"F0.wireOp",EDGE,"E10.2.16"),sQuery(id+"F0.wireOp",EDGE,"E10.2.18"),sQuery(id+"F0.wireOp",EDGE,"E10.2.20"),sQuery(id+"F0.wireOp",EDGE,"E8.trimOffspring"),sQuery(id+"F0.wireOp",EDGE,"E0"),sQuery(id+"F0.wireOp",EDGE,"E10.1.6"),sQuery(id+"F0.wireOp",EDGE,"E11"),sQuery(id+"F0.wireOp",EDGE,"E12"),sQuery(id+"F0.wireOp",EDGE,"E13.1.0"),sQuery(id+"F0.wireOp",EDGE,"E13.1.1"),sQuery(id+"F0.wireOp",EDGE,"E13.2.0"),sQuery(id+"F0.wireOp",EDGE,"E13.2.1")])]}),"instanceName":"1"}),"instanceName":"1"}),"instanceName":"1"});
            transform(context, id + "F38", {"entities" : qUnion([Q0]), "transformType" : TransformType.TRANSLATION_3D, "dx" : 2 * mm, "dy" : 0 * mm, "dz" : 0 * mm, "makeCopy" : false});
        }
        {
            var Q0;
            Q0=makeQuery(id+"F36.opPattern","COPY",BODY,{"derivedFrom":makeQuery(id+"F23.opPattern","COPY",BODY,{"derivedFrom":makeQuery(id+"F7.opPattern","COPY",BODY,{"derivedFrom":makeQuery(id+"F1.opExtrude","SWEPT_BODY",BODY,{"disambiguationData":[OSD([sQuery(id+"F0.wireOp",EDGE,"E2.0"),sQuery(id+"F0.wireOp",EDGE,"E2.1"),sQuery(id+"F0.wireOp",EDGE,"E2.2"),sQuery(id+"F0.wireOp",EDGE,"E2.3"),sQuery(id+"F0.wireOp",EDGE,"E2.4"),sQuery(id+"F0.wireOp",EDGE,"E2.5"),sQuery(id+"F0.wireOp",EDGE,"E3"),sQuery(id+"F0.wireOp",EDGE,"E4"),sQuery(id+"F0.wireOp",EDGE,"E5.0"),sQuery(id+"F0.wireOp",EDGE,"E5.1"),sQuery(id+"F0.wireOp",EDGE,"E5.3"),sQuery(id+"F0.wireOp",EDGE,"E5.4"),sQuery(id+"F0.wireOp",EDGE,"E5.5"),sQuery(id+"F0.wireOp",EDGE,"E6.trimOffspring"),sQuery(id+"F0.wireOp",EDGE,"E7.trimOffspring"),sQuery(id+"F0.wireOp",EDGE,"E9.trimOffspring"),sQuery(id+"F0.wireOp",EDGE,"E10.1.0"),sQuery(id+"F0.wireOp",EDGE,"E10.1.1"),sQuery(id+"F0.wireOp",EDGE,"E10.1.2"),sQuery(id+"F0.wireOp",EDGE,"E10.1.3"),sQuery(id+"F0.wireOp",EDGE,"E10.1.5"),sQuery(id+"F0.wireOp",EDGE,"E10.1.7"),sQuery(id+"F0.wireOp",EDGE,"E10.1.8"),sQuery(id+"F0.wireOp",EDGE,"E10.1.9"),sQuery(id+"F0.wireOp",EDGE,"E10.1.10"),sQuery(id+"F0.wireOp",EDGE,"E10.1.11"),sQuery(id+"F0.wireOp",EDGE,"E10.1.12"),sQuery(id+"F0.wireOp",EDGE,"E10.1.14"),sQuery(id+"F0.wireOp",EDGE,"E10.1.15"),sQuery(id+"F0.wireOp",EDGE,"E10.1.16"),sQuery(id+"F0.wireOp",EDGE,"E10.1.18"),sQuery(id+"F0.wireOp",EDGE,"E10.1.20"),sQuery(id+"F0.wireOp",EDGE,"E10.2.0"),sQuery(id+"F0.wireOp",EDGE,"E10.2.1"),sQuery(id+"F0.wireOp",EDGE,"E10.2.2"),sQuery(id+"F0.wireOp",EDGE,"E10.2.3"),sQuery(id+"F0.wireOp",EDGE,"E10.2.5"),sQuery(id+"F0.wireOp",EDGE,"E10.2.7"),sQuery(id+"F0.wireOp",EDGE,"E10.2.8"),sQuery(id+"F0.wireOp",EDGE,"E10.2.9"),sQuery(id+"F0.wireOp",EDGE,"E10.2.10"),sQuery(id+"F0.wireOp",EDGE,"E10.2.11"),sQuery(id+"F0.wireOp",EDGE,"E10.2.12"),sQuery(id+"F0.wireOp",EDGE,"E1"),sQuery(id+"F0.wireOp",EDGE,"E10.2.14"),sQuery(id+"F0.wireOp",EDGE,"E10.2.15"),sQuery(id+"F0.wireOp",EDGE,"E10.2.16"),sQuery(id+"F0.wireOp",EDGE,"E10.2.18"),sQuery(id+"F0.wireOp",EDGE,"E10.2.20"),sQuery(id+"F0.wireOp",EDGE,"E8.trimOffspring"),sQuery(id+"F0.wireOp",EDGE,"E0"),sQuery(id+"F0.wireOp",EDGE,"E10.1.6"),sQuery(id+"F0.wireOp",EDGE,"E11"),sQuery(id+"F0.wireOp",EDGE,"E12"),sQuery(id+"F0.wireOp",EDGE,"E13.1.0"),sQuery(id+"F0.wireOp",EDGE,"E13.1.1"),sQuery(id+"F0.wireOp",EDGE,"E13.2.0"),sQuery(id+"F0.wireOp",EDGE,"E13.2.1")])]}),"instanceName":"1"}),"instanceName":"1"}),"instanceName":"1"});
            transform(context, id + "F39", {"entities" : qUnion([Q0]), "transformType" : TransformType.TRANSLATION_3D, "dx" : 63.8 * mm, "dy" : -27.7 * mm, "dz" : 0 * mm, "makeCopy" : true});
        }
        {
            var Q0;
            Q0=makeQuery(id+"F39.opPattern","COPY",BODY,{"derivedFrom":makeQuery(id+"F36.opPattern","COPY",BODY,{"derivedFrom":makeQuery(id+"F23.opPattern","COPY",BODY,{"derivedFrom":makeQuery(id+"F7.opPattern","COPY",BODY,{"derivedFrom":makeQuery(id+"F1.opExtrude","SWEPT_BODY",BODY,{"disambiguationData":[OSD([sQuery(id+"F0.wireOp",EDGE,"E2.0"),sQuery(id+"F0.wireOp",EDGE,"E2.1"),sQuery(id+"F0.wireOp",EDGE,"E2.2"),sQuery(id+"F0.wireOp",EDGE,"E2.3"),sQuery(id+"F0.wireOp",EDGE,"E2.4"),sQuery(id+"F0.wireOp",EDGE,"E2.5"),sQuery(id+"F0.wireOp",EDGE,"E3"),sQuery(id+"F0.wireOp",EDGE,"E4"),sQuery(id+"F0.wireOp",EDGE,"E5.0"),sQuery(id+"F0.wireOp",EDGE,"E5.1"),sQuery(id+"F0.wireOp",EDGE,"E5.3"),sQuery(id+"F0.wireOp",EDGE,"E5.4"),sQuery(id+"F0.wireOp",EDGE,"E5.5"),sQuery(id+"F0.wireOp",EDGE,"E6.trimOffspring"),sQuery(id+"F0.wireOp",EDGE,"E7.trimOffspring"),sQuery(id+"F0.wireOp",EDGE,"E9.trimOffspring"),sQuery(id+"F0.wireOp",EDGE,"E10.1.0"),sQuery(id+"F0.wireOp",EDGE,"E10.1.1"),sQuery(id+"F0.wireOp",EDGE,"E10.1.2"),sQuery(id+"F0.wireOp",EDGE,"E10.1.3"),sQuery(id+"F0.wireOp",EDGE,"E10.1.5"),sQuery(id+"F0.wireOp",EDGE,"E10.1.7"),sQuery(id+"F0.wireOp",EDGE,"E10.1.8"),sQuery(id+"F0.wireOp",EDGE,"E10.1.9"),sQuery(id+"F0.wireOp",EDGE,"E10.1.10"),sQuery(id+"F0.wireOp",EDGE,"E10.1.11"),sQuery(id+"F0.wireOp",EDGE,"E10.1.12"),sQuery(id+"F0.wireOp",EDGE,"E10.1.14"),sQuery(id+"F0.wireOp",EDGE,"E10.1.15"),sQuery(id+"F0.wireOp",EDGE,"E10.1.16"),sQuery(id+"F0.wireOp",EDGE,"E10.1.18"),sQuery(id+"F0.wireOp",EDGE,"E10.1.20"),sQuery(id+"F0.wireOp",EDGE,"E10.2.0"),sQuery(id+"F0.wireOp",EDGE,"E10.2.1"),sQuery(id+"F0.wireOp",EDGE,"E10.2.2"),sQuery(id+"F0.wireOp",EDGE,"E10.2.3"),sQuery(id+"F0.wireOp",EDGE,"E10.2.5"),sQuery(id+"F0.wireOp",EDGE,"E10.2.7"),sQuery(id+"F0.wireOp",EDGE,"E10.2.8"),sQuery(id+"F0.wireOp",EDGE,"E10.2.9"),sQuery(id+"F0.wireOp",EDGE,"E10.2.10"),sQuery(id+"F0.wireOp",EDGE,"E10.2.11"),sQuery(id+"F0.wireOp",EDGE,"E10.2.12"),sQuery(id+"F0.wireOp",EDGE,"E1"),sQuery(id+"F0.wireOp",EDGE,"E10.2.14"),sQuery(id+"F0.wireOp",EDGE,"E10.2.15"),sQuery(id+"F0.wireOp",EDGE,"E10.2.16"),sQuery(id+"F0.wireOp",EDGE,"E10.2.18"),sQuery(id+"F0.wireOp",EDGE,"E10.2.20"),sQuery(id+"F0.wireOp",EDGE,"E8.trimOffspring"),sQuery(id+"F0.wireOp",EDGE,"E0"),sQuery(id+"F0.wireOp",EDGE,"E10.1.6"),sQuery(id+"F0.wireOp",EDGE,"E11"),sQuery(id+"F0.wireOp",EDGE,"E12"),sQuery(id+"F0.wireOp",EDGE,"E13.1.0"),sQuery(id+"F0.wireOp",EDGE,"E13.1.1"),sQuery(id+"F0.wireOp",EDGE,"E13.2.0"),sQuery(id+"F0.wireOp",EDGE,"E13.2.1")])]}),"instanceName":"1"}),"instanceName":"1"}),"instanceName":"1"}),"instanceName":"1"});
            var Q1;
            Q1=makeQuery(id+"F39.opPattern","COPY",EDGE,{"derivedFrom":makeQuery(id+"F36.opPattern","COPY",EDGE,{"derivedFrom":makeQuery(id+"F23.opPattern","COPY",EDGE,{"derivedFrom":makeQuery(id+"F7.opPattern","COPY",EDGE,{"derivedFrom":makeQuery(id+"F1.opExtrude","CAP_EDGE",EDGE,{"disambiguationData":[OSD([sQuery(id+"F0.wireOp",EDGE,"E1")])],"isStart":false}),"instanceName":"1"}),"instanceName":"1"}),"instanceName":"1"}),"instanceName":"1"});
            transform(context, id + "F40", {"entities" : qUnion([Q0]), "transformType" : TransformType.ROTATION, "transformAxis" : qUnion([Q1]), "angle" : 10 * degree, "makeCopy" : false});
        }
        {
            var Q0;
            Q0=makeQuery(id+"F39.opPattern","COPY",BODY,{"derivedFrom":makeQuery(id+"F36.opPattern","COPY",BODY,{"derivedFrom":makeQuery(id+"F23.opPattern","COPY",BODY,{"derivedFrom":makeQuery(id+"F7.opPattern","COPY",BODY,{"derivedFrom":makeQuery(id+"F1.opExtrude","SWEPT_BODY",BODY,{"disambiguationData":[OSD([sQuery(id+"F0.wireOp",EDGE,"E2.0"),sQuery(id+"F0.wireOp",EDGE,"E2.1"),sQuery(id+"F0.wireOp",EDGE,"E2.2"),sQuery(id+"F0.wireOp",EDGE,"E2.3"),sQuery(id+"F0.wireOp",EDGE,"E2.4"),sQuery(id+"F0.wireOp",EDGE,"E2.5"),sQuery(id+"F0.wireOp",EDGE,"E3"),sQuery(id+"F0.wireOp",EDGE,"E4"),sQuery(id+"F0.wireOp",EDGE,"E5.0"),sQuery(id+"F0.wireOp",EDGE,"E5.1"),sQuery(id+"F0.wireOp",EDGE,"E5.3"),sQuery(id+"F0.wireOp",EDGE,"E5.4"),sQuery(id+"F0.wireOp",EDGE,"E5.5"),sQuery(id+"F0.wireOp",EDGE,"E6.trimOffspring"),sQuery(id+"F0.wireOp",EDGE,"E7.trimOffspring"),sQuery(id+"F0.wireOp",EDGE,"E9.trimOffspring"),sQuery(id+"F0.wireOp",EDGE,"E10.1.0"),sQuery(id+"F0.wireOp",EDGE,"E10.1.1"),sQuery(id+"F0.wireOp",EDGE,"E10.1.2"),sQuery(id+"F0.wireOp",EDGE,"E10.1.3"),sQuery(id+"F0.wireOp",EDGE,"E10.1.5"),sQuery(id+"F0.wireOp",EDGE,"E10.1.7"),sQuery(id+"F0.wireOp",EDGE,"E10.1.8"),sQuery(id+"F0.wireOp",EDGE,"E10.1.9"),sQuery(id+"F0.wireOp",EDGE,"E10.1.10"),sQuery(id+"F0.wireOp",EDGE,"E10.1.11"),sQuery(id+"F0.wireOp",EDGE,"E10.1.12"),sQuery(id+"F0.wireOp",EDGE,"E10.1.14"),sQuery(id+"F0.wireOp",EDGE,"E10.1.15"),sQuery(id+"F0.wireOp",EDGE,"E10.1.16"),sQuery(id+"F0.wireOp",EDGE,"E10.1.18"),sQuery(id+"F0.wireOp",EDGE,"E10.1.20"),sQuery(id+"F0.wireOp",EDGE,"E10.2.0"),sQuery(id+"F0.wireOp",EDGE,"E10.2.1"),sQuery(id+"F0.wireOp",EDGE,"E10.2.2"),sQuery(id+"F0.wireOp",EDGE,"E10.2.3"),sQuery(id+"F0.wireOp",EDGE,"E10.2.5"),sQuery(id+"F0.wireOp",EDGE,"E10.2.7"),sQuery(id+"F0.wireOp",EDGE,"E10.2.8"),sQuery(id+"F0.wireOp",EDGE,"E10.2.9"),sQuery(id+"F0.wireOp",EDGE,"E10.2.10"),sQuery(id+"F0.wireOp",EDGE,"E10.2.11"),sQuery(id+"F0.wireOp",EDGE,"E10.2.12"),sQuery(id+"F0.wireOp",EDGE,"E1"),sQuery(id+"F0.wireOp",EDGE,"E10.2.14"),sQuery(id+"F0.wireOp",EDGE,"E10.2.15"),sQuery(id+"F0.wireOp",EDGE,"E10.2.16"),sQuery(id+"F0.wireOp",EDGE,"E10.2.18"),sQuery(id+"F0.wireOp",EDGE,"E10.2.20"),sQuery(id+"F0.wireOp",EDGE,"E8.trimOffspring"),sQuery(id+"F0.wireOp",EDGE,"E0"),sQuery(id+"F0.wireOp",EDGE,"E10.1.6"),sQuery(id+"F0.wireOp",EDGE,"E11"),sQuery(id+"F0.wireOp",EDGE,"E12"),sQuery(id+"F0.wireOp",EDGE,"E13.1.0"),sQuery(id+"F0.wireOp",EDGE,"E13.1.1"),sQuery(id+"F0.wireOp",EDGE,"E13.2.0"),sQuery(id+"F0.wireOp",EDGE,"E13.2.1")])]}),"instanceName":"1"}),"instanceName":"1"}),"instanceName":"1"}),"instanceName":"1"});
            transform(context, id + "F41", {"entities" : qUnion([Q0]), "transformType" : TransformType.TRANSLATION_3D, "dx" : 0 * mm, "dy" : 1.1 * mm, "dz" : 0 * mm, "makeCopy" : false});
        }
        {
            var Q0;
            Q0=makeQuery(id+"F13.opPattern","COPY",BODY,{"derivedFrom":makeQuery(id+"F1.opExtrude","SWEPT_BODY",BODY,{"disambiguationData":[OSD([sQuery(id+"F0.wireOp",EDGE,"E2.0"),sQuery(id+"F0.wireOp",EDGE,"E2.1"),sQuery(id+"F0.wireOp",EDGE,"E2.2"),sQuery(id+"F0.wireOp",EDGE,"E2.3"),sQuery(id+"F0.wireOp",EDGE,"E2.4"),sQuery(id+"F0.wireOp",EDGE,"E2.5"),sQuery(id+"F0.wireOp",EDGE,"E3"),sQuery(id+"F0.wireOp",EDGE,"E4"),sQuery(id+"F0.wireOp",EDGE,"E5.0"),sQuery(id+"F0.wireOp",EDGE,"E5.1"),sQuery(id+"F0.wireOp",EDGE,"E5.3"),sQuery(id+"F0.wireOp",EDGE,"E5.4"),sQuery(id+"F0.wireOp",EDGE,"E5.5"),sQuery(id+"F0.wireOp",EDGE,"E6.trimOffspring"),sQuery(id+"F0.wireOp",EDGE,"E7.trimOffspring"),sQuery(id+"F0.wireOp",EDGE,"E9.trimOffspring"),sQuery(id+"F0.wireOp",EDGE,"E10.1.0"),sQuery(id+"F0.wireOp",EDGE,"E10.1.1"),sQuery(id+"F0.wireOp",EDGE,"E10.1.2"),sQuery(id+"F0.wireOp",EDGE,"E10.1.3"),sQuery(id+"F0.wireOp",EDGE,"E10.1.5"),sQuery(id+"F0.wireOp",EDGE,"E10.1.7"),sQuery(id+"F0.wireOp",EDGE,"E10.1.8"),sQuery(id+"F0.wireOp",EDGE,"E10.1.9"),sQuery(id+"F0.wireOp",EDGE,"E10.1.10"),sQuery(id+"F0.wireOp",EDGE,"E10.1.11"),sQuery(id+"F0.wireOp",EDGE,"E10.1.12"),sQuery(id+"F0.wireOp",EDGE,"E10.1.14"),sQuery(id+"F0.wireOp",EDGE,"E10.1.15"),sQuery(id+"F0.wireOp",EDGE,"E10.1.16"),sQuery(id+"F0.wireOp",EDGE,"E10.1.18"),sQuery(id+"F0.wireOp",EDGE,"E10.1.20"),sQuery(id+"F0.wireOp",EDGE,"E10.2.0"),sQuery(id+"F0.wireOp",EDGE,"E10.2.1"),sQuery(id+"F0.wireOp",EDGE,"E10.2.2"),sQuery(id+"F0.wireOp",EDGE,"E10.2.3"),sQuery(id+"F0.wireOp",EDGE,"E10.2.5"),sQuery(id+"F0.wireOp",EDGE,"E10.2.7"),sQuery(id+"F0.wireOp",EDGE,"E10.2.8"),sQuery(id+"F0.wireOp",EDGE,"E10.2.9"),sQuery(id+"F0.wireOp",EDGE,"E10.2.10"),sQuery(id+"F0.wireOp",EDGE,"E10.2.11"),sQuery(id+"F0.wireOp",EDGE,"E10.2.12"),sQuery(id+"F0.wireOp",EDGE,"E1"),sQuery(id+"F0.wireOp",EDGE,"E10.2.14"),sQuery(id+"F0.wireOp",EDGE,"E10.2.15"),sQuery(id+"F0.wireOp",EDGE,"E10.2.16"),sQuery(id+"F0.wireOp",EDGE,"E10.2.18"),sQuery(id+"F0.wireOp",EDGE,"E10.2.20"),sQuery(id+"F0.wireOp",EDGE,"E8.trimOffspring"),sQuery(id+"F0.wireOp",EDGE,"E0"),sQuery(id+"F0.wireOp",EDGE,"E10.1.6"),sQuery(id+"F0.wireOp",EDGE,"E11"),sQuery(id+"F0.wireOp",EDGE,"E12"),sQuery(id+"F0.wireOp",EDGE,"E13.1.0"),sQuery(id+"F0.wireOp",EDGE,"E13.1.1"),sQuery(id+"F0.wireOp",EDGE,"E13.2.0"),sQuery(id+"F0.wireOp",EDGE,"E13.2.1")])]}),"instanceName":"1"});
            transform(context, id + "F42", {"entities" : qUnion([Q0]), "transformType" : TransformType.TRANSLATION_3D, "dx" : 0 * mm, "dy" : -114 * mm, "dz" : 0 * mm, "makeCopy" : true});
        }
        {
            var Q0;
            Q0=makeQuery(id+"F42.opPattern","COPY",BODY,{"derivedFrom":makeQuery(id+"F13.opPattern","COPY",BODY,{"derivedFrom":makeQuery(id+"F1.opExtrude","SWEPT_BODY",BODY,{"disambiguationData":[OSD([sQuery(id+"F0.wireOp",EDGE,"E2.0"),sQuery(id+"F0.wireOp",EDGE,"E2.1"),sQuery(id+"F0.wireOp",EDGE,"E2.2"),sQuery(id+"F0.wireOp",EDGE,"E2.3"),sQuery(id+"F0.wireOp",EDGE,"E2.4"),sQuery(id+"F0.wireOp",EDGE,"E2.5"),sQuery(id+"F0.wireOp",EDGE,"E3"),sQuery(id+"F0.wireOp",EDGE,"E4"),sQuery(id+"F0.wireOp",EDGE,"E5.0"),sQuery(id+"F0.wireOp",EDGE,"E5.1"),sQuery(id+"F0.wireOp",EDGE,"E5.3"),sQuery(id+"F0.wireOp",EDGE,"E5.4"),sQuery(id+"F0.wireOp",EDGE,"E5.5"),sQuery(id+"F0.wireOp",EDGE,"E6.trimOffspring"),sQuery(id+"F0.wireOp",EDGE,"E7.trimOffspring"),sQuery(id+"F0.wireOp",EDGE,"E9.trimOffspring"),sQuery(id+"F0.wireOp",EDGE,"E10.1.0"),sQuery(id+"F0.wireOp",EDGE,"E10.1.1"),sQuery(id+"F0.wireOp",EDGE,"E10.1.2"),sQuery(id+"F0.wireOp",EDGE,"E10.1.3"),sQuery(id+"F0.wireOp",EDGE,"E10.1.5"),sQuery(id+"F0.wireOp",EDGE,"E10.1.7"),sQuery(id+"F0.wireOp",EDGE,"E10.1.8"),sQuery(id+"F0.wireOp",EDGE,"E10.1.9"),sQuery(id+"F0.wireOp",EDGE,"E10.1.10"),sQuery(id+"F0.wireOp",EDGE,"E10.1.11"),sQuery(id+"F0.wireOp",EDGE,"E10.1.12"),sQuery(id+"F0.wireOp",EDGE,"E10.1.14"),sQuery(id+"F0.wireOp",EDGE,"E10.1.15"),sQuery(id+"F0.wireOp",EDGE,"E10.1.16"),sQuery(id+"F0.wireOp",EDGE,"E10.1.18"),sQuery(id+"F0.wireOp",EDGE,"E10.1.20"),sQuery(id+"F0.wireOp",EDGE,"E10.2.0"),sQuery(id+"F0.wireOp",EDGE,"E10.2.1"),sQuery(id+"F0.wireOp",EDGE,"E10.2.2"),sQuery(id+"F0.wireOp",EDGE,"E10.2.3"),sQuery(id+"F0.wireOp",EDGE,"E10.2.5"),sQuery(id+"F0.wireOp",EDGE,"E10.2.7"),sQuery(id+"F0.wireOp",EDGE,"E10.2.8"),sQuery(id+"F0.wireOp",EDGE,"E10.2.9"),sQuery(id+"F0.wireOp",EDGE,"E10.2.10"),sQuery(id+"F0.wireOp",EDGE,"E10.2.11"),sQuery(id+"F0.wireOp",EDGE,"E10.2.12"),sQuery(id+"F0.wireOp",EDGE,"E1"),sQuery(id+"F0.wireOp",EDGE,"E10.2.14"),sQuery(id+"F0.wireOp",EDGE,"E10.2.15"),sQuery(id+"F0.wireOp",EDGE,"E10.2.16"),sQuery(id+"F0.wireOp",EDGE,"E10.2.18"),sQuery(id+"F0.wireOp",EDGE,"E10.2.20"),sQuery(id+"F0.wireOp",EDGE,"E8.trimOffspring"),sQuery(id+"F0.wireOp",EDGE,"E0"),sQuery(id+"F0.wireOp",EDGE,"E10.1.6"),sQuery(id+"F0.wireOp",EDGE,"E11"),sQuery(id+"F0.wireOp",EDGE,"E12"),sQuery(id+"F0.wireOp",EDGE,"E13.1.0"),sQuery(id+"F0.wireOp",EDGE,"E13.1.1"),sQuery(id+"F0.wireOp",EDGE,"E13.2.0"),sQuery(id+"F0.wireOp",EDGE,"E13.2.1")])]}),"instanceName":"1"}),"instanceName":"1"});
            var Q1;
            Q1=makeQuery(id+"F42.opPattern","COPY",EDGE,{"derivedFrom":makeQuery(id+"F13.opPattern","COPY",EDGE,{"derivedFrom":makeQuery(id+"F1.opExtrude","CAP_EDGE",EDGE,{"disambiguationData":[OSD([sQuery(id+"F0.wireOp",EDGE,"E1")])],"isStart":false}),"instanceName":"1"}),"instanceName":"1"});
            transform(context, id + "F43", {"entities" : qUnion([Q0]), "transformType" : TransformType.ROTATION, "transformAxis" : qUnion([Q1]), "angle" : 30 * degree, "makeCopy" : false});
        }
        {
            var Q0;
            Q0=makeQuery(id+"F42.opPattern","COPY",BODY,{"derivedFrom":makeQuery(id+"F13.opPattern","COPY",BODY,{"derivedFrom":makeQuery(id+"F1.opExtrude","SWEPT_BODY",BODY,{"disambiguationData":[OSD([sQuery(id+"F0.wireOp",EDGE,"E2.0"),sQuery(id+"F0.wireOp",EDGE,"E2.1"),sQuery(id+"F0.wireOp",EDGE,"E2.2"),sQuery(id+"F0.wireOp",EDGE,"E2.3"),sQuery(id+"F0.wireOp",EDGE,"E2.4"),sQuery(id+"F0.wireOp",EDGE,"E2.5"),sQuery(id+"F0.wireOp",EDGE,"E3"),sQuery(id+"F0.wireOp",EDGE,"E4"),sQuery(id+"F0.wireOp",EDGE,"E5.0"),sQuery(id+"F0.wireOp",EDGE,"E5.1"),sQuery(id+"F0.wireOp",EDGE,"E5.3"),sQuery(id+"F0.wireOp",EDGE,"E5.4"),sQuery(id+"F0.wireOp",EDGE,"E5.5"),sQuery(id+"F0.wireOp",EDGE,"E6.trimOffspring"),sQuery(id+"F0.wireOp",EDGE,"E7.trimOffspring"),sQuery(id+"F0.wireOp",EDGE,"E9.trimOffspring"),sQuery(id+"F0.wireOp",EDGE,"E10.1.0"),sQuery(id+"F0.wireOp",EDGE,"E10.1.1"),sQuery(id+"F0.wireOp",EDGE,"E10.1.2"),sQuery(id+"F0.wireOp",EDGE,"E10.1.3"),sQuery(id+"F0.wireOp",EDGE,"E10.1.5"),sQuery(id+"F0.wireOp",EDGE,"E10.1.7"),sQuery(id+"F0.wireOp",EDGE,"E10.1.8"),sQuery(id+"F0.wireOp",EDGE,"E10.1.9"),sQuery(id+"F0.wireOp",EDGE,"E10.1.10"),sQuery(id+"F0.wireOp",EDGE,"E10.1.11"),sQuery(id+"F0.wireOp",EDGE,"E10.1.12"),sQuery(id+"F0.wireOp",EDGE,"E10.1.14"),sQuery(id+"F0.wireOp",EDGE,"E10.1.15"),sQuery(id+"F0.wireOp",EDGE,"E10.1.16"),sQuery(id+"F0.wireOp",EDGE,"E10.1.18"),sQuery(id+"F0.wireOp",EDGE,"E10.1.20"),sQuery(id+"F0.wireOp",EDGE,"E10.2.0"),sQuery(id+"F0.wireOp",EDGE,"E10.2.1"),sQuery(id+"F0.wireOp",EDGE,"E10.2.2"),sQuery(id+"F0.wireOp",EDGE,"E10.2.3"),sQuery(id+"F0.wireOp",EDGE,"E10.2.5"),sQuery(id+"F0.wireOp",EDGE,"E10.2.7"),sQuery(id+"F0.wireOp",EDGE,"E10.2.8"),sQuery(id+"F0.wireOp",EDGE,"E10.2.9"),sQuery(id+"F0.wireOp",EDGE,"E10.2.10"),sQuery(id+"F0.wireOp",EDGE,"E10.2.11"),sQuery(id+"F0.wireOp",EDGE,"E10.2.12"),sQuery(id+"F0.wireOp",EDGE,"E1"),sQuery(id+"F0.wireOp",EDGE,"E10.2.14"),sQuery(id+"F0.wireOp",EDGE,"E10.2.15"),sQuery(id+"F0.wireOp",EDGE,"E10.2.16"),sQuery(id+"F0.wireOp",EDGE,"E10.2.18"),sQuery(id+"F0.wireOp",EDGE,"E10.2.20"),sQuery(id+"F0.wireOp",EDGE,"E8.trimOffspring"),sQuery(id+"F0.wireOp",EDGE,"E0"),sQuery(id+"F0.wireOp",EDGE,"E10.1.6"),sQuery(id+"F0.wireOp",EDGE,"E11"),sQuery(id+"F0.wireOp",EDGE,"E12"),sQuery(id+"F0.wireOp",EDGE,"E13.1.0"),sQuery(id+"F0.wireOp",EDGE,"E13.1.1"),sQuery(id+"F0.wireOp",EDGE,"E13.2.0"),sQuery(id+"F0.wireOp",EDGE,"E13.2.1")])]}),"instanceName":"1"}),"instanceName":"1"});
            transform(context, id + "F44", {"entities" : qUnion([Q0]), "transformType" : TransformType.TRANSLATION_3D, "dx" : 3.5 * mm, "dy" : -1 * mm, "dz" : 0 * mm, "makeCopy" : false});
        }
        {
            var Q0;
            Q0=makeQuery(id+"F5.opPattern","COPY",BODY,{"derivedFrom":makeQuery(id+"F1.opExtrude","SWEPT_BODY",BODY,{"disambiguationData":[OSD([sQuery(id+"F0.wireOp",EDGE,"E2.0"),sQuery(id+"F0.wireOp",EDGE,"E2.1"),sQuery(id+"F0.wireOp",EDGE,"E2.2"),sQuery(id+"F0.wireOp",EDGE,"E2.3"),sQuery(id+"F0.wireOp",EDGE,"E2.4"),sQuery(id+"F0.wireOp",EDGE,"E2.5"),sQuery(id+"F0.wireOp",EDGE,"E3"),sQuery(id+"F0.wireOp",EDGE,"E4"),sQuery(id+"F0.wireOp",EDGE,"E5.0"),sQuery(id+"F0.wireOp",EDGE,"E5.1"),sQuery(id+"F0.wireOp",EDGE,"E5.3"),sQuery(id+"F0.wireOp",EDGE,"E5.4"),sQuery(id+"F0.wireOp",EDGE,"E5.5"),sQuery(id+"F0.wireOp",EDGE,"E6.trimOffspring"),sQuery(id+"F0.wireOp",EDGE,"E7.trimOffspring"),sQuery(id+"F0.wireOp",EDGE,"E9.trimOffspring"),sQuery(id+"F0.wireOp",EDGE,"E10.1.0"),sQuery(id+"F0.wireOp",EDGE,"E10.1.1"),sQuery(id+"F0.wireOp",EDGE,"E10.1.2"),sQuery(id+"F0.wireOp",EDGE,"E10.1.3"),sQuery(id+"F0.wireOp",EDGE,"E10.1.5"),sQuery(id+"F0.wireOp",EDGE,"E10.1.7"),sQuery(id+"F0.wireOp",EDGE,"E10.1.8"),sQuery(id+"F0.wireOp",EDGE,"E10.1.9"),sQuery(id+"F0.wireOp",EDGE,"E10.1.10"),sQuery(id+"F0.wireOp",EDGE,"E10.1.11"),sQuery(id+"F0.wireOp",EDGE,"E10.1.12"),sQuery(id+"F0.wireOp",EDGE,"E10.1.14"),sQuery(id+"F0.wireOp",EDGE,"E10.1.15"),sQuery(id+"F0.wireOp",EDGE,"E10.1.16"),sQuery(id+"F0.wireOp",EDGE,"E10.1.18"),sQuery(id+"F0.wireOp",EDGE,"E10.1.20"),sQuery(id+"F0.wireOp",EDGE,"E10.2.0"),sQuery(id+"F0.wireOp",EDGE,"E10.2.1"),sQuery(id+"F0.wireOp",EDGE,"E10.2.2"),sQuery(id+"F0.wireOp",EDGE,"E10.2.3"),sQuery(id+"F0.wireOp",EDGE,"E10.2.5"),sQuery(id+"F0.wireOp",EDGE,"E10.2.7"),sQuery(id+"F0.wireOp",EDGE,"E10.2.8"),sQuery(id+"F0.wireOp",EDGE,"E10.2.9"),sQuery(id+"F0.wireOp",EDGE,"E10.2.10"),sQuery(id+"F0.wireOp",EDGE,"E10.2.11"),sQuery(id+"F0.wireOp",EDGE,"E10.2.12"),sQuery(id+"F0.wireOp",EDGE,"E1"),sQuery(id+"F0.wireOp",EDGE,"E10.2.14"),sQuery(id+"F0.wireOp",EDGE,"E10.2.15"),sQuery(id+"F0.wireOp",EDGE,"E10.2.16"),sQuery(id+"F0.wireOp",EDGE,"E10.2.18"),sQuery(id+"F0.wireOp",EDGE,"E10.2.20"),sQuery(id+"F0.wireOp",EDGE,"E8.trimOffspring"),sQuery(id+"F0.wireOp",EDGE,"E0"),sQuery(id+"F0.wireOp",EDGE,"E10.1.6"),sQuery(id+"F0.wireOp",EDGE,"E11"),sQuery(id+"F0.wireOp",EDGE,"E12"),sQuery(id+"F0.wireOp",EDGE,"E13.1.0"),sQuery(id+"F0.wireOp",EDGE,"E13.1.1"),sQuery(id+"F0.wireOp",EDGE,"E13.2.0"),sQuery(id+"F0.wireOp",EDGE,"E13.2.1")])]}),"instanceName":"1"});
            transform(context, id + "F45", {"entities" : qUnion([Q0]), "transformType" : TransformType.TRANSLATION_3D, "dx" : 32 * mm, "dy" : -173.8 * mm, "dz" : 0 * mm, "makeCopy" : true});
        }
        {
            var Q0;
            Q0=makeQuery(id+"F45.opPattern","COPY",BODY,{"derivedFrom":makeQuery(id+"F5.opPattern","COPY",BODY,{"derivedFrom":makeQuery(id+"F1.opExtrude","SWEPT_BODY",BODY,{"disambiguationData":[OSD([sQuery(id+"F0.wireOp",EDGE,"E2.0"),sQuery(id+"F0.wireOp",EDGE,"E2.1"),sQuery(id+"F0.wireOp",EDGE,"E2.2"),sQuery(id+"F0.wireOp",EDGE,"E2.3"),sQuery(id+"F0.wireOp",EDGE,"E2.4"),sQuery(id+"F0.wireOp",EDGE,"E2.5"),sQuery(id+"F0.wireOp",EDGE,"E3"),sQuery(id+"F0.wireOp",EDGE,"E4"),sQuery(id+"F0.wireOp",EDGE,"E5.0"),sQuery(id+"F0.wireOp",EDGE,"E5.1"),sQuery(id+"F0.wireOp",EDGE,"E5.3"),sQuery(id+"F0.wireOp",EDGE,"E5.4"),sQuery(id+"F0.wireOp",EDGE,"E5.5"),sQuery(id+"F0.wireOp",EDGE,"E6.trimOffspring"),sQuery(id+"F0.wireOp",EDGE,"E7.trimOffspring"),sQuery(id+"F0.wireOp",EDGE,"E9.trimOffspring"),sQuery(id+"F0.wireOp",EDGE,"E10.1.0"),sQuery(id+"F0.wireOp",EDGE,"E10.1.1"),sQuery(id+"F0.wireOp",EDGE,"E10.1.2"),sQuery(id+"F0.wireOp",EDGE,"E10.1.3"),sQuery(id+"F0.wireOp",EDGE,"E10.1.5"),sQuery(id+"F0.wireOp",EDGE,"E10.1.7"),sQuery(id+"F0.wireOp",EDGE,"E10.1.8"),sQuery(id+"F0.wireOp",EDGE,"E10.1.9"),sQuery(id+"F0.wireOp",EDGE,"E10.1.10"),sQuery(id+"F0.wireOp",EDGE,"E10.1.11"),sQuery(id+"F0.wireOp",EDGE,"E10.1.12"),sQuery(id+"F0.wireOp",EDGE,"E10.1.14"),sQuery(id+"F0.wireOp",EDGE,"E10.1.15"),sQuery(id+"F0.wireOp",EDGE,"E10.1.16"),sQuery(id+"F0.wireOp",EDGE,"E10.1.18"),sQuery(id+"F0.wireOp",EDGE,"E10.1.20"),sQuery(id+"F0.wireOp",EDGE,"E10.2.0"),sQuery(id+"F0.wireOp",EDGE,"E10.2.1"),sQuery(id+"F0.wireOp",EDGE,"E10.2.2"),sQuery(id+"F0.wireOp",EDGE,"E10.2.3"),sQuery(id+"F0.wireOp",EDGE,"E10.2.5"),sQuery(id+"F0.wireOp",EDGE,"E10.2.7"),sQuery(id+"F0.wireOp",EDGE,"E10.2.8"),sQuery(id+"F0.wireOp",EDGE,"E10.2.9"),sQuery(id+"F0.wireOp",EDGE,"E10.2.10"),sQuery(id+"F0.wireOp",EDGE,"E10.2.11"),sQuery(id+"F0.wireOp",EDGE,"E10.2.12"),sQuery(id+"F0.wireOp",EDGE,"E1"),sQuery(id+"F0.wireOp",EDGE,"E10.2.14"),sQuery(id+"F0.wireOp",EDGE,"E10.2.15"),sQuery(id+"F0.wireOp",EDGE,"E10.2.16"),sQuery(id+"F0.wireOp",EDGE,"E10.2.18"),sQuery(id+"F0.wireOp",EDGE,"E10.2.20"),sQuery(id+"F0.wireOp",EDGE,"E8.trimOffspring"),sQuery(id+"F0.wireOp",EDGE,"E0"),sQuery(id+"F0.wireOp",EDGE,"E10.1.6"),sQuery(id+"F0.wireOp",EDGE,"E11"),sQuery(id+"F0.wireOp",EDGE,"E12"),sQuery(id+"F0.wireOp",EDGE,"E13.1.0"),sQuery(id+"F0.wireOp",EDGE,"E13.1.1"),sQuery(id+"F0.wireOp",EDGE,"E13.2.0"),sQuery(id+"F0.wireOp",EDGE,"E13.2.1")])]}),"instanceName":"1"}),"instanceName":"1"});
            transform(context, id + "F46", {"entities" : qUnion([Q0]), "transformType" : TransformType.TRANSLATION_3D, "dx" : 68.8 * mm, "dy" : 0 * mm, "dz" : 0 * mm, "makeCopy" : true});
        }
        {
            var Q0;
            Q0=makeQuery(id+"F42.opPattern","COPY",BODY,{"derivedFrom":makeQuery(id+"F13.opPattern","COPY",BODY,{"derivedFrom":makeQuery(id+"F1.opExtrude","SWEPT_BODY",BODY,{"disambiguationData":[OSD([sQuery(id+"F0.wireOp",EDGE,"E2.0"),sQuery(id+"F0.wireOp",EDGE,"E2.1"),sQuery(id+"F0.wireOp",EDGE,"E2.2"),sQuery(id+"F0.wireOp",EDGE,"E2.3"),sQuery(id+"F0.wireOp",EDGE,"E2.4"),sQuery(id+"F0.wireOp",EDGE,"E2.5"),sQuery(id+"F0.wireOp",EDGE,"E3"),sQuery(id+"F0.wireOp",EDGE,"E4"),sQuery(id+"F0.wireOp",EDGE,"E5.0"),sQuery(id+"F0.wireOp",EDGE,"E5.1"),sQuery(id+"F0.wireOp",EDGE,"E5.3"),sQuery(id+"F0.wireOp",EDGE,"E5.4"),sQuery(id+"F0.wireOp",EDGE,"E5.5"),sQuery(id+"F0.wireOp",EDGE,"E6.trimOffspring"),sQuery(id+"F0.wireOp",EDGE,"E7.trimOffspring"),sQuery(id+"F0.wireOp",EDGE,"E9.trimOffspring"),sQuery(id+"F0.wireOp",EDGE,"E10.1.0"),sQuery(id+"F0.wireOp",EDGE,"E10.1.1"),sQuery(id+"F0.wireOp",EDGE,"E10.1.2"),sQuery(id+"F0.wireOp",EDGE,"E10.1.3"),sQuery(id+"F0.wireOp",EDGE,"E10.1.5"),sQuery(id+"F0.wireOp",EDGE,"E10.1.7"),sQuery(id+"F0.wireOp",EDGE,"E10.1.8"),sQuery(id+"F0.wireOp",EDGE,"E10.1.9"),sQuery(id+"F0.wireOp",EDGE,"E10.1.10"),sQuery(id+"F0.wireOp",EDGE,"E10.1.11"),sQuery(id+"F0.wireOp",EDGE,"E10.1.12"),sQuery(id+"F0.wireOp",EDGE,"E10.1.14"),sQuery(id+"F0.wireOp",EDGE,"E10.1.15"),sQuery(id+"F0.wireOp",EDGE,"E10.1.16"),sQuery(id+"F0.wireOp",EDGE,"E10.1.18"),sQuery(id+"F0.wireOp",EDGE,"E10.1.20"),sQuery(id+"F0.wireOp",EDGE,"E10.2.0"),sQuery(id+"F0.wireOp",EDGE,"E10.2.1"),sQuery(id+"F0.wireOp",EDGE,"E10.2.2"),sQuery(id+"F0.wireOp",EDGE,"E10.2.3"),sQuery(id+"F0.wireOp",EDGE,"E10.2.5"),sQuery(id+"F0.wireOp",EDGE,"E10.2.7"),sQuery(id+"F0.wireOp",EDGE,"E10.2.8"),sQuery(id+"F0.wireOp",EDGE,"E10.2.9"),sQuery(id+"F0.wireOp",EDGE,"E10.2.10"),sQuery(id+"F0.wireOp",EDGE,"E10.2.11"),sQuery(id+"F0.wireOp",EDGE,"E10.2.12"),sQuery(id+"F0.wireOp",EDGE,"E1"),sQuery(id+"F0.wireOp",EDGE,"E10.2.14"),sQuery(id+"F0.wireOp",EDGE,"E10.2.15"),sQuery(id+"F0.wireOp",EDGE,"E10.2.16"),sQuery(id+"F0.wireOp",EDGE,"E10.2.18"),sQuery(id+"F0.wireOp",EDGE,"E10.2.20"),sQuery(id+"F0.wireOp",EDGE,"E8.trimOffspring"),sQuery(id+"F0.wireOp",EDGE,"E0"),sQuery(id+"F0.wireOp",EDGE,"E10.1.6"),sQuery(id+"F0.wireOp",EDGE,"E11"),sQuery(id+"F0.wireOp",EDGE,"E12"),sQuery(id+"F0.wireOp",EDGE,"E13.1.0"),sQuery(id+"F0.wireOp",EDGE,"E13.1.1"),sQuery(id+"F0.wireOp",EDGE,"E13.2.0"),sQuery(id+"F0.wireOp",EDGE,"E13.2.1")])]}),"instanceName":"1"}),"instanceName":"1"});
            transform(context, id + "F47", {"entities" : qUnion([Q0]), "transformType" : TransformType.TRANSLATION_3D, "dx" : 199 * mm, "dy" : -23.5 * mm, "dz" : 0 * mm, "makeCopy" : true});
        }
        {
            var Q0;
            Q0=makeQuery(id+"F39.opPattern","COPY",BODY,{"derivedFrom":makeQuery(id+"F36.opPattern","COPY",BODY,{"derivedFrom":makeQuery(id+"F23.opPattern","COPY",BODY,{"derivedFrom":makeQuery(id+"F7.opPattern","COPY",BODY,{"derivedFrom":makeQuery(id+"F1.opExtrude","SWEPT_BODY",BODY,{"disambiguationData":[OSD([sQuery(id+"F0.wireOp",EDGE,"E2.0"),sQuery(id+"F0.wireOp",EDGE,"E2.1"),sQuery(id+"F0.wireOp",EDGE,"E2.2"),sQuery(id+"F0.wireOp",EDGE,"E2.3"),sQuery(id+"F0.wireOp",EDGE,"E2.4"),sQuery(id+"F0.wireOp",EDGE,"E2.5"),sQuery(id+"F0.wireOp",EDGE,"E3"),sQuery(id+"F0.wireOp",EDGE,"E4"),sQuery(id+"F0.wireOp",EDGE,"E5.0"),sQuery(id+"F0.wireOp",EDGE,"E5.1"),sQuery(id+"F0.wireOp",EDGE,"E5.3"),sQuery(id+"F0.wireOp",EDGE,"E5.4"),sQuery(id+"F0.wireOp",EDGE,"E5.5"),sQuery(id+"F0.wireOp",EDGE,"E6.trimOffspring"),sQuery(id+"F0.wireOp",EDGE,"E7.trimOffspring"),sQuery(id+"F0.wireOp",EDGE,"E9.trimOffspring"),sQuery(id+"F0.wireOp",EDGE,"E10.1.0"),sQuery(id+"F0.wireOp",EDGE,"E10.1.1"),sQuery(id+"F0.wireOp",EDGE,"E10.1.2"),sQuery(id+"F0.wireOp",EDGE,"E10.1.3"),sQuery(id+"F0.wireOp",EDGE,"E10.1.5"),sQuery(id+"F0.wireOp",EDGE,"E10.1.7"),sQuery(id+"F0.wireOp",EDGE,"E10.1.8"),sQuery(id+"F0.wireOp",EDGE,"E10.1.9"),sQuery(id+"F0.wireOp",EDGE,"E10.1.10"),sQuery(id+"F0.wireOp",EDGE,"E10.1.11"),sQuery(id+"F0.wireOp",EDGE,"E10.1.12"),sQuery(id+"F0.wireOp",EDGE,"E10.1.14"),sQuery(id+"F0.wireOp",EDGE,"E10.1.15"),sQuery(id+"F0.wireOp",EDGE,"E10.1.16"),sQuery(id+"F0.wireOp",EDGE,"E10.1.18"),sQuery(id+"F0.wireOp",EDGE,"E10.1.20"),sQuery(id+"F0.wireOp",EDGE,"E10.2.0"),sQuery(id+"F0.wireOp",EDGE,"E10.2.1"),sQuery(id+"F0.wireOp",EDGE,"E10.2.2"),sQuery(id+"F0.wireOp",EDGE,"E10.2.3"),sQuery(id+"F0.wireOp",EDGE,"E10.2.5"),sQuery(id+"F0.wireOp",EDGE,"E10.2.7"),sQuery(id+"F0.wireOp",EDGE,"E10.2.8"),sQuery(id+"F0.wireOp",EDGE,"E10.2.9"),sQuery(id+"F0.wireOp",EDGE,"E10.2.10"),sQuery(id+"F0.wireOp",EDGE,"E10.2.11"),sQuery(id+"F0.wireOp",EDGE,"E10.2.12"),sQuery(id+"F0.wireOp",EDGE,"E1"),sQuery(id+"F0.wireOp",EDGE,"E10.2.14"),sQuery(id+"F0.wireOp",EDGE,"E10.2.15"),sQuery(id+"F0.wireOp",EDGE,"E10.2.16"),sQuery(id+"F0.wireOp",EDGE,"E10.2.18"),sQuery(id+"F0.wireOp",EDGE,"E10.2.20"),sQuery(id+"F0.wireOp",EDGE,"E8.trimOffspring"),sQuery(id+"F0.wireOp",EDGE,"E0"),sQuery(id+"F0.wireOp",EDGE,"E10.1.6"),sQuery(id+"F0.wireOp",EDGE,"E11"),sQuery(id+"F0.wireOp",EDGE,"E12"),sQuery(id+"F0.wireOp",EDGE,"E13.1.0"),sQuery(id+"F0.wireOp",EDGE,"E13.1.1"),sQuery(id+"F0.wireOp",EDGE,"E13.2.0"),sQuery(id+"F0.wireOp",EDGE,"E13.2.1")])]}),"instanceName":"1"}),"instanceName":"1"}),"instanceName":"1"}),"instanceName":"1"});
            transform(context, id + "F48", {"entities" : qUnion([Q0]), "transformType" : TransformType.TRANSLATION_3D, "dx" : 52.9 * mm, "dy" : -47.6 * mm, "dz" : 0 * mm, "makeCopy" : true});
        }
        {
            var Q0;
            Q0=makeQuery(id+"F48.opPattern","COPY",BODY,{"derivedFrom":makeQuery(id+"F39.opPattern","COPY",BODY,{"derivedFrom":makeQuery(id+"F36.opPattern","COPY",BODY,{"derivedFrom":makeQuery(id+"F23.opPattern","COPY",BODY,{"derivedFrom":makeQuery(id+"F7.opPattern","COPY",BODY,{"derivedFrom":makeQuery(id+"F1.opExtrude","SWEPT_BODY",BODY,{"disambiguationData":[OSD([sQuery(id+"F0.wireOp",EDGE,"E2.0"),sQuery(id+"F0.wireOp",EDGE,"E2.1"),sQuery(id+"F0.wireOp",EDGE,"E2.2"),sQuery(id+"F0.wireOp",EDGE,"E2.3"),sQuery(id+"F0.wireOp",EDGE,"E2.4"),sQuery(id+"F0.wireOp",EDGE,"E2.5"),sQuery(id+"F0.wireOp",EDGE,"E3"),sQuery(id+"F0.wireOp",EDGE,"E4"),sQuery(id+"F0.wireOp",EDGE,"E5.0"),sQuery(id+"F0.wireOp",EDGE,"E5.1"),sQuery(id+"F0.wireOp",EDGE,"E5.3"),sQuery(id+"F0.wireOp",EDGE,"E5.4"),sQuery(id+"F0.wireOp",EDGE,"E5.5"),sQuery(id+"F0.wireOp",EDGE,"E6.trimOffspring"),sQuery(id+"F0.wireOp",EDGE,"E7.trimOffspring"),sQuery(id+"F0.wireOp",EDGE,"E9.trimOffspring"),sQuery(id+"F0.wireOp",EDGE,"E10.1.0"),sQuery(id+"F0.wireOp",EDGE,"E10.1.1"),sQuery(id+"F0.wireOp",EDGE,"E10.1.2"),sQuery(id+"F0.wireOp",EDGE,"E10.1.3"),sQuery(id+"F0.wireOp",EDGE,"E10.1.5"),sQuery(id+"F0.wireOp",EDGE,"E10.1.7"),sQuery(id+"F0.wireOp",EDGE,"E10.1.8"),sQuery(id+"F0.wireOp",EDGE,"E10.1.9"),sQuery(id+"F0.wireOp",EDGE,"E10.1.10"),sQuery(id+"F0.wireOp",EDGE,"E10.1.11"),sQuery(id+"F0.wireOp",EDGE,"E10.1.12"),sQuery(id+"F0.wireOp",EDGE,"E10.1.14"),sQuery(id+"F0.wireOp",EDGE,"E10.1.15"),sQuery(id+"F0.wireOp",EDGE,"E10.1.16"),sQuery(id+"F0.wireOp",EDGE,"E10.1.18"),sQuery(id+"F0.wireOp",EDGE,"E10.1.20"),sQuery(id+"F0.wireOp",EDGE,"E10.2.0"),sQuery(id+"F0.wireOp",EDGE,"E10.2.1"),sQuery(id+"F0.wireOp",EDGE,"E10.2.2"),sQuery(id+"F0.wireOp",EDGE,"E10.2.3"),sQuery(id+"F0.wireOp",EDGE,"E10.2.5"),sQuery(id+"F0.wireOp",EDGE,"E10.2.7"),sQuery(id+"F0.wireOp",EDGE,"E10.2.8"),sQuery(id+"F0.wireOp",EDGE,"E10.2.9"),sQuery(id+"F0.wireOp",EDGE,"E10.2.10"),sQuery(id+"F0.wireOp",EDGE,"E10.2.11"),sQuery(id+"F0.wireOp",EDGE,"E10.2.12"),sQuery(id+"F0.wireOp",EDGE,"E1"),sQuery(id+"F0.wireOp",EDGE,"E10.2.14"),sQuery(id+"F0.wireOp",EDGE,"E10.2.15"),sQuery(id+"F0.wireOp",EDGE,"E10.2.16"),sQuery(id+"F0.wireOp",EDGE,"E10.2.18"),sQuery(id+"F0.wireOp",EDGE,"E10.2.20"),sQuery(id+"F0.wireOp",EDGE,"E8.trimOffspring"),sQuery(id+"F0.wireOp",EDGE,"E0"),sQuery(id+"F0.wireOp",EDGE,"E10.1.6"),sQuery(id+"F0.wireOp",EDGE,"E11"),sQuery(id+"F0.wireOp",EDGE,"E12"),sQuery(id+"F0.wireOp",EDGE,"E13.1.0"),sQuery(id+"F0.wireOp",EDGE,"E13.1.1"),sQuery(id+"F0.wireOp",EDGE,"E13.2.0"),sQuery(id+"F0.wireOp",EDGE,"E13.2.1")])]}),"instanceName":"1"}),"instanceName":"1"}),"instanceName":"1"}),"instanceName":"1"}),"instanceName":"1"});
            var Q1;
            Q1=makeQuery(id+"F48.opPattern","COPY",EDGE,{"derivedFrom":makeQuery(id+"F39.opPattern","COPY",EDGE,{"derivedFrom":makeQuery(id+"F36.opPattern","COPY",EDGE,{"derivedFrom":makeQuery(id+"F23.opPattern","COPY",EDGE,{"derivedFrom":makeQuery(id+"F7.opPattern","COPY",EDGE,{"derivedFrom":makeQuery(id+"F1.opExtrude","CAP_EDGE",EDGE,{"disambiguationData":[OSD([sQuery(id+"F0.wireOp",EDGE,"E1")])],"isStart":false}),"instanceName":"1"}),"instanceName":"1"}),"instanceName":"1"}),"instanceName":"1"}),"instanceName":"1"});
            transform(context, id + "F49", {"entities" : qUnion([Q0]), "transformType" : TransformType.ROTATION, "transformAxis" : qUnion([Q1]), "angle" : 70 * degree, "makeCopy" : false});
        }
        {
            var Q0;
            Q0=makeQuery(id+"F48.opPattern","COPY",BODY,{"derivedFrom":makeQuery(id+"F39.opPattern","COPY",BODY,{"derivedFrom":makeQuery(id+"F36.opPattern","COPY",BODY,{"derivedFrom":makeQuery(id+"F23.opPattern","COPY",BODY,{"derivedFrom":makeQuery(id+"F7.opPattern","COPY",BODY,{"derivedFrom":makeQuery(id+"F1.opExtrude","SWEPT_BODY",BODY,{"disambiguationData":[OSD([sQuery(id+"F0.wireOp",EDGE,"E2.0"),sQuery(id+"F0.wireOp",EDGE,"E2.1"),sQuery(id+"F0.wireOp",EDGE,"E2.2"),sQuery(id+"F0.wireOp",EDGE,"E2.3"),sQuery(id+"F0.wireOp",EDGE,"E2.4"),sQuery(id+"F0.wireOp",EDGE,"E2.5"),sQuery(id+"F0.wireOp",EDGE,"E3"),sQuery(id+"F0.wireOp",EDGE,"E4"),sQuery(id+"F0.wireOp",EDGE,"E5.0"),sQuery(id+"F0.wireOp",EDGE,"E5.1"),sQuery(id+"F0.wireOp",EDGE,"E5.3"),sQuery(id+"F0.wireOp",EDGE,"E5.4"),sQuery(id+"F0.wireOp",EDGE,"E5.5"),sQuery(id+"F0.wireOp",EDGE,"E6.trimOffspring"),sQuery(id+"F0.wireOp",EDGE,"E7.trimOffspring"),sQuery(id+"F0.wireOp",EDGE,"E9.trimOffspring"),sQuery(id+"F0.wireOp",EDGE,"E10.1.0"),sQuery(id+"F0.wireOp",EDGE,"E10.1.1"),sQuery(id+"F0.wireOp",EDGE,"E10.1.2"),sQuery(id+"F0.wireOp",EDGE,"E10.1.3"),sQuery(id+"F0.wireOp",EDGE,"E10.1.5"),sQuery(id+"F0.wireOp",EDGE,"E10.1.7"),sQuery(id+"F0.wireOp",EDGE,"E10.1.8"),sQuery(id+"F0.wireOp",EDGE,"E10.1.9"),sQuery(id+"F0.wireOp",EDGE,"E10.1.10"),sQuery(id+"F0.wireOp",EDGE,"E10.1.11"),sQuery(id+"F0.wireOp",EDGE,"E10.1.12"),sQuery(id+"F0.wireOp",EDGE,"E10.1.14"),sQuery(id+"F0.wireOp",EDGE,"E10.1.15"),sQuery(id+"F0.wireOp",EDGE,"E10.1.16"),sQuery(id+"F0.wireOp",EDGE,"E10.1.18"),sQuery(id+"F0.wireOp",EDGE,"E10.1.20"),sQuery(id+"F0.wireOp",EDGE,"E10.2.0"),sQuery(id+"F0.wireOp",EDGE,"E10.2.1"),sQuery(id+"F0.wireOp",EDGE,"E10.2.2"),sQuery(id+"F0.wireOp",EDGE,"E10.2.3"),sQuery(id+"F0.wireOp",EDGE,"E10.2.5"),sQuery(id+"F0.wireOp",EDGE,"E10.2.7"),sQuery(id+"F0.wireOp",EDGE,"E10.2.8"),sQuery(id+"F0.wireOp",EDGE,"E10.2.9"),sQuery(id+"F0.wireOp",EDGE,"E10.2.10"),sQuery(id+"F0.wireOp",EDGE,"E10.2.11"),sQuery(id+"F0.wireOp",EDGE,"E10.2.12"),sQuery(id+"F0.wireOp",EDGE,"E1"),sQuery(id+"F0.wireOp",EDGE,"E10.2.14"),sQuery(id+"F0.wireOp",EDGE,"E10.2.15"),sQuery(id+"F0.wireOp",EDGE,"E10.2.16"),sQuery(id+"F0.wireOp",EDGE,"E10.2.18"),sQuery(id+"F0.wireOp",EDGE,"E10.2.20"),sQuery(id+"F0.wireOp",EDGE,"E8.trimOffspring"),sQuery(id+"F0.wireOp",EDGE,"E0"),sQuery(id+"F0.wireOp",EDGE,"E10.1.6"),sQuery(id+"F0.wireOp",EDGE,"E11"),sQuery(id+"F0.wireOp",EDGE,"E12"),sQuery(id+"F0.wireOp",EDGE,"E13.1.0"),sQuery(id+"F0.wireOp",EDGE,"E13.1.1"),sQuery(id+"F0.wireOp",EDGE,"E13.2.0"),sQuery(id+"F0.wireOp",EDGE,"E13.2.1")])]}),"instanceName":"1"}),"instanceName":"1"}),"instanceName":"1"}),"instanceName":"1"}),"instanceName":"1"});
            transform(context, id + "F50", {"entities" : qUnion([Q0]), "transformType" : TransformType.TRANSLATION_3D, "dx" : 9.2 * mm, "dy" : 0 * mm, "dz" : 0 * mm, "makeCopy" : false});
        }
        {
            var Q0;
            Q0=makeQuery(id+"F39.opPattern","COPY",BODY,{"derivedFrom":makeQuery(id+"F36.opPattern","COPY",BODY,{"derivedFrom":makeQuery(id+"F23.opPattern","COPY",BODY,{"derivedFrom":makeQuery(id+"F7.opPattern","COPY",BODY,{"derivedFrom":makeQuery(id+"F1.opExtrude","SWEPT_BODY",BODY,{"disambiguationData":[OSD([sQuery(id+"F0.wireOp",EDGE,"E2.0"),sQuery(id+"F0.wireOp",EDGE,"E2.1"),sQuery(id+"F0.wireOp",EDGE,"E2.2"),sQuery(id+"F0.wireOp",EDGE,"E2.3"),sQuery(id+"F0.wireOp",EDGE,"E2.4"),sQuery(id+"F0.wireOp",EDGE,"E2.5"),sQuery(id+"F0.wireOp",EDGE,"E3"),sQuery(id+"F0.wireOp",EDGE,"E4"),sQuery(id+"F0.wireOp",EDGE,"E5.0"),sQuery(id+"F0.wireOp",EDGE,"E5.1"),sQuery(id+"F0.wireOp",EDGE,"E5.3"),sQuery(id+"F0.wireOp",EDGE,"E5.4"),sQuery(id+"F0.wireOp",EDGE,"E5.5"),sQuery(id+"F0.wireOp",EDGE,"E6.trimOffspring"),sQuery(id+"F0.wireOp",EDGE,"E7.trimOffspring"),sQuery(id+"F0.wireOp",EDGE,"E9.trimOffspring"),sQuery(id+"F0.wireOp",EDGE,"E10.1.0"),sQuery(id+"F0.wireOp",EDGE,"E10.1.1"),sQuery(id+"F0.wireOp",EDGE,"E10.1.2"),sQuery(id+"F0.wireOp",EDGE,"E10.1.3"),sQuery(id+"F0.wireOp",EDGE,"E10.1.5"),sQuery(id+"F0.wireOp",EDGE,"E10.1.7"),sQuery(id+"F0.wireOp",EDGE,"E10.1.8"),sQuery(id+"F0.wireOp",EDGE,"E10.1.9"),sQuery(id+"F0.wireOp",EDGE,"E10.1.10"),sQuery(id+"F0.wireOp",EDGE,"E10.1.11"),sQuery(id+"F0.wireOp",EDGE,"E10.1.12"),sQuery(id+"F0.wireOp",EDGE,"E10.1.14"),sQuery(id+"F0.wireOp",EDGE,"E10.1.15"),sQuery(id+"F0.wireOp",EDGE,"E10.1.16"),sQuery(id+"F0.wireOp",EDGE,"E10.1.18"),sQuery(id+"F0.wireOp",EDGE,"E10.1.20"),sQuery(id+"F0.wireOp",EDGE,"E10.2.0"),sQuery(id+"F0.wireOp",EDGE,"E10.2.1"),sQuery(id+"F0.wireOp",EDGE,"E10.2.2"),sQuery(id+"F0.wireOp",EDGE,"E10.2.3"),sQuery(id+"F0.wireOp",EDGE,"E10.2.5"),sQuery(id+"F0.wireOp",EDGE,"E10.2.7"),sQuery(id+"F0.wireOp",EDGE,"E10.2.8"),sQuery(id+"F0.wireOp",EDGE,"E10.2.9"),sQuery(id+"F0.wireOp",EDGE,"E10.2.10"),sQuery(id+"F0.wireOp",EDGE,"E10.2.11"),sQuery(id+"F0.wireOp",EDGE,"E10.2.12"),sQuery(id+"F0.wireOp",EDGE,"E1"),sQuery(id+"F0.wireOp",EDGE,"E10.2.14"),sQuery(id+"F0.wireOp",EDGE,"E10.2.15"),sQuery(id+"F0.wireOp",EDGE,"E10.2.16"),sQuery(id+"F0.wireOp",EDGE,"E10.2.18"),sQuery(id+"F0.wireOp",EDGE,"E10.2.20"),sQuery(id+"F0.wireOp",EDGE,"E8.trimOffspring"),sQuery(id+"F0.wireOp",EDGE,"E0"),sQuery(id+"F0.wireOp",EDGE,"E10.1.6"),sQuery(id+"F0.wireOp",EDGE,"E11"),sQuery(id+"F0.wireOp",EDGE,"E12"),sQuery(id+"F0.wireOp",EDGE,"E13.1.0"),sQuery(id+"F0.wireOp",EDGE,"E13.1.1"),sQuery(id+"F0.wireOp",EDGE,"E13.2.0"),sQuery(id+"F0.wireOp",EDGE,"E13.2.1")])]}),"instanceName":"1"}),"instanceName":"1"}),"instanceName":"1"}),"instanceName":"1"});
            transform(context, id + "F51", {"entities" : qUnion([Q0]), "transformType" : TransformType.TRANSLATION_3D, "dx" : 14.9 * mm, "dy" : -87 * mm, "dz" : 0 * mm, "makeCopy" : true});
        }
        {
            var Q0;
            Q0=makeQuery(id+"F39.opPattern","COPY",BODY,{"derivedFrom":makeQuery(id+"F36.opPattern","COPY",BODY,{"derivedFrom":makeQuery(id+"F23.opPattern","COPY",BODY,{"derivedFrom":makeQuery(id+"F7.opPattern","COPY",BODY,{"derivedFrom":makeQuery(id+"F1.opExtrude","SWEPT_BODY",BODY,{"disambiguationData":[OSD([sQuery(id+"F0.wireOp",EDGE,"E2.0"),sQuery(id+"F0.wireOp",EDGE,"E2.1"),sQuery(id+"F0.wireOp",EDGE,"E2.2"),sQuery(id+"F0.wireOp",EDGE,"E2.3"),sQuery(id+"F0.wireOp",EDGE,"E2.4"),sQuery(id+"F0.wireOp",EDGE,"E2.5"),sQuery(id+"F0.wireOp",EDGE,"E3"),sQuery(id+"F0.wireOp",EDGE,"E4"),sQuery(id+"F0.wireOp",EDGE,"E5.0"),sQuery(id+"F0.wireOp",EDGE,"E5.1"),sQuery(id+"F0.wireOp",EDGE,"E5.3"),sQuery(id+"F0.wireOp",EDGE,"E5.4"),sQuery(id+"F0.wireOp",EDGE,"E5.5"),sQuery(id+"F0.wireOp",EDGE,"E6.trimOffspring"),sQuery(id+"F0.wireOp",EDGE,"E7.trimOffspring"),sQuery(id+"F0.wireOp",EDGE,"E9.trimOffspring"),sQuery(id+"F0.wireOp",EDGE,"E10.1.0"),sQuery(id+"F0.wireOp",EDGE,"E10.1.1"),sQuery(id+"F0.wireOp",EDGE,"E10.1.2"),sQuery(id+"F0.wireOp",EDGE,"E10.1.3"),sQuery(id+"F0.wireOp",EDGE,"E10.1.5"),sQuery(id+"F0.wireOp",EDGE,"E10.1.7"),sQuery(id+"F0.wireOp",EDGE,"E10.1.8"),sQuery(id+"F0.wireOp",EDGE,"E10.1.9"),sQuery(id+"F0.wireOp",EDGE,"E10.1.10"),sQuery(id+"F0.wireOp",EDGE,"E10.1.11"),sQuery(id+"F0.wireOp",EDGE,"E10.1.12"),sQuery(id+"F0.wireOp",EDGE,"E10.1.14"),sQuery(id+"F0.wireOp",EDGE,"E10.1.15"),sQuery(id+"F0.wireOp",EDGE,"E10.1.16"),sQuery(id+"F0.wireOp",EDGE,"E10.1.18"),sQuery(id+"F0.wireOp",EDGE,"E10.1.20"),sQuery(id+"F0.wireOp",EDGE,"E10.2.0"),sQuery(id+"F0.wireOp",EDGE,"E10.2.1"),sQuery(id+"F0.wireOp",EDGE,"E10.2.2"),sQuery(id+"F0.wireOp",EDGE,"E10.2.3"),sQuery(id+"F0.wireOp",EDGE,"E10.2.5"),sQuery(id+"F0.wireOp",EDGE,"E10.2.7"),sQuery(id+"F0.wireOp",EDGE,"E10.2.8"),sQuery(id+"F0.wireOp",EDGE,"E10.2.9"),sQuery(id+"F0.wireOp",EDGE,"E10.2.10"),sQuery(id+"F0.wireOp",EDGE,"E10.2.11"),sQuery(id+"F0.wireOp",EDGE,"E10.2.12"),sQuery(id+"F0.wireOp",EDGE,"E1"),sQuery(id+"F0.wireOp",EDGE,"E10.2.14"),sQuery(id+"F0.wireOp",EDGE,"E10.2.15"),sQuery(id+"F0.wireOp",EDGE,"E10.2.16"),sQuery(id+"F0.wireOp",EDGE,"E10.2.18"),sQuery(id+"F0.wireOp",EDGE,"E10.2.20"),sQuery(id+"F0.wireOp",EDGE,"E8.trimOffspring"),sQuery(id+"F0.wireOp",EDGE,"E0"),sQuery(id+"F0.wireOp",EDGE,"E10.1.6"),sQuery(id+"F0.wireOp",EDGE,"E11"),sQuery(id+"F0.wireOp",EDGE,"E12"),sQuery(id+"F0.wireOp",EDGE,"E13.1.0"),sQuery(id+"F0.wireOp",EDGE,"E13.1.1"),sQuery(id+"F0.wireOp",EDGE,"E13.2.0"),sQuery(id+"F0.wireOp",EDGE,"E13.2.1")])]}),"instanceName":"1"}),"instanceName":"1"}),"instanceName":"1"}),"instanceName":"1"});
            transform(context, id + "F52", {"entities" : qUnion([Q0]), "transformType" : TransformType.TRANSLATION_3D, "dx" : -277.2 * mm, "dy" : -90.1 * mm, "dz" : 0 * mm, "makeCopy" : true});
        }
        {
            var Q0;
            Q0=makeQuery(id+"F52.opPattern","COPY",BODY,{"derivedFrom":makeQuery(id+"F39.opPattern","COPY",BODY,{"derivedFrom":makeQuery(id+"F36.opPattern","COPY",BODY,{"derivedFrom":makeQuery(id+"F23.opPattern","COPY",BODY,{"derivedFrom":makeQuery(id+"F7.opPattern","COPY",BODY,{"derivedFrom":makeQuery(id+"F1.opExtrude","SWEPT_BODY",BODY,{"disambiguationData":[OSD([sQuery(id+"F0.wireOp",EDGE,"E2.0"),sQuery(id+"F0.wireOp",EDGE,"E2.1"),sQuery(id+"F0.wireOp",EDGE,"E2.2"),sQuery(id+"F0.wireOp",EDGE,"E2.3"),sQuery(id+"F0.wireOp",EDGE,"E2.4"),sQuery(id+"F0.wireOp",EDGE,"E2.5"),sQuery(id+"F0.wireOp",EDGE,"E3"),sQuery(id+"F0.wireOp",EDGE,"E4"),sQuery(id+"F0.wireOp",EDGE,"E5.0"),sQuery(id+"F0.wireOp",EDGE,"E5.1"),sQuery(id+"F0.wireOp",EDGE,"E5.3"),sQuery(id+"F0.wireOp",EDGE,"E5.4"),sQuery(id+"F0.wireOp",EDGE,"E5.5"),sQuery(id+"F0.wireOp",EDGE,"E6.trimOffspring"),sQuery(id+"F0.wireOp",EDGE,"E7.trimOffspring"),sQuery(id+"F0.wireOp",EDGE,"E9.trimOffspring"),sQuery(id+"F0.wireOp",EDGE,"E10.1.0"),sQuery(id+"F0.wireOp",EDGE,"E10.1.1"),sQuery(id+"F0.wireOp",EDGE,"E10.1.2"),sQuery(id+"F0.wireOp",EDGE,"E10.1.3"),sQuery(id+"F0.wireOp",EDGE,"E10.1.5"),sQuery(id+"F0.wireOp",EDGE,"E10.1.7"),sQuery(id+"F0.wireOp",EDGE,"E10.1.8"),sQuery(id+"F0.wireOp",EDGE,"E10.1.9"),sQuery(id+"F0.wireOp",EDGE,"E10.1.10"),sQuery(id+"F0.wireOp",EDGE,"E10.1.11"),sQuery(id+"F0.wireOp",EDGE,"E10.1.12"),sQuery(id+"F0.wireOp",EDGE,"E10.1.14"),sQuery(id+"F0.wireOp",EDGE,"E10.1.15"),sQuery(id+"F0.wireOp",EDGE,"E10.1.16"),sQuery(id+"F0.wireOp",EDGE,"E10.1.18"),sQuery(id+"F0.wireOp",EDGE,"E10.1.20"),sQuery(id+"F0.wireOp",EDGE,"E10.2.0"),sQuery(id+"F0.wireOp",EDGE,"E10.2.1"),sQuery(id+"F0.wireOp",EDGE,"E10.2.2"),sQuery(id+"F0.wireOp",EDGE,"E10.2.3"),sQuery(id+"F0.wireOp",EDGE,"E10.2.5"),sQuery(id+"F0.wireOp",EDGE,"E10.2.7"),sQuery(id+"F0.wireOp",EDGE,"E10.2.8"),sQuery(id+"F0.wireOp",EDGE,"E10.2.9"),sQuery(id+"F0.wireOp",EDGE,"E10.2.10"),sQuery(id+"F0.wireOp",EDGE,"E10.2.11"),sQuery(id+"F0.wireOp",EDGE,"E10.2.12"),sQuery(id+"F0.wireOp",EDGE,"E1"),sQuery(id+"F0.wireOp",EDGE,"E10.2.14"),sQuery(id+"F0.wireOp",EDGE,"E10.2.15"),sQuery(id+"F0.wireOp",EDGE,"E10.2.16"),sQuery(id+"F0.wireOp",EDGE,"E10.2.18"),sQuery(id+"F0.wireOp",EDGE,"E10.2.20"),sQuery(id+"F0.wireOp",EDGE,"E8.trimOffspring"),sQuery(id+"F0.wireOp",EDGE,"E0"),sQuery(id+"F0.wireOp",EDGE,"E10.1.6"),sQuery(id+"F0.wireOp",EDGE,"E11"),sQuery(id+"F0.wireOp",EDGE,"E12"),sQuery(id+"F0.wireOp",EDGE,"E13.1.0"),sQuery(id+"F0.wireOp",EDGE,"E13.1.1"),sQuery(id+"F0.wireOp",EDGE,"E13.2.0"),sQuery(id+"F0.wireOp",EDGE,"E13.2.1")])]}),"instanceName":"1"}),"instanceName":"1"}),"instanceName":"1"}),"instanceName":"1"}),"instanceName":"1"});
            transform(context, id + "F53", {"entities" : qUnion([Q0]), "transformType" : TransformType.TRANSLATION_3D, "dx" : 69.1 * mm, "dy" : -4.4 * mm, "dz" : 0 * mm, "makeCopy" : true});
        }
        {
            var Q0;
            Q0=makeQuery(id+"F36.opPattern","COPY",BODY,{"derivedFrom":makeQuery(id+"F23.opPattern","COPY",BODY,{"derivedFrom":makeQuery(id+"F7.opPattern","COPY",BODY,{"derivedFrom":makeQuery(id+"F1.opExtrude","SWEPT_BODY",BODY,{"disambiguationData":[OSD([sQuery(id+"F0.wireOp",EDGE,"E2.0"),sQuery(id+"F0.wireOp",EDGE,"E2.1"),sQuery(id+"F0.wireOp",EDGE,"E2.2"),sQuery(id+"F0.wireOp",EDGE,"E2.3"),sQuery(id+"F0.wireOp",EDGE,"E2.4"),sQuery(id+"F0.wireOp",EDGE,"E2.5"),sQuery(id+"F0.wireOp",EDGE,"E3"),sQuery(id+"F0.wireOp",EDGE,"E4"),sQuery(id+"F0.wireOp",EDGE,"E5.0"),sQuery(id+"F0.wireOp",EDGE,"E5.1"),sQuery(id+"F0.wireOp",EDGE,"E5.3"),sQuery(id+"F0.wireOp",EDGE,"E5.4"),sQuery(id+"F0.wireOp",EDGE,"E5.5"),sQuery(id+"F0.wireOp",EDGE,"E6.trimOffspring"),sQuery(id+"F0.wireOp",EDGE,"E7.trimOffspring"),sQuery(id+"F0.wireOp",EDGE,"E9.trimOffspring"),sQuery(id+"F0.wireOp",EDGE,"E10.1.0"),sQuery(id+"F0.wireOp",EDGE,"E10.1.1"),sQuery(id+"F0.wireOp",EDGE,"E10.1.2"),sQuery(id+"F0.wireOp",EDGE,"E10.1.3"),sQuery(id+"F0.wireOp",EDGE,"E10.1.5"),sQuery(id+"F0.wireOp",EDGE,"E10.1.7"),sQuery(id+"F0.wireOp",EDGE,"E10.1.8"),sQuery(id+"F0.wireOp",EDGE,"E10.1.9"),sQuery(id+"F0.wireOp",EDGE,"E10.1.10"),sQuery(id+"F0.wireOp",EDGE,"E10.1.11"),sQuery(id+"F0.wireOp",EDGE,"E10.1.12"),sQuery(id+"F0.wireOp",EDGE,"E10.1.14"),sQuery(id+"F0.wireOp",EDGE,"E10.1.15"),sQuery(id+"F0.wireOp",EDGE,"E10.1.16"),sQuery(id+"F0.wireOp",EDGE,"E10.1.18"),sQuery(id+"F0.wireOp",EDGE,"E10.1.20"),sQuery(id+"F0.wireOp",EDGE,"E10.2.0"),sQuery(id+"F0.wireOp",EDGE,"E10.2.1"),sQuery(id+"F0.wireOp",EDGE,"E10.2.2"),sQuery(id+"F0.wireOp",EDGE,"E10.2.3"),sQuery(id+"F0.wireOp",EDGE,"E10.2.5"),sQuery(id+"F0.wireOp",EDGE,"E10.2.7"),sQuery(id+"F0.wireOp",EDGE,"E10.2.8"),sQuery(id+"F0.wireOp",EDGE,"E10.2.9"),sQuery(id+"F0.wireOp",EDGE,"E10.2.10"),sQuery(id+"F0.wireOp",EDGE,"E10.2.11"),sQuery(id+"F0.wireOp",EDGE,"E10.2.12"),sQuery(id+"F0.wireOp",EDGE,"E1"),sQuery(id+"F0.wireOp",EDGE,"E10.2.14"),sQuery(id+"F0.wireOp",EDGE,"E10.2.15"),sQuery(id+"F0.wireOp",EDGE,"E10.2.16"),sQuery(id+"F0.wireOp",EDGE,"E10.2.18"),sQuery(id+"F0.wireOp",EDGE,"E10.2.20"),sQuery(id+"F0.wireOp",EDGE,"E8.trimOffspring"),sQuery(id+"F0.wireOp",EDGE,"E0"),sQuery(id+"F0.wireOp",EDGE,"E10.1.6"),sQuery(id+"F0.wireOp",EDGE,"E11"),sQuery(id+"F0.wireOp",EDGE,"E12"),sQuery(id+"F0.wireOp",EDGE,"E13.1.0"),sQuery(id+"F0.wireOp",EDGE,"E13.1.1"),sQuery(id+"F0.wireOp",EDGE,"E13.2.0"),sQuery(id+"F0.wireOp",EDGE,"E13.2.1")])]}),"instanceName":"1"}),"instanceName":"1"}),"instanceName":"1"});
            transform(context, id + "F54", {"entities" : qUnion([Q0]), "transformType" : TransformType.TRANSLATION_3D, "dx" : -74.8 * mm, "dy" : -122.1 * mm, "dz" : 0 * mm, "makeCopy" : true});
        }
        {
            var Q0;
            Q0=makeQuery(id+"F46.opPattern","COPY",BODY,{"derivedFrom":makeQuery(id+"F45.opPattern","COPY",BODY,{"derivedFrom":makeQuery(id+"F5.opPattern","COPY",BODY,{"derivedFrom":makeQuery(id+"F1.opExtrude","SWEPT_BODY",BODY,{"disambiguationData":[OSD([sQuery(id+"F0.wireOp",EDGE,"E2.0"),sQuery(id+"F0.wireOp",EDGE,"E2.1"),sQuery(id+"F0.wireOp",EDGE,"E2.2"),sQuery(id+"F0.wireOp",EDGE,"E2.3"),sQuery(id+"F0.wireOp",EDGE,"E2.4"),sQuery(id+"F0.wireOp",EDGE,"E2.5"),sQuery(id+"F0.wireOp",EDGE,"E3"),sQuery(id+"F0.wireOp",EDGE,"E4"),sQuery(id+"F0.wireOp",EDGE,"E5.0"),sQuery(id+"F0.wireOp",EDGE,"E5.1"),sQuery(id+"F0.wireOp",EDGE,"E5.3"),sQuery(id+"F0.wireOp",EDGE,"E5.4"),sQuery(id+"F0.wireOp",EDGE,"E5.5"),sQuery(id+"F0.wireOp",EDGE,"E6.trimOffspring"),sQuery(id+"F0.wireOp",EDGE,"E7.trimOffspring"),sQuery(id+"F0.wireOp",EDGE,"E9.trimOffspring"),sQuery(id+"F0.wireOp",EDGE,"E10.1.0"),sQuery(id+"F0.wireOp",EDGE,"E10.1.1"),sQuery(id+"F0.wireOp",EDGE,"E10.1.2"),sQuery(id+"F0.wireOp",EDGE,"E10.1.3"),sQuery(id+"F0.wireOp",EDGE,"E10.1.5"),sQuery(id+"F0.wireOp",EDGE,"E10.1.7"),sQuery(id+"F0.wireOp",EDGE,"E10.1.8"),sQuery(id+"F0.wireOp",EDGE,"E10.1.9"),sQuery(id+"F0.wireOp",EDGE,"E10.1.10"),sQuery(id+"F0.wireOp",EDGE,"E10.1.11"),sQuery(id+"F0.wireOp",EDGE,"E10.1.12"),sQuery(id+"F0.wireOp",EDGE,"E10.1.14"),sQuery(id+"F0.wireOp",EDGE,"E10.1.15"),sQuery(id+"F0.wireOp",EDGE,"E10.1.16"),sQuery(id+"F0.wireOp",EDGE,"E10.1.18"),sQuery(id+"F0.wireOp",EDGE,"E10.1.20"),sQuery(id+"F0.wireOp",EDGE,"E10.2.0"),sQuery(id+"F0.wireOp",EDGE,"E10.2.1"),sQuery(id+"F0.wireOp",EDGE,"E10.2.2"),sQuery(id+"F0.wireOp",EDGE,"E10.2.3"),sQuery(id+"F0.wireOp",EDGE,"E10.2.5"),sQuery(id+"F0.wireOp",EDGE,"E10.2.7"),sQuery(id+"F0.wireOp",EDGE,"E10.2.8"),sQuery(id+"F0.wireOp",EDGE,"E10.2.9"),sQuery(id+"F0.wireOp",EDGE,"E10.2.10"),sQuery(id+"F0.wireOp",EDGE,"E10.2.11"),sQuery(id+"F0.wireOp",EDGE,"E10.2.12"),sQuery(id+"F0.wireOp",EDGE,"E1"),sQuery(id+"F0.wireOp",EDGE,"E10.2.14"),sQuery(id+"F0.wireOp",EDGE,"E10.2.15"),sQuery(id+"F0.wireOp",EDGE,"E10.2.16"),sQuery(id+"F0.wireOp",EDGE,"E10.2.18"),sQuery(id+"F0.wireOp",EDGE,"E10.2.20"),sQuery(id+"F0.wireOp",EDGE,"E8.trimOffspring"),sQuery(id+"F0.wireOp",EDGE,"E0"),sQuery(id+"F0.wireOp",EDGE,"E10.1.6"),sQuery(id+"F0.wireOp",EDGE,"E11"),sQuery(id+"F0.wireOp",EDGE,"E12"),sQuery(id+"F0.wireOp",EDGE,"E13.1.0"),sQuery(id+"F0.wireOp",EDGE,"E13.1.1"),sQuery(id+"F0.wireOp",EDGE,"E13.2.0"),sQuery(id+"F0.wireOp",EDGE,"E13.2.1")])]}),"instanceName":"1"}),"instanceName":"1"}),"instanceName":"1"});
            transform(context, id + "F55", {"entities" : qUnion([Q0]), "transformType" : TransformType.TRANSLATION_3D, "dx" : 35.5 * mm, "dy" : -80.4 * mm, "dz" : 0 * mm, "makeCopy" : true});
        }
        {
            var Q0;
            Q0=makeQuery(id+"F18.opPattern","COPY",BODY,{"derivedFrom":makeQuery(id+"F13.opPattern","COPY",BODY,{"derivedFrom":makeQuery(id+"F1.opExtrude","SWEPT_BODY",BODY,{"disambiguationData":[OSD([sQuery(id+"F0.wireOp",EDGE,"E2.0"),sQuery(id+"F0.wireOp",EDGE,"E2.1"),sQuery(id+"F0.wireOp",EDGE,"E2.2"),sQuery(id+"F0.wireOp",EDGE,"E2.3"),sQuery(id+"F0.wireOp",EDGE,"E2.4"),sQuery(id+"F0.wireOp",EDGE,"E2.5"),sQuery(id+"F0.wireOp",EDGE,"E3"),sQuery(id+"F0.wireOp",EDGE,"E4"),sQuery(id+"F0.wireOp",EDGE,"E5.0"),sQuery(id+"F0.wireOp",EDGE,"E5.1"),sQuery(id+"F0.wireOp",EDGE,"E5.3"),sQuery(id+"F0.wireOp",EDGE,"E5.4"),sQuery(id+"F0.wireOp",EDGE,"E5.5"),sQuery(id+"F0.wireOp",EDGE,"E6.trimOffspring"),sQuery(id+"F0.wireOp",EDGE,"E7.trimOffspring"),sQuery(id+"F0.wireOp",EDGE,"E9.trimOffspring"),sQuery(id+"F0.wireOp",EDGE,"E10.1.0"),sQuery(id+"F0.wireOp",EDGE,"E10.1.1"),sQuery(id+"F0.wireOp",EDGE,"E10.1.2"),sQuery(id+"F0.wireOp",EDGE,"E10.1.3"),sQuery(id+"F0.wireOp",EDGE,"E10.1.5"),sQuery(id+"F0.wireOp",EDGE,"E10.1.7"),sQuery(id+"F0.wireOp",EDGE,"E10.1.8"),sQuery(id+"F0.wireOp",EDGE,"E10.1.9"),sQuery(id+"F0.wireOp",EDGE,"E10.1.10"),sQuery(id+"F0.wireOp",EDGE,"E10.1.11"),sQuery(id+"F0.wireOp",EDGE,"E10.1.12"),sQuery(id+"F0.wireOp",EDGE,"E10.1.14"),sQuery(id+"F0.wireOp",EDGE,"E10.1.15"),sQuery(id+"F0.wireOp",EDGE,"E10.1.16"),sQuery(id+"F0.wireOp",EDGE,"E10.1.18"),sQuery(id+"F0.wireOp",EDGE,"E10.1.20"),sQuery(id+"F0.wireOp",EDGE,"E10.2.0"),sQuery(id+"F0.wireOp",EDGE,"E10.2.1"),sQuery(id+"F0.wireOp",EDGE,"E10.2.2"),sQuery(id+"F0.wireOp",EDGE,"E10.2.3"),sQuery(id+"F0.wireOp",EDGE,"E10.2.5"),sQuery(id+"F0.wireOp",EDGE,"E10.2.7"),sQuery(id+"F0.wireOp",EDGE,"E10.2.8"),sQuery(id+"F0.wireOp",EDGE,"E10.2.9"),sQuery(id+"F0.wireOp",EDGE,"E10.2.10"),sQuery(id+"F0.wireOp",EDGE,"E10.2.11"),sQuery(id+"F0.wireOp",EDGE,"E10.2.12"),sQuery(id+"F0.wireOp",EDGE,"E1"),sQuery(id+"F0.wireOp",EDGE,"E10.2.14"),sQuery(id+"F0.wireOp",EDGE,"E10.2.15"),sQuery(id+"F0.wireOp",EDGE,"E10.2.16"),sQuery(id+"F0.wireOp",EDGE,"E10.2.18"),sQuery(id+"F0.wireOp",EDGE,"E10.2.20"),sQuery(id+"F0.wireOp",EDGE,"E8.trimOffspring"),sQuery(id+"F0.wireOp",EDGE,"E0"),sQuery(id+"F0.wireOp",EDGE,"E10.1.6"),sQuery(id+"F0.wireOp",EDGE,"E11"),sQuery(id+"F0.wireOp",EDGE,"E12"),sQuery(id+"F0.wireOp",EDGE,"E13.1.0"),sQuery(id+"F0.wireOp",EDGE,"E13.1.1"),sQuery(id+"F0.wireOp",EDGE,"E13.2.0"),sQuery(id+"F0.wireOp",EDGE,"E13.2.1")])]}),"instanceName":"1"}),"instanceName":"1"});
            var Q1;
            Q1=makeQuery(id+"F13.opPattern","COPY",BODY,{"derivedFrom":makeQuery(id+"F1.opExtrude","SWEPT_BODY",BODY,{"disambiguationData":[OSD([sQuery(id+"F0.wireOp",EDGE,"E2.0"),sQuery(id+"F0.wireOp",EDGE,"E2.1"),sQuery(id+"F0.wireOp",EDGE,"E2.2"),sQuery(id+"F0.wireOp",EDGE,"E2.3"),sQuery(id+"F0.wireOp",EDGE,"E2.4"),sQuery(id+"F0.wireOp",EDGE,"E2.5"),sQuery(id+"F0.wireOp",EDGE,"E3"),sQuery(id+"F0.wireOp",EDGE,"E4"),sQuery(id+"F0.wireOp",EDGE,"E5.0"),sQuery(id+"F0.wireOp",EDGE,"E5.1"),sQuery(id+"F0.wireOp",EDGE,"E5.3"),sQuery(id+"F0.wireOp",EDGE,"E5.4"),sQuery(id+"F0.wireOp",EDGE,"E5.5"),sQuery(id+"F0.wireOp",EDGE,"E6.trimOffspring"),sQuery(id+"F0.wireOp",EDGE,"E7.trimOffspring"),sQuery(id+"F0.wireOp",EDGE,"E9.trimOffspring"),sQuery(id+"F0.wireOp",EDGE,"E10.1.0"),sQuery(id+"F0.wireOp",EDGE,"E10.1.1"),sQuery(id+"F0.wireOp",EDGE,"E10.1.2"),sQuery(id+"F0.wireOp",EDGE,"E10.1.3"),sQuery(id+"F0.wireOp",EDGE,"E10.1.5"),sQuery(id+"F0.wireOp",EDGE,"E10.1.7"),sQuery(id+"F0.wireOp",EDGE,"E10.1.8"),sQuery(id+"F0.wireOp",EDGE,"E10.1.9"),sQuery(id+"F0.wireOp",EDGE,"E10.1.10"),sQuery(id+"F0.wireOp",EDGE,"E10.1.11"),sQuery(id+"F0.wireOp",EDGE,"E10.1.12"),sQuery(id+"F0.wireOp",EDGE,"E10.1.14"),sQuery(id+"F0.wireOp",EDGE,"E10.1.15"),sQuery(id+"F0.wireOp",EDGE,"E10.1.16"),sQuery(id+"F0.wireOp",EDGE,"E10.1.18"),sQuery(id+"F0.wireOp",EDGE,"E10.1.20"),sQuery(id+"F0.wireOp",EDGE,"E10.2.0"),sQuery(id+"F0.wireOp",EDGE,"E10.2.1"),sQuery(id+"F0.wireOp",EDGE,"E10.2.2"),sQuery(id+"F0.wireOp",EDGE,"E10.2.3"),sQuery(id+"F0.wireOp",EDGE,"E10.2.5"),sQuery(id+"F0.wireOp",EDGE,"E10.2.7"),sQuery(id+"F0.wireOp",EDGE,"E10.2.8"),sQuery(id+"F0.wireOp",EDGE,"E10.2.9"),sQuery(id+"F0.wireOp",EDGE,"E10.2.10"),sQuery(id+"F0.wireOp",EDGE,"E10.2.11"),sQuery(id+"F0.wireOp",EDGE,"E10.2.12"),sQuery(id+"F0.wireOp",EDGE,"E1"),sQuery(id+"F0.wireOp",EDGE,"E10.2.14"),sQuery(id+"F0.wireOp",EDGE,"E10.2.15"),sQuery(id+"F0.wireOp",EDGE,"E10.2.16"),sQuery(id+"F0.wireOp",EDGE,"E10.2.18"),sQuery(id+"F0.wireOp",EDGE,"E10.2.20"),sQuery(id+"F0.wireOp",EDGE,"E8.trimOffspring"),sQuery(id+"F0.wireOp",EDGE,"E0"),sQuery(id+"F0.wireOp",EDGE,"E10.1.6"),sQuery(id+"F0.wireOp",EDGE,"E11"),sQuery(id+"F0.wireOp",EDGE,"E12"),sQuery(id+"F0.wireOp",EDGE,"E13.1.0"),sQuery(id+"F0.wireOp",EDGE,"E13.1.1"),sQuery(id+"F0.wireOp",EDGE,"E13.2.0"),sQuery(id+"F0.wireOp",EDGE,"E13.2.1")])]}),"instanceName":"1"});
            var Q2;
            Q2=makeQuery(id+"F19.opPattern","COPY",BODY,{"derivedFrom":makeQuery(id+"F18.opPattern","COPY",BODY,{"derivedFrom":makeQuery(id+"F13.opPattern","COPY",BODY,{"derivedFrom":makeQuery(id+"F1.opExtrude","SWEPT_BODY",BODY,{"disambiguationData":[OSD([sQuery(id+"F0.wireOp",EDGE,"E2.0"),sQuery(id+"F0.wireOp",EDGE,"E2.1"),sQuery(id+"F0.wireOp",EDGE,"E2.2"),sQuery(id+"F0.wireOp",EDGE,"E2.3"),sQuery(id+"F0.wireOp",EDGE,"E2.4"),sQuery(id+"F0.wireOp",EDGE,"E2.5"),sQuery(id+"F0.wireOp",EDGE,"E3"),sQuery(id+"F0.wireOp",EDGE,"E4"),sQuery(id+"F0.wireOp",EDGE,"E5.0"),sQuery(id+"F0.wireOp",EDGE,"E5.1"),sQuery(id+"F0.wireOp",EDGE,"E5.3"),sQuery(id+"F0.wireOp",EDGE,"E5.4"),sQuery(id+"F0.wireOp",EDGE,"E5.5"),sQuery(id+"F0.wireOp",EDGE,"E6.trimOffspring"),sQuery(id+"F0.wireOp",EDGE,"E7.trimOffspring"),sQuery(id+"F0.wireOp",EDGE,"E9.trimOffspring"),sQuery(id+"F0.wireOp",EDGE,"E10.1.0"),sQuery(id+"F0.wireOp",EDGE,"E10.1.1"),sQuery(id+"F0.wireOp",EDGE,"E10.1.2"),sQuery(id+"F0.wireOp",EDGE,"E10.1.3"),sQuery(id+"F0.wireOp",EDGE,"E10.1.5"),sQuery(id+"F0.wireOp",EDGE,"E10.1.7"),sQuery(id+"F0.wireOp",EDGE,"E10.1.8"),sQuery(id+"F0.wireOp",EDGE,"E10.1.9"),sQuery(id+"F0.wireOp",EDGE,"E10.1.10"),sQuery(id+"F0.wireOp",EDGE,"E10.1.11"),sQuery(id+"F0.wireOp",EDGE,"E10.1.12"),sQuery(id+"F0.wireOp",EDGE,"E10.1.14"),sQuery(id+"F0.wireOp",EDGE,"E10.1.15"),sQuery(id+"F0.wireOp",EDGE,"E10.1.16"),sQuery(id+"F0.wireOp",EDGE,"E10.1.18"),sQuery(id+"F0.wireOp",EDGE,"E10.1.20"),sQuery(id+"F0.wireOp",EDGE,"E10.2.0"),sQuery(id+"F0.wireOp",EDGE,"E10.2.1"),sQuery(id+"F0.wireOp",EDGE,"E10.2.2"),sQuery(id+"F0.wireOp",EDGE,"E10.2.3"),sQuery(id+"F0.wireOp",EDGE,"E10.2.5"),sQuery(id+"F0.wireOp",EDGE,"E10.2.7"),sQuery(id+"F0.wireOp",EDGE,"E10.2.8"),sQuery(id+"F0.wireOp",EDGE,"E10.2.9"),sQuery(id+"F0.wireOp",EDGE,"E10.2.10"),sQuery(id+"F0.wireOp",EDGE,"E10.2.11"),sQuery(id+"F0.wireOp",EDGE,"E10.2.12"),sQuery(id+"F0.wireOp",EDGE,"E1"),sQuery(id+"F0.wireOp",EDGE,"E10.2.14"),sQuery(id+"F0.wireOp",EDGE,"E10.2.15"),sQuery(id+"F0.wireOp",EDGE,"E10.2.16"),sQuery(id+"F0.wireOp",EDGE,"E10.2.18"),sQuery(id+"F0.wireOp",EDGE,"E10.2.20"),sQuery(id+"F0.wireOp",EDGE,"E8.trimOffspring"),sQuery(id+"F0.wireOp",EDGE,"E0"),sQuery(id+"F0.wireOp",EDGE,"E10.1.6"),sQuery(id+"F0.wireOp",EDGE,"E11"),sQuery(id+"F0.wireOp",EDGE,"E12"),sQuery(id+"F0.wireOp",EDGE,"E13.1.0"),sQuery(id+"F0.wireOp",EDGE,"E13.1.1"),sQuery(id+"F0.wireOp",EDGE,"E13.2.0"),sQuery(id+"F0.wireOp",EDGE,"E13.2.1")])]}),"instanceName":"1"}),"instanceName":"1"}),"instanceName":"1"});
            transform(context, id + "F56", {"entities" : qUnion([Q0, Q1, Q2]), "transformType" : TransformType.TRANSLATION_3D, "dx" : -8.9 * mm, "dy" : -236.7 * mm, "dz" : 0 * mm, "makeCopy" : true});
        }
        {
            var Q0;
            Q0=makeQuery(id+"F18.opPattern","COPY",BODY,{"derivedFrom":makeQuery(id+"F13.opPattern","COPY",BODY,{"derivedFrom":makeQuery(id+"F1.opExtrude","SWEPT_BODY",BODY,{"disambiguationData":[OSD([sQuery(id+"F0.wireOp",EDGE,"E2.0"),sQuery(id+"F0.wireOp",EDGE,"E2.1"),sQuery(id+"F0.wireOp",EDGE,"E2.2"),sQuery(id+"F0.wireOp",EDGE,"E2.3"),sQuery(id+"F0.wireOp",EDGE,"E2.4"),sQuery(id+"F0.wireOp",EDGE,"E2.5"),sQuery(id+"F0.wireOp",EDGE,"E3"),sQuery(id+"F0.wireOp",EDGE,"E4"),sQuery(id+"F0.wireOp",EDGE,"E5.0"),sQuery(id+"F0.wireOp",EDGE,"E5.1"),sQuery(id+"F0.wireOp",EDGE,"E5.3"),sQuery(id+"F0.wireOp",EDGE,"E5.4"),sQuery(id+"F0.wireOp",EDGE,"E5.5"),sQuery(id+"F0.wireOp",EDGE,"E6.trimOffspring"),sQuery(id+"F0.wireOp",EDGE,"E7.trimOffspring"),sQuery(id+"F0.wireOp",EDGE,"E9.trimOffspring"),sQuery(id+"F0.wireOp",EDGE,"E10.1.0"),sQuery(id+"F0.wireOp",EDGE,"E10.1.1"),sQuery(id+"F0.wireOp",EDGE,"E10.1.2"),sQuery(id+"F0.wireOp",EDGE,"E10.1.3"),sQuery(id+"F0.wireOp",EDGE,"E10.1.5"),sQuery(id+"F0.wireOp",EDGE,"E10.1.7"),sQuery(id+"F0.wireOp",EDGE,"E10.1.8"),sQuery(id+"F0.wireOp",EDGE,"E10.1.9"),sQuery(id+"F0.wireOp",EDGE,"E10.1.10"),sQuery(id+"F0.wireOp",EDGE,"E10.1.11"),sQuery(id+"F0.wireOp",EDGE,"E10.1.12"),sQuery(id+"F0.wireOp",EDGE,"E10.1.14"),sQuery(id+"F0.wireOp",EDGE,"E10.1.15"),sQuery(id+"F0.wireOp",EDGE,"E10.1.16"),sQuery(id+"F0.wireOp",EDGE,"E10.1.18"),sQuery(id+"F0.wireOp",EDGE,"E10.1.20"),sQuery(id+"F0.wireOp",EDGE,"E10.2.0"),sQuery(id+"F0.wireOp",EDGE,"E10.2.1"),sQuery(id+"F0.wireOp",EDGE,"E10.2.2"),sQuery(id+"F0.wireOp",EDGE,"E10.2.3"),sQuery(id+"F0.wireOp",EDGE,"E10.2.5"),sQuery(id+"F0.wireOp",EDGE,"E10.2.7"),sQuery(id+"F0.wireOp",EDGE,"E10.2.8"),sQuery(id+"F0.wireOp",EDGE,"E10.2.9"),sQuery(id+"F0.wireOp",EDGE,"E10.2.10"),sQuery(id+"F0.wireOp",EDGE,"E10.2.11"),sQuery(id+"F0.wireOp",EDGE,"E10.2.12"),sQuery(id+"F0.wireOp",EDGE,"E1"),sQuery(id+"F0.wireOp",EDGE,"E10.2.14"),sQuery(id+"F0.wireOp",EDGE,"E10.2.15"),sQuery(id+"F0.wireOp",EDGE,"E10.2.16"),sQuery(id+"F0.wireOp",EDGE,"E10.2.18"),sQuery(id+"F0.wireOp",EDGE,"E10.2.20"),sQuery(id+"F0.wireOp",EDGE,"E8.trimOffspring"),sQuery(id+"F0.wireOp",EDGE,"E0"),sQuery(id+"F0.wireOp",EDGE,"E10.1.6"),sQuery(id+"F0.wireOp",EDGE,"E11"),sQuery(id+"F0.wireOp",EDGE,"E12"),sQuery(id+"F0.wireOp",EDGE,"E13.1.0"),sQuery(id+"F0.wireOp",EDGE,"E13.1.1"),sQuery(id+"F0.wireOp",EDGE,"E13.2.0"),sQuery(id+"F0.wireOp",EDGE,"E13.2.1")])]}),"instanceName":"1"}),"instanceName":"1"});
            transform(context, id + "F57", {"entities" : qUnion([Q0]), "transformType" : TransformType.TRANSLATION_3D, "dx" : 0 * mm, "dy" : -1.5 * mm, "dz" : 0 * mm, "makeCopy" : false});
        }
        {
            var Q0;
            Q0=makeQuery(id+"F13.opPattern","COPY",BODY,{"derivedFrom":makeQuery(id+"F1.opExtrude","SWEPT_BODY",BODY,{"disambiguationData":[OSD([sQuery(id+"F0.wireOp",EDGE,"E2.0"),sQuery(id+"F0.wireOp",EDGE,"E2.1"),sQuery(id+"F0.wireOp",EDGE,"E2.2"),sQuery(id+"F0.wireOp",EDGE,"E2.3"),sQuery(id+"F0.wireOp",EDGE,"E2.4"),sQuery(id+"F0.wireOp",EDGE,"E2.5"),sQuery(id+"F0.wireOp",EDGE,"E3"),sQuery(id+"F0.wireOp",EDGE,"E4"),sQuery(id+"F0.wireOp",EDGE,"E5.0"),sQuery(id+"F0.wireOp",EDGE,"E5.1"),sQuery(id+"F0.wireOp",EDGE,"E5.3"),sQuery(id+"F0.wireOp",EDGE,"E5.4"),sQuery(id+"F0.wireOp",EDGE,"E5.5"),sQuery(id+"F0.wireOp",EDGE,"E6.trimOffspring"),sQuery(id+"F0.wireOp",EDGE,"E7.trimOffspring"),sQuery(id+"F0.wireOp",EDGE,"E9.trimOffspring"),sQuery(id+"F0.wireOp",EDGE,"E10.1.0"),sQuery(id+"F0.wireOp",EDGE,"E10.1.1"),sQuery(id+"F0.wireOp",EDGE,"E10.1.2"),sQuery(id+"F0.wireOp",EDGE,"E10.1.3"),sQuery(id+"F0.wireOp",EDGE,"E10.1.5"),sQuery(id+"F0.wireOp",EDGE,"E10.1.7"),sQuery(id+"F0.wireOp",EDGE,"E10.1.8"),sQuery(id+"F0.wireOp",EDGE,"E10.1.9"),sQuery(id+"F0.wireOp",EDGE,"E10.1.10"),sQuery(id+"F0.wireOp",EDGE,"E10.1.11"),sQuery(id+"F0.wireOp",EDGE,"E10.1.12"),sQuery(id+"F0.wireOp",EDGE,"E10.1.14"),sQuery(id+"F0.wireOp",EDGE,"E10.1.15"),sQuery(id+"F0.wireOp",EDGE,"E10.1.16"),sQuery(id+"F0.wireOp",EDGE,"E10.1.18"),sQuery(id+"F0.wireOp",EDGE,"E10.1.20"),sQuery(id+"F0.wireOp",EDGE,"E10.2.0"),sQuery(id+"F0.wireOp",EDGE,"E10.2.1"),sQuery(id+"F0.wireOp",EDGE,"E10.2.2"),sQuery(id+"F0.wireOp",EDGE,"E10.2.3"),sQuery(id+"F0.wireOp",EDGE,"E10.2.5"),sQuery(id+"F0.wireOp",EDGE,"E10.2.7"),sQuery(id+"F0.wireOp",EDGE,"E10.2.8"),sQuery(id+"F0.wireOp",EDGE,"E10.2.9"),sQuery(id+"F0.wireOp",EDGE,"E10.2.10"),sQuery(id+"F0.wireOp",EDGE,"E10.2.11"),sQuery(id+"F0.wireOp",EDGE,"E10.2.12"),sQuery(id+"F0.wireOp",EDGE,"E1"),sQuery(id+"F0.wireOp",EDGE,"E10.2.14"),sQuery(id+"F0.wireOp",EDGE,"E10.2.15"),sQuery(id+"F0.wireOp",EDGE,"E10.2.16"),sQuery(id+"F0.wireOp",EDGE,"E10.2.18"),sQuery(id+"F0.wireOp",EDGE,"E10.2.20"),sQuery(id+"F0.wireOp",EDGE,"E8.trimOffspring"),sQuery(id+"F0.wireOp",EDGE,"E0"),sQuery(id+"F0.wireOp",EDGE,"E10.1.6"),sQuery(id+"F0.wireOp",EDGE,"E11"),sQuery(id+"F0.wireOp",EDGE,"E12"),sQuery(id+"F0.wireOp",EDGE,"E13.1.0"),sQuery(id+"F0.wireOp",EDGE,"E13.1.1"),sQuery(id+"F0.wireOp",EDGE,"E13.2.0"),sQuery(id+"F0.wireOp",EDGE,"E13.2.1")])]}),"instanceName":"1"});
            transform(context, id + "F58", {"entities" : qUnion([Q0]), "transformType" : TransformType.TRANSLATION_3D, "dx" : 0.3 * mm, "dy" : 3.2 * mm, "dz" : 0 * mm, "makeCopy" : false});
        }
        {
            var Q0;
            Q0=makeQuery(id+"F19.opPattern","COPY",BODY,{"derivedFrom":makeQuery(id+"F18.opPattern","COPY",BODY,{"derivedFrom":makeQuery(id+"F13.opPattern","COPY",BODY,{"derivedFrom":makeQuery(id+"F1.opExtrude","SWEPT_BODY",BODY,{"disambiguationData":[OSD([sQuery(id+"F0.wireOp",EDGE,"E2.0"),sQuery(id+"F0.wireOp",EDGE,"E2.1"),sQuery(id+"F0.wireOp",EDGE,"E2.2"),sQuery(id+"F0.wireOp",EDGE,"E2.3"),sQuery(id+"F0.wireOp",EDGE,"E2.4"),sQuery(id+"F0.wireOp",EDGE,"E2.5"),sQuery(id+"F0.wireOp",EDGE,"E3"),sQuery(id+"F0.wireOp",EDGE,"E4"),sQuery(id+"F0.wireOp",EDGE,"E5.0"),sQuery(id+"F0.wireOp",EDGE,"E5.1"),sQuery(id+"F0.wireOp",EDGE,"E5.3"),sQuery(id+"F0.wireOp",EDGE,"E5.4"),sQuery(id+"F0.wireOp",EDGE,"E5.5"),sQuery(id+"F0.wireOp",EDGE,"E6.trimOffspring"),sQuery(id+"F0.wireOp",EDGE,"E7.trimOffspring"),sQuery(id+"F0.wireOp",EDGE,"E9.trimOffspring"),sQuery(id+"F0.wireOp",EDGE,"E10.1.0"),sQuery(id+"F0.wireOp",EDGE,"E10.1.1"),sQuery(id+"F0.wireOp",EDGE,"E10.1.2"),sQuery(id+"F0.wireOp",EDGE,"E10.1.3"),sQuery(id+"F0.wireOp",EDGE,"E10.1.5"),sQuery(id+"F0.wireOp",EDGE,"E10.1.7"),sQuery(id+"F0.wireOp",EDGE,"E10.1.8"),sQuery(id+"F0.wireOp",EDGE,"E10.1.9"),sQuery(id+"F0.wireOp",EDGE,"E10.1.10"),sQuery(id+"F0.wireOp",EDGE,"E10.1.11"),sQuery(id+"F0.wireOp",EDGE,"E10.1.12"),sQuery(id+"F0.wireOp",EDGE,"E10.1.14"),sQuery(id+"F0.wireOp",EDGE,"E10.1.15"),sQuery(id+"F0.wireOp",EDGE,"E10.1.16"),sQuery(id+"F0.wireOp",EDGE,"E10.1.18"),sQuery(id+"F0.wireOp",EDGE,"E10.1.20"),sQuery(id+"F0.wireOp",EDGE,"E10.2.0"),sQuery(id+"F0.wireOp",EDGE,"E10.2.1"),sQuery(id+"F0.wireOp",EDGE,"E10.2.2"),sQuery(id+"F0.wireOp",EDGE,"E10.2.3"),sQuery(id+"F0.wireOp",EDGE,"E10.2.5"),sQuery(id+"F0.wireOp",EDGE,"E10.2.7"),sQuery(id+"F0.wireOp",EDGE,"E10.2.8"),sQuery(id+"F0.wireOp",EDGE,"E10.2.9"),sQuery(id+"F0.wireOp",EDGE,"E10.2.10"),sQuery(id+"F0.wireOp",EDGE,"E10.2.11"),sQuery(id+"F0.wireOp",EDGE,"E10.2.12"),sQuery(id+"F0.wireOp",EDGE,"E1"),sQuery(id+"F0.wireOp",EDGE,"E10.2.14"),sQuery(id+"F0.wireOp",EDGE,"E10.2.15"),sQuery(id+"F0.wireOp",EDGE,"E10.2.16"),sQuery(id+"F0.wireOp",EDGE,"E10.2.18"),sQuery(id+"F0.wireOp",EDGE,"E10.2.20"),sQuery(id+"F0.wireOp",EDGE,"E8.trimOffspring"),sQuery(id+"F0.wireOp",EDGE,"E0"),sQuery(id+"F0.wireOp",EDGE,"E10.1.6"),sQuery(id+"F0.wireOp",EDGE,"E11"),sQuery(id+"F0.wireOp",EDGE,"E12"),sQuery(id+"F0.wireOp",EDGE,"E13.1.0"),sQuery(id+"F0.wireOp",EDGE,"E13.1.1"),sQuery(id+"F0.wireOp",EDGE,"E13.2.0"),sQuery(id+"F0.wireOp",EDGE,"E13.2.1")])]}),"instanceName":"1"}),"instanceName":"1"}),"instanceName":"1"});
            transform(context, id + "F59", {"entities" : qUnion([Q0]), "transformType" : TransformType.TRANSLATION_3D, "dx" : 0 * mm, "dy" : -7.9 * mm, "dz" : 0 * mm, "makeCopy" : false});
        }
        {
            var Q0;
            Q0=makeQuery(id+"F56.opPattern","COPY",BODY,{"derivedFrom":makeQuery(id+"F18.opPattern","COPY",BODY,{"derivedFrom":makeQuery(id+"F13.opPattern","COPY",BODY,{"derivedFrom":makeQuery(id+"F1.opExtrude","SWEPT_BODY",BODY,{"disambiguationData":[OSD([sQuery(id+"F0.wireOp",EDGE,"E2.0"),sQuery(id+"F0.wireOp",EDGE,"E2.1"),sQuery(id+"F0.wireOp",EDGE,"E2.2"),sQuery(id+"F0.wireOp",EDGE,"E2.3"),sQuery(id+"F0.wireOp",EDGE,"E2.4"),sQuery(id+"F0.wireOp",EDGE,"E2.5"),sQuery(id+"F0.wireOp",EDGE,"E3"),sQuery(id+"F0.wireOp",EDGE,"E4"),sQuery(id+"F0.wireOp",EDGE,"E5.0"),sQuery(id+"F0.wireOp",EDGE,"E5.1"),sQuery(id+"F0.wireOp",EDGE,"E5.3"),sQuery(id+"F0.wireOp",EDGE,"E5.4"),sQuery(id+"F0.wireOp",EDGE,"E5.5"),sQuery(id+"F0.wireOp",EDGE,"E6.trimOffspring"),sQuery(id+"F0.wireOp",EDGE,"E7.trimOffspring"),sQuery(id+"F0.wireOp",EDGE,"E9.trimOffspring"),sQuery(id+"F0.wireOp",EDGE,"E10.1.0"),sQuery(id+"F0.wireOp",EDGE,"E10.1.1"),sQuery(id+"F0.wireOp",EDGE,"E10.1.2"),sQuery(id+"F0.wireOp",EDGE,"E10.1.3"),sQuery(id+"F0.wireOp",EDGE,"E10.1.5"),sQuery(id+"F0.wireOp",EDGE,"E10.1.7"),sQuery(id+"F0.wireOp",EDGE,"E10.1.8"),sQuery(id+"F0.wireOp",EDGE,"E10.1.9"),sQuery(id+"F0.wireOp",EDGE,"E10.1.10"),sQuery(id+"F0.wireOp",EDGE,"E10.1.11"),sQuery(id+"F0.wireOp",EDGE,"E10.1.12"),sQuery(id+"F0.wireOp",EDGE,"E10.1.14"),sQuery(id+"F0.wireOp",EDGE,"E10.1.15"),sQuery(id+"F0.wireOp",EDGE,"E10.1.16"),sQuery(id+"F0.wireOp",EDGE,"E10.1.18"),sQuery(id+"F0.wireOp",EDGE,"E10.1.20"),sQuery(id+"F0.wireOp",EDGE,"E10.2.0"),sQuery(id+"F0.wireOp",EDGE,"E10.2.1"),sQuery(id+"F0.wireOp",EDGE,"E10.2.2"),sQuery(id+"F0.wireOp",EDGE,"E10.2.3"),sQuery(id+"F0.wireOp",EDGE,"E10.2.5"),sQuery(id+"F0.wireOp",EDGE,"E10.2.7"),sQuery(id+"F0.wireOp",EDGE,"E10.2.8"),sQuery(id+"F0.wireOp",EDGE,"E10.2.9"),sQuery(id+"F0.wireOp",EDGE,"E10.2.10"),sQuery(id+"F0.wireOp",EDGE,"E10.2.11"),sQuery(id+"F0.wireOp",EDGE,"E10.2.12"),sQuery(id+"F0.wireOp",EDGE,"E1"),sQuery(id+"F0.wireOp",EDGE,"E10.2.14"),sQuery(id+"F0.wireOp",EDGE,"E10.2.15"),sQuery(id+"F0.wireOp",EDGE,"E10.2.16"),sQuery(id+"F0.wireOp",EDGE,"E10.2.18"),sQuery(id+"F0.wireOp",EDGE,"E10.2.20"),sQuery(id+"F0.wireOp",EDGE,"E8.trimOffspring"),sQuery(id+"F0.wireOp",EDGE,"E0"),sQuery(id+"F0.wireOp",EDGE,"E10.1.6"),sQuery(id+"F0.wireOp",EDGE,"E11"),sQuery(id+"F0.wireOp",EDGE,"E12"),sQuery(id+"F0.wireOp",EDGE,"E13.1.0"),sQuery(id+"F0.wireOp",EDGE,"E13.1.1"),sQuery(id+"F0.wireOp",EDGE,"E13.2.0"),sQuery(id+"F0.wireOp",EDGE,"E13.2.1")])]}),"instanceName":"1"}),"instanceName":"1"}),"instanceName":"1"});
            transform(context, id + "F60", {"entities" : qUnion([Q0]), "transformType" : TransformType.TRANSLATION_3D, "dx" : 0 * mm, "dy" : -3 * mm, "dz" : 0 * mm, "makeCopy" : false});
        }
        {
            var Q0;
            Q0=makeQuery(id+"F56.opPattern","COPY",BODY,{"derivedFrom":makeQuery(id+"F18.opPattern","COPY",BODY,{"derivedFrom":makeQuery(id+"F13.opPattern","COPY",BODY,{"derivedFrom":makeQuery(id+"F1.opExtrude","SWEPT_BODY",BODY,{"disambiguationData":[OSD([sQuery(id+"F0.wireOp",EDGE,"E2.0"),sQuery(id+"F0.wireOp",EDGE,"E2.1"),sQuery(id+"F0.wireOp",EDGE,"E2.2"),sQuery(id+"F0.wireOp",EDGE,"E2.3"),sQuery(id+"F0.wireOp",EDGE,"E2.4"),sQuery(id+"F0.wireOp",EDGE,"E2.5"),sQuery(id+"F0.wireOp",EDGE,"E3"),sQuery(id+"F0.wireOp",EDGE,"E4"),sQuery(id+"F0.wireOp",EDGE,"E5.0"),sQuery(id+"F0.wireOp",EDGE,"E5.1"),sQuery(id+"F0.wireOp",EDGE,"E5.3"),sQuery(id+"F0.wireOp",EDGE,"E5.4"),sQuery(id+"F0.wireOp",EDGE,"E5.5"),sQuery(id+"F0.wireOp",EDGE,"E6.trimOffspring"),sQuery(id+"F0.wireOp",EDGE,"E7.trimOffspring"),sQuery(id+"F0.wireOp",EDGE,"E9.trimOffspring"),sQuery(id+"F0.wireOp",EDGE,"E10.1.0"),sQuery(id+"F0.wireOp",EDGE,"E10.1.1"),sQuery(id+"F0.wireOp",EDGE,"E10.1.2"),sQuery(id+"F0.wireOp",EDGE,"E10.1.3"),sQuery(id+"F0.wireOp",EDGE,"E10.1.5"),sQuery(id+"F0.wireOp",EDGE,"E10.1.7"),sQuery(id+"F0.wireOp",EDGE,"E10.1.8"),sQuery(id+"F0.wireOp",EDGE,"E10.1.9"),sQuery(id+"F0.wireOp",EDGE,"E10.1.10"),sQuery(id+"F0.wireOp",EDGE,"E10.1.11"),sQuery(id+"F0.wireOp",EDGE,"E10.1.12"),sQuery(id+"F0.wireOp",EDGE,"E10.1.14"),sQuery(id+"F0.wireOp",EDGE,"E10.1.15"),sQuery(id+"F0.wireOp",EDGE,"E10.1.16"),sQuery(id+"F0.wireOp",EDGE,"E10.1.18"),sQuery(id+"F0.wireOp",EDGE,"E10.1.20"),sQuery(id+"F0.wireOp",EDGE,"E10.2.0"),sQuery(id+"F0.wireOp",EDGE,"E10.2.1"),sQuery(id+"F0.wireOp",EDGE,"E10.2.2"),sQuery(id+"F0.wireOp",EDGE,"E10.2.3"),sQuery(id+"F0.wireOp",EDGE,"E10.2.5"),sQuery(id+"F0.wireOp",EDGE,"E10.2.7"),sQuery(id+"F0.wireOp",EDGE,"E10.2.8"),sQuery(id+"F0.wireOp",EDGE,"E10.2.9"),sQuery(id+"F0.wireOp",EDGE,"E10.2.10"),sQuery(id+"F0.wireOp",EDGE,"E10.2.11"),sQuery(id+"F0.wireOp",EDGE,"E10.2.12"),sQuery(id+"F0.wireOp",EDGE,"E1"),sQuery(id+"F0.wireOp",EDGE,"E10.2.14"),sQuery(id+"F0.wireOp",EDGE,"E10.2.15"),sQuery(id+"F0.wireOp",EDGE,"E10.2.16"),sQuery(id+"F0.wireOp",EDGE,"E10.2.18"),sQuery(id+"F0.wireOp",EDGE,"E10.2.20"),sQuery(id+"F0.wireOp",EDGE,"E8.trimOffspring"),sQuery(id+"F0.wireOp",EDGE,"E0"),sQuery(id+"F0.wireOp",EDGE,"E10.1.6"),sQuery(id+"F0.wireOp",EDGE,"E11"),sQuery(id+"F0.wireOp",EDGE,"E12"),sQuery(id+"F0.wireOp",EDGE,"E13.1.0"),sQuery(id+"F0.wireOp",EDGE,"E13.1.1"),sQuery(id+"F0.wireOp",EDGE,"E13.2.0"),sQuery(id+"F0.wireOp",EDGE,"E13.2.1")])]}),"instanceName":"1"}),"instanceName":"1"}),"instanceName":"1"});
            transform(context, id + "F61", {"entities" : qUnion([Q0]), "transformType" : TransformType.TRANSLATION_3D, "dx" : 0 * mm, "dy" : -2 * mm, "dz" : 0 * mm, "makeCopy" : false});
        }
        {
            var Q0;
            Q0=makeQuery(id+"F56.opPattern","COPY",BODY,{"derivedFrom":makeQuery(id+"F19.opPattern","COPY",BODY,{"derivedFrom":makeQuery(id+"F18.opPattern","COPY",BODY,{"derivedFrom":makeQuery(id+"F13.opPattern","COPY",BODY,{"derivedFrom":makeQuery(id+"F1.opExtrude","SWEPT_BODY",BODY,{"disambiguationData":[OSD([sQuery(id+"F0.wireOp",EDGE,"E2.0"),sQuery(id+"F0.wireOp",EDGE,"E2.1"),sQuery(id+"F0.wireOp",EDGE,"E2.2"),sQuery(id+"F0.wireOp",EDGE,"E2.3"),sQuery(id+"F0.wireOp",EDGE,"E2.4"),sQuery(id+"F0.wireOp",EDGE,"E2.5"),sQuery(id+"F0.wireOp",EDGE,"E3"),sQuery(id+"F0.wireOp",EDGE,"E4"),sQuery(id+"F0.wireOp",EDGE,"E5.0"),sQuery(id+"F0.wireOp",EDGE,"E5.1"),sQuery(id+"F0.wireOp",EDGE,"E5.3"),sQuery(id+"F0.wireOp",EDGE,"E5.4"),sQuery(id+"F0.wireOp",EDGE,"E5.5"),sQuery(id+"F0.wireOp",EDGE,"E6.trimOffspring"),sQuery(id+"F0.wireOp",EDGE,"E7.trimOffspring"),sQuery(id+"F0.wireOp",EDGE,"E9.trimOffspring"),sQuery(id+"F0.wireOp",EDGE,"E10.1.0"),sQuery(id+"F0.wireOp",EDGE,"E10.1.1"),sQuery(id+"F0.wireOp",EDGE,"E10.1.2"),sQuery(id+"F0.wireOp",EDGE,"E10.1.3"),sQuery(id+"F0.wireOp",EDGE,"E10.1.5"),sQuery(id+"F0.wireOp",EDGE,"E10.1.7"),sQuery(id+"F0.wireOp",EDGE,"E10.1.8"),sQuery(id+"F0.wireOp",EDGE,"E10.1.9"),sQuery(id+"F0.wireOp",EDGE,"E10.1.10"),sQuery(id+"F0.wireOp",EDGE,"E10.1.11"),sQuery(id+"F0.wireOp",EDGE,"E10.1.12"),sQuery(id+"F0.wireOp",EDGE,"E10.1.14"),sQuery(id+"F0.wireOp",EDGE,"E10.1.15"),sQuery(id+"F0.wireOp",EDGE,"E10.1.16"),sQuery(id+"F0.wireOp",EDGE,"E10.1.18"),sQuery(id+"F0.wireOp",EDGE,"E10.1.20"),sQuery(id+"F0.wireOp",EDGE,"E10.2.0"),sQuery(id+"F0.wireOp",EDGE,"E10.2.1"),sQuery(id+"F0.wireOp",EDGE,"E10.2.2"),sQuery(id+"F0.wireOp",EDGE,"E10.2.3"),sQuery(id+"F0.wireOp",EDGE,"E10.2.5"),sQuery(id+"F0.wireOp",EDGE,"E10.2.7"),sQuery(id+"F0.wireOp",EDGE,"E10.2.8"),sQuery(id+"F0.wireOp",EDGE,"E10.2.9"),sQuery(id+"F0.wireOp",EDGE,"E10.2.10"),sQuery(id+"F0.wireOp",EDGE,"E10.2.11"),sQuery(id+"F0.wireOp",EDGE,"E10.2.12"),sQuery(id+"F0.wireOp",EDGE,"E1"),sQuery(id+"F0.wireOp",EDGE,"E10.2.14"),sQuery(id+"F0.wireOp",EDGE,"E10.2.15"),sQuery(id+"F0.wireOp",EDGE,"E10.2.16"),sQuery(id+"F0.wireOp",EDGE,"E10.2.18"),sQuery(id+"F0.wireOp",EDGE,"E10.2.20"),sQuery(id+"F0.wireOp",EDGE,"E8.trimOffspring"),sQuery(id+"F0.wireOp",EDGE,"E0"),sQuery(id+"F0.wireOp",EDGE,"E10.1.6"),sQuery(id+"F0.wireOp",EDGE,"E11"),sQuery(id+"F0.wireOp",EDGE,"E12"),sQuery(id+"F0.wireOp",EDGE,"E13.1.0"),sQuery(id+"F0.wireOp",EDGE,"E13.1.1"),sQuery(id+"F0.wireOp",EDGE,"E13.2.0"),sQuery(id+"F0.wireOp",EDGE,"E13.2.1")])]}),"instanceName":"1"}),"instanceName":"1"}),"instanceName":"1"}),"instanceName":"1"});
            transform(context, id + "F62", {"entities" : qUnion([Q0]), "transformType" : TransformType.TRANSLATION_3D, "dx" : 0.8 * mm, "dy" : -9 * mm, "dz" : 0 * mm, "makeCopy" : false});
        }
        {
            var Q0;
            Q0=makeQuery(id+"F47.opPattern","COPY",BODY,{"derivedFrom":makeQuery(id+"F42.opPattern","COPY",BODY,{"derivedFrom":makeQuery(id+"F13.opPattern","COPY",BODY,{"derivedFrom":makeQuery(id+"F1.opExtrude","SWEPT_BODY",BODY,{"disambiguationData":[OSD([sQuery(id+"F0.wireOp",EDGE,"E2.0"),sQuery(id+"F0.wireOp",EDGE,"E2.1"),sQuery(id+"F0.wireOp",EDGE,"E2.2"),sQuery(id+"F0.wireOp",EDGE,"E2.3"),sQuery(id+"F0.wireOp",EDGE,"E2.4"),sQuery(id+"F0.wireOp",EDGE,"E2.5"),sQuery(id+"F0.wireOp",EDGE,"E3"),sQuery(id+"F0.wireOp",EDGE,"E4"),sQuery(id+"F0.wireOp",EDGE,"E5.0"),sQuery(id+"F0.wireOp",EDGE,"E5.1"),sQuery(id+"F0.wireOp",EDGE,"E5.3"),sQuery(id+"F0.wireOp",EDGE,"E5.4"),sQuery(id+"F0.wireOp",EDGE,"E5.5"),sQuery(id+"F0.wireOp",EDGE,"E6.trimOffspring"),sQuery(id+"F0.wireOp",EDGE,"E7.trimOffspring"),sQuery(id+"F0.wireOp",EDGE,"E9.trimOffspring"),sQuery(id+"F0.wireOp",EDGE,"E10.1.0"),sQuery(id+"F0.wireOp",EDGE,"E10.1.1"),sQuery(id+"F0.wireOp",EDGE,"E10.1.2"),sQuery(id+"F0.wireOp",EDGE,"E10.1.3"),sQuery(id+"F0.wireOp",EDGE,"E10.1.5"),sQuery(id+"F0.wireOp",EDGE,"E10.1.7"),sQuery(id+"F0.wireOp",EDGE,"E10.1.8"),sQuery(id+"F0.wireOp",EDGE,"E10.1.9"),sQuery(id+"F0.wireOp",EDGE,"E10.1.10"),sQuery(id+"F0.wireOp",EDGE,"E10.1.11"),sQuery(id+"F0.wireOp",EDGE,"E10.1.12"),sQuery(id+"F0.wireOp",EDGE,"E10.1.14"),sQuery(id+"F0.wireOp",EDGE,"E10.1.15"),sQuery(id+"F0.wireOp",EDGE,"E10.1.16"),sQuery(id+"F0.wireOp",EDGE,"E10.1.18"),sQuery(id+"F0.wireOp",EDGE,"E10.1.20"),sQuery(id+"F0.wireOp",EDGE,"E10.2.0"),sQuery(id+"F0.wireOp",EDGE,"E10.2.1"),sQuery(id+"F0.wireOp",EDGE,"E10.2.2"),sQuery(id+"F0.wireOp",EDGE,"E10.2.3"),sQuery(id+"F0.wireOp",EDGE,"E10.2.5"),sQuery(id+"F0.wireOp",EDGE,"E10.2.7"),sQuery(id+"F0.wireOp",EDGE,"E10.2.8"),sQuery(id+"F0.wireOp",EDGE,"E10.2.9"),sQuery(id+"F0.wireOp",EDGE,"E10.2.10"),sQuery(id+"F0.wireOp",EDGE,"E10.2.11"),sQuery(id+"F0.wireOp",EDGE,"E10.2.12"),sQuery(id+"F0.wireOp",EDGE,"E1"),sQuery(id+"F0.wireOp",EDGE,"E10.2.14"),sQuery(id+"F0.wireOp",EDGE,"E10.2.15"),sQuery(id+"F0.wireOp",EDGE,"E10.2.16"),sQuery(id+"F0.wireOp",EDGE,"E10.2.18"),sQuery(id+"F0.wireOp",EDGE,"E10.2.20"),sQuery(id+"F0.wireOp",EDGE,"E8.trimOffspring"),sQuery(id+"F0.wireOp",EDGE,"E0"),sQuery(id+"F0.wireOp",EDGE,"E10.1.6"),sQuery(id+"F0.wireOp",EDGE,"E11"),sQuery(id+"F0.wireOp",EDGE,"E12"),sQuery(id+"F0.wireOp",EDGE,"E13.1.0"),sQuery(id+"F0.wireOp",EDGE,"E13.1.1"),sQuery(id+"F0.wireOp",EDGE,"E13.2.0"),sQuery(id+"F0.wireOp",EDGE,"E13.2.1")])]}),"instanceName":"1"}),"instanceName":"1"}),"instanceName":"1"});
            transform(context, id + "F63", {"entities" : qUnion([Q0]), "transformType" : TransformType.TRANSLATION_3D, "dx" : 30.5 * mm, "dy" : -98.2 * mm, "dz" : 0 * mm, "makeCopy" : true});
        }
        {
            var Q0;
            Q0=makeQuery(id+"F48.opPattern","COPY",BODY,{"derivedFrom":makeQuery(id+"F39.opPattern","COPY",BODY,{"derivedFrom":makeQuery(id+"F36.opPattern","COPY",BODY,{"derivedFrom":makeQuery(id+"F23.opPattern","COPY",BODY,{"derivedFrom":makeQuery(id+"F7.opPattern","COPY",BODY,{"derivedFrom":makeQuery(id+"F1.opExtrude","SWEPT_BODY",BODY,{"disambiguationData":[OSD([sQuery(id+"F0.wireOp",EDGE,"E2.0"),sQuery(id+"F0.wireOp",EDGE,"E2.1"),sQuery(id+"F0.wireOp",EDGE,"E2.2"),sQuery(id+"F0.wireOp",EDGE,"E2.3"),sQuery(id+"F0.wireOp",EDGE,"E2.4"),sQuery(id+"F0.wireOp",EDGE,"E2.5"),sQuery(id+"F0.wireOp",EDGE,"E3"),sQuery(id+"F0.wireOp",EDGE,"E4"),sQuery(id+"F0.wireOp",EDGE,"E5.0"),sQuery(id+"F0.wireOp",EDGE,"E5.1"),sQuery(id+"F0.wireOp",EDGE,"E5.3"),sQuery(id+"F0.wireOp",EDGE,"E5.4"),sQuery(id+"F0.wireOp",EDGE,"E5.5"),sQuery(id+"F0.wireOp",EDGE,"E6.trimOffspring"),sQuery(id+"F0.wireOp",EDGE,"E7.trimOffspring"),sQuery(id+"F0.wireOp",EDGE,"E9.trimOffspring"),sQuery(id+"F0.wireOp",EDGE,"E10.1.0"),sQuery(id+"F0.wireOp",EDGE,"E10.1.1"),sQuery(id+"F0.wireOp",EDGE,"E10.1.2"),sQuery(id+"F0.wireOp",EDGE,"E10.1.3"),sQuery(id+"F0.wireOp",EDGE,"E10.1.5"),sQuery(id+"F0.wireOp",EDGE,"E10.1.7"),sQuery(id+"F0.wireOp",EDGE,"E10.1.8"),sQuery(id+"F0.wireOp",EDGE,"E10.1.9"),sQuery(id+"F0.wireOp",EDGE,"E10.1.10"),sQuery(id+"F0.wireOp",EDGE,"E10.1.11"),sQuery(id+"F0.wireOp",EDGE,"E10.1.12"),sQuery(id+"F0.wireOp",EDGE,"E10.1.14"),sQuery(id+"F0.wireOp",EDGE,"E10.1.15"),sQuery(id+"F0.wireOp",EDGE,"E10.1.16"),sQuery(id+"F0.wireOp",EDGE,"E10.1.18"),sQuery(id+"F0.wireOp",EDGE,"E10.1.20"),sQuery(id+"F0.wireOp",EDGE,"E10.2.0"),sQuery(id+"F0.wireOp",EDGE,"E10.2.1"),sQuery(id+"F0.wireOp",EDGE,"E10.2.2"),sQuery(id+"F0.wireOp",EDGE,"E10.2.3"),sQuery(id+"F0.wireOp",EDGE,"E10.2.5"),sQuery(id+"F0.wireOp",EDGE,"E10.2.7"),sQuery(id+"F0.wireOp",EDGE,"E10.2.8"),sQuery(id+"F0.wireOp",EDGE,"E10.2.9"),sQuery(id+"F0.wireOp",EDGE,"E10.2.10"),sQuery(id+"F0.wireOp",EDGE,"E10.2.11"),sQuery(id+"F0.wireOp",EDGE,"E10.2.12"),sQuery(id+"F0.wireOp",EDGE,"E1"),sQuery(id+"F0.wireOp",EDGE,"E10.2.14"),sQuery(id+"F0.wireOp",EDGE,"E10.2.15"),sQuery(id+"F0.wireOp",EDGE,"E10.2.16"),sQuery(id+"F0.wireOp",EDGE,"E10.2.18"),sQuery(id+"F0.wireOp",EDGE,"E10.2.20"),sQuery(id+"F0.wireOp",EDGE,"E8.trimOffspring"),sQuery(id+"F0.wireOp",EDGE,"E0"),sQuery(id+"F0.wireOp",EDGE,"E10.1.6"),sQuery(id+"F0.wireOp",EDGE,"E11"),sQuery(id+"F0.wireOp",EDGE,"E12"),sQuery(id+"F0.wireOp",EDGE,"E13.1.0"),sQuery(id+"F0.wireOp",EDGE,"E13.1.1"),sQuery(id+"F0.wireOp",EDGE,"E13.2.0"),sQuery(id+"F0.wireOp",EDGE,"E13.2.1")])]}),"instanceName":"1"}),"instanceName":"1"}),"instanceName":"1"}),"instanceName":"1"}),"instanceName":"1"});
            transform(context, id + "F64", {"entities" : qUnion([Q0]), "transformType" : TransformType.TRANSLATION_3D, "dx" : 0 * mm, "dy" : -84.1 * mm, "dz" : 0 * mm, "makeCopy" : true});
        }
        {
            var Q0;
            Q0=makeQuery(id+"F48.opPattern","COPY",BODY,{"derivedFrom":makeQuery(id+"F39.opPattern","COPY",BODY,{"derivedFrom":makeQuery(id+"F36.opPattern","COPY",BODY,{"derivedFrom":makeQuery(id+"F23.opPattern","COPY",BODY,{"derivedFrom":makeQuery(id+"F7.opPattern","COPY",BODY,{"derivedFrom":makeQuery(id+"F1.opExtrude","SWEPT_BODY",BODY,{"disambiguationData":[OSD([sQuery(id+"F0.wireOp",EDGE,"E2.0"),sQuery(id+"F0.wireOp",EDGE,"E2.1"),sQuery(id+"F0.wireOp",EDGE,"E2.2"),sQuery(id+"F0.wireOp",EDGE,"E2.3"),sQuery(id+"F0.wireOp",EDGE,"E2.4"),sQuery(id+"F0.wireOp",EDGE,"E2.5"),sQuery(id+"F0.wireOp",EDGE,"E3"),sQuery(id+"F0.wireOp",EDGE,"E4"),sQuery(id+"F0.wireOp",EDGE,"E5.0"),sQuery(id+"F0.wireOp",EDGE,"E5.1"),sQuery(id+"F0.wireOp",EDGE,"E5.3"),sQuery(id+"F0.wireOp",EDGE,"E5.4"),sQuery(id+"F0.wireOp",EDGE,"E5.5"),sQuery(id+"F0.wireOp",EDGE,"E6.trimOffspring"),sQuery(id+"F0.wireOp",EDGE,"E7.trimOffspring"),sQuery(id+"F0.wireOp",EDGE,"E9.trimOffspring"),sQuery(id+"F0.wireOp",EDGE,"E10.1.0"),sQuery(id+"F0.wireOp",EDGE,"E10.1.1"),sQuery(id+"F0.wireOp",EDGE,"E10.1.2"),sQuery(id+"F0.wireOp",EDGE,"E10.1.3"),sQuery(id+"F0.wireOp",EDGE,"E10.1.5"),sQuery(id+"F0.wireOp",EDGE,"E10.1.7"),sQuery(id+"F0.wireOp",EDGE,"E10.1.8"),sQuery(id+"F0.wireOp",EDGE,"E10.1.9"),sQuery(id+"F0.wireOp",EDGE,"E10.1.10"),sQuery(id+"F0.wireOp",EDGE,"E10.1.11"),sQuery(id+"F0.wireOp",EDGE,"E10.1.12"),sQuery(id+"F0.wireOp",EDGE,"E10.1.14"),sQuery(id+"F0.wireOp",EDGE,"E10.1.15"),sQuery(id+"F0.wireOp",EDGE,"E10.1.16"),sQuery(id+"F0.wireOp",EDGE,"E10.1.18"),sQuery(id+"F0.wireOp",EDGE,"E10.1.20"),sQuery(id+"F0.wireOp",EDGE,"E10.2.0"),sQuery(id+"F0.wireOp",EDGE,"E10.2.1"),sQuery(id+"F0.wireOp",EDGE,"E10.2.2"),sQuery(id+"F0.wireOp",EDGE,"E10.2.3"),sQuery(id+"F0.wireOp",EDGE,"E10.2.5"),sQuery(id+"F0.wireOp",EDGE,"E10.2.7"),sQuery(id+"F0.wireOp",EDGE,"E10.2.8"),sQuery(id+"F0.wireOp",EDGE,"E10.2.9"),sQuery(id+"F0.wireOp",EDGE,"E10.2.10"),sQuery(id+"F0.wireOp",EDGE,"E10.2.11"),sQuery(id+"F0.wireOp",EDGE,"E10.2.12"),sQuery(id+"F0.wireOp",EDGE,"E1"),sQuery(id+"F0.wireOp",EDGE,"E10.2.14"),sQuery(id+"F0.wireOp",EDGE,"E10.2.15"),sQuery(id+"F0.wireOp",EDGE,"E10.2.16"),sQuery(id+"F0.wireOp",EDGE,"E10.2.18"),sQuery(id+"F0.wireOp",EDGE,"E10.2.20"),sQuery(id+"F0.wireOp",EDGE,"E8.trimOffspring"),sQuery(id+"F0.wireOp",EDGE,"E0"),sQuery(id+"F0.wireOp",EDGE,"E10.1.6"),sQuery(id+"F0.wireOp",EDGE,"E11"),sQuery(id+"F0.wireOp",EDGE,"E12"),sQuery(id+"F0.wireOp",EDGE,"E13.1.0"),sQuery(id+"F0.wireOp",EDGE,"E13.1.1"),sQuery(id+"F0.wireOp",EDGE,"E13.2.0"),sQuery(id+"F0.wireOp",EDGE,"E13.2.1")])]}),"instanceName":"1"}),"instanceName":"1"}),"instanceName":"1"}),"instanceName":"1"}),"instanceName":"1"});
            transform(context, id + "F65", {"entities" : qUnion([Q0]), "transformType" : TransformType.TRANSLATION_3D, "dx" : -1 * mm, "dy" : 0 * mm, "dz" : 0 * mm, "makeCopy" : false});
        }
        {
            var Q0;
            Q0=makeQuery(id+"F48.opPattern","COPY",BODY,{"derivedFrom":makeQuery(id+"F39.opPattern","COPY",BODY,{"derivedFrom":makeQuery(id+"F36.opPattern","COPY",BODY,{"derivedFrom":makeQuery(id+"F23.opPattern","COPY",BODY,{"derivedFrom":makeQuery(id+"F7.opPattern","COPY",BODY,{"derivedFrom":makeQuery(id+"F1.opExtrude","SWEPT_BODY",BODY,{"disambiguationData":[OSD([sQuery(id+"F0.wireOp",EDGE,"E2.0"),sQuery(id+"F0.wireOp",EDGE,"E2.1"),sQuery(id+"F0.wireOp",EDGE,"E2.2"),sQuery(id+"F0.wireOp",EDGE,"E2.3"),sQuery(id+"F0.wireOp",EDGE,"E2.4"),sQuery(id+"F0.wireOp",EDGE,"E2.5"),sQuery(id+"F0.wireOp",EDGE,"E3"),sQuery(id+"F0.wireOp",EDGE,"E4"),sQuery(id+"F0.wireOp",EDGE,"E5.0"),sQuery(id+"F0.wireOp",EDGE,"E5.1"),sQuery(id+"F0.wireOp",EDGE,"E5.3"),sQuery(id+"F0.wireOp",EDGE,"E5.4"),sQuery(id+"F0.wireOp",EDGE,"E5.5"),sQuery(id+"F0.wireOp",EDGE,"E6.trimOffspring"),sQuery(id+"F0.wireOp",EDGE,"E7.trimOffspring"),sQuery(id+"F0.wireOp",EDGE,"E9.trimOffspring"),sQuery(id+"F0.wireOp",EDGE,"E10.1.0"),sQuery(id+"F0.wireOp",EDGE,"E10.1.1"),sQuery(id+"F0.wireOp",EDGE,"E10.1.2"),sQuery(id+"F0.wireOp",EDGE,"E10.1.3"),sQuery(id+"F0.wireOp",EDGE,"E10.1.5"),sQuery(id+"F0.wireOp",EDGE,"E10.1.7"),sQuery(id+"F0.wireOp",EDGE,"E10.1.8"),sQuery(id+"F0.wireOp",EDGE,"E10.1.9"),sQuery(id+"F0.wireOp",EDGE,"E10.1.10"),sQuery(id+"F0.wireOp",EDGE,"E10.1.11"),sQuery(id+"F0.wireOp",EDGE,"E10.1.12"),sQuery(id+"F0.wireOp",EDGE,"E10.1.14"),sQuery(id+"F0.wireOp",EDGE,"E10.1.15"),sQuery(id+"F0.wireOp",EDGE,"E10.1.16"),sQuery(id+"F0.wireOp",EDGE,"E10.1.18"),sQuery(id+"F0.wireOp",EDGE,"E10.1.20"),sQuery(id+"F0.wireOp",EDGE,"E10.2.0"),sQuery(id+"F0.wireOp",EDGE,"E10.2.1"),sQuery(id+"F0.wireOp",EDGE,"E10.2.2"),sQuery(id+"F0.wireOp",EDGE,"E10.2.3"),sQuery(id+"F0.wireOp",EDGE,"E10.2.5"),sQuery(id+"F0.wireOp",EDGE,"E10.2.7"),sQuery(id+"F0.wireOp",EDGE,"E10.2.8"),sQuery(id+"F0.wireOp",EDGE,"E10.2.9"),sQuery(id+"F0.wireOp",EDGE,"E10.2.10"),sQuery(id+"F0.wireOp",EDGE,"E10.2.11"),sQuery(id+"F0.wireOp",EDGE,"E10.2.12"),sQuery(id+"F0.wireOp",EDGE,"E1"),sQuery(id+"F0.wireOp",EDGE,"E10.2.14"),sQuery(id+"F0.wireOp",EDGE,"E10.2.15"),sQuery(id+"F0.wireOp",EDGE,"E10.2.16"),sQuery(id+"F0.wireOp",EDGE,"E10.2.18"),sQuery(id+"F0.wireOp",EDGE,"E10.2.20"),sQuery(id+"F0.wireOp",EDGE,"E8.trimOffspring"),sQuery(id+"F0.wireOp",EDGE,"E0"),sQuery(id+"F0.wireOp",EDGE,"E10.1.6"),sQuery(id+"F0.wireOp",EDGE,"E11"),sQuery(id+"F0.wireOp",EDGE,"E12"),sQuery(id+"F0.wireOp",EDGE,"E13.1.0"),sQuery(id+"F0.wireOp",EDGE,"E13.1.1"),sQuery(id+"F0.wireOp",EDGE,"E13.2.0"),sQuery(id+"F0.wireOp",EDGE,"E13.2.1")])]}),"instanceName":"1"}),"instanceName":"1"}),"instanceName":"1"}),"instanceName":"1"}),"instanceName":"1"});
            var Q1;
            Q1=makeQuery(id+"F48.opPattern","COPY",EDGE,{"derivedFrom":makeQuery(id+"F39.opPattern","COPY",EDGE,{"derivedFrom":makeQuery(id+"F36.opPattern","COPY",EDGE,{"derivedFrom":makeQuery(id+"F23.opPattern","COPY",EDGE,{"derivedFrom":makeQuery(id+"F7.opPattern","COPY",EDGE,{"derivedFrom":makeQuery(id+"F1.opExtrude","CAP_EDGE",EDGE,{"disambiguationData":[OSD([sQuery(id+"F0.wireOp",EDGE,"E1")])],"isStart":false}),"instanceName":"1"}),"instanceName":"1"}),"instanceName":"1"}),"instanceName":"1"}),"instanceName":"1"});
            transform(context, id + "F66", {"entities" : qUnion([Q0]), "transformType" : TransformType.ROTATION, "transformAxis" : qUnion([Q1]), "angle" : 10 * degree, "oppositeDirection" : true, "makeCopy" : false});
        }
        {
            var Q0;
            Q0=makeQuery(id+"F51.opPattern","COPY",BODY,{"derivedFrom":makeQuery(id+"F39.opPattern","COPY",BODY,{"derivedFrom":makeQuery(id+"F36.opPattern","COPY",BODY,{"derivedFrom":makeQuery(id+"F23.opPattern","COPY",BODY,{"derivedFrom":makeQuery(id+"F7.opPattern","COPY",BODY,{"derivedFrom":makeQuery(id+"F1.opExtrude","SWEPT_BODY",BODY,{"disambiguationData":[OSD([sQuery(id+"F0.wireOp",EDGE,"E2.0"),sQuery(id+"F0.wireOp",EDGE,"E2.1"),sQuery(id+"F0.wireOp",EDGE,"E2.2"),sQuery(id+"F0.wireOp",EDGE,"E2.3"),sQuery(id+"F0.wireOp",EDGE,"E2.4"),sQuery(id+"F0.wireOp",EDGE,"E2.5"),sQuery(id+"F0.wireOp",EDGE,"E3"),sQuery(id+"F0.wireOp",EDGE,"E4"),sQuery(id+"F0.wireOp",EDGE,"E5.0"),sQuery(id+"F0.wireOp",EDGE,"E5.1"),sQuery(id+"F0.wireOp",EDGE,"E5.3"),sQuery(id+"F0.wireOp",EDGE,"E5.4"),sQuery(id+"F0.wireOp",EDGE,"E5.5"),sQuery(id+"F0.wireOp",EDGE,"E6.trimOffspring"),sQuery(id+"F0.wireOp",EDGE,"E7.trimOffspring"),sQuery(id+"F0.wireOp",EDGE,"E9.trimOffspring"),sQuery(id+"F0.wireOp",EDGE,"E10.1.0"),sQuery(id+"F0.wireOp",EDGE,"E10.1.1"),sQuery(id+"F0.wireOp",EDGE,"E10.1.2"),sQuery(id+"F0.wireOp",EDGE,"E10.1.3"),sQuery(id+"F0.wireOp",EDGE,"E10.1.5"),sQuery(id+"F0.wireOp",EDGE,"E10.1.7"),sQuery(id+"F0.wireOp",EDGE,"E10.1.8"),sQuery(id+"F0.wireOp",EDGE,"E10.1.9"),sQuery(id+"F0.wireOp",EDGE,"E10.1.10"),sQuery(id+"F0.wireOp",EDGE,"E10.1.11"),sQuery(id+"F0.wireOp",EDGE,"E10.1.12"),sQuery(id+"F0.wireOp",EDGE,"E10.1.14"),sQuery(id+"F0.wireOp",EDGE,"E10.1.15"),sQuery(id+"F0.wireOp",EDGE,"E10.1.16"),sQuery(id+"F0.wireOp",EDGE,"E10.1.18"),sQuery(id+"F0.wireOp",EDGE,"E10.1.20"),sQuery(id+"F0.wireOp",EDGE,"E10.2.0"),sQuery(id+"F0.wireOp",EDGE,"E10.2.1"),sQuery(id+"F0.wireOp",EDGE,"E10.2.2"),sQuery(id+"F0.wireOp",EDGE,"E10.2.3"),sQuery(id+"F0.wireOp",EDGE,"E10.2.5"),sQuery(id+"F0.wireOp",EDGE,"E10.2.7"),sQuery(id+"F0.wireOp",EDGE,"E10.2.8"),sQuery(id+"F0.wireOp",EDGE,"E10.2.9"),sQuery(id+"F0.wireOp",EDGE,"E10.2.10"),sQuery(id+"F0.wireOp",EDGE,"E10.2.11"),sQuery(id+"F0.wireOp",EDGE,"E10.2.12"),sQuery(id+"F0.wireOp",EDGE,"E1"),sQuery(id+"F0.wireOp",EDGE,"E10.2.14"),sQuery(id+"F0.wireOp",EDGE,"E10.2.15"),sQuery(id+"F0.wireOp",EDGE,"E10.2.16"),sQuery(id+"F0.wireOp",EDGE,"E10.2.18"),sQuery(id+"F0.wireOp",EDGE,"E10.2.20"),sQuery(id+"F0.wireOp",EDGE,"E8.trimOffspring"),sQuery(id+"F0.wireOp",EDGE,"E0"),sQuery(id+"F0.wireOp",EDGE,"E10.1.6"),sQuery(id+"F0.wireOp",EDGE,"E11"),sQuery(id+"F0.wireOp",EDGE,"E12"),sQuery(id+"F0.wireOp",EDGE,"E13.1.0"),sQuery(id+"F0.wireOp",EDGE,"E13.1.1"),sQuery(id+"F0.wireOp",EDGE,"E13.2.0"),sQuery(id+"F0.wireOp",EDGE,"E13.2.1")])]}),"instanceName":"1"}),"instanceName":"1"}),"instanceName":"1"}),"instanceName":"1"}),"instanceName":"1"});
            transform(context, id + "F67", {"entities" : qUnion([Q0]), "transformType" : TransformType.TRANSLATION_3D, "dx" : 34 * mm, "dy" : -107 * mm, "dz" : 0 * mm, "makeCopy" : true});
        }
    });
